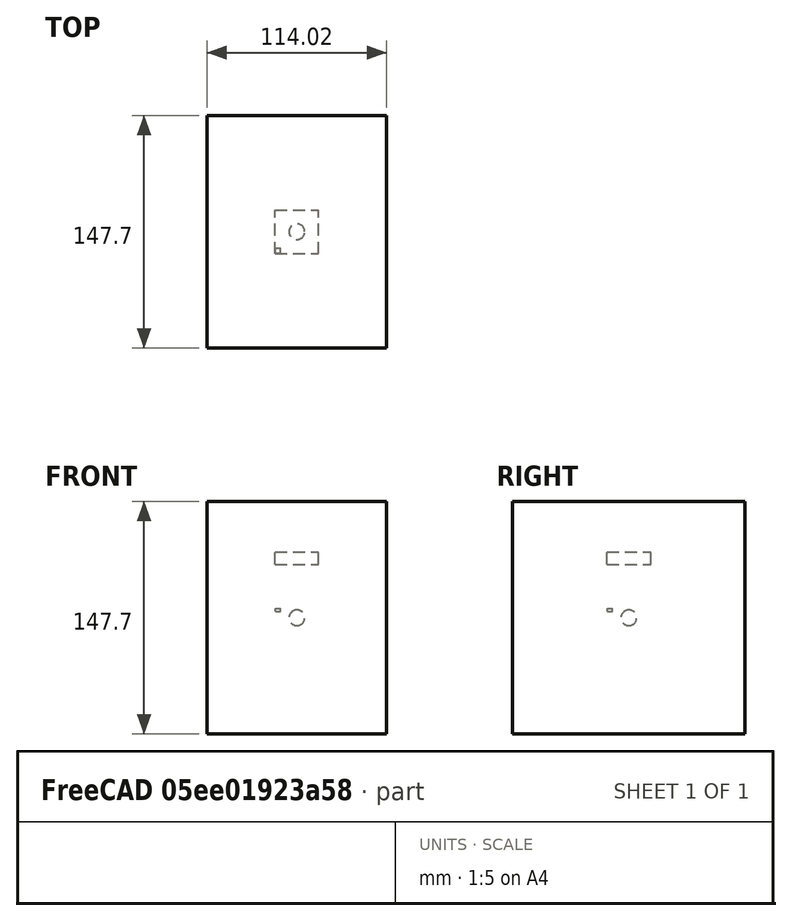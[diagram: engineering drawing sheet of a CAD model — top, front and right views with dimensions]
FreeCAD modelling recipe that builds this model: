
FCSTD DOCUMENT  (FreeCAD 1.0R39109 (Git))
Label: borderTest-1
License: All rights reserved
objects: App::DocumentObjectGroupPython×1272, Part::FeaturePython×7, App::Part×4, App::FeaturePython×1
note: 4 computed .brp shape members not serialized (recipe doc carries the construction recipe); baked Part::Feature solids carry a one-line shape summary decoded from their .brp

FEATURE [App::DocumentObjectGroupPython] HALFPI  # scripted group (container) (typed FeaturePython)
  name = HALFPI
  value = pi/2.
FEATURE [App::DocumentObjectGroupPython] PI  # scripted group (container) (typed FeaturePython)
  name = PI
  value = 1.*pi
FEATURE [App::DocumentObjectGroupPython] TWOPI  # scripted group (container) (typed FeaturePython)
  name = TWOPI
  value = 2.*pi
FEATURE [App::DocumentObjectGroupPython] Constants  # scripted group (container) (typed FeaturePython)
  Group = -> [HALFPI,PI,TWOPI]
FEATURE [App::DocumentObjectGroupPython] Variables  # scripted group (container) (typed FeaturePython)
FEATURE [App::DocumentObjectGroupPython] Quantities  # scripted group (container) (typed FeaturePython)
FEATURE [App::DocumentObjectGroupPython] Isotopes  # scripted group (container) (typed FeaturePython)
FEATURE [App::DocumentObjectGroupPython] Elements  # scripted group (container) (typed FeaturePython)
FEATURE [App::DocumentObjectGroupPython] G4_AIR  label="G4_AIR : 1.000"  # scripted group (container) (typed FeaturePython)
  n = 1
FEATURE [App::DocumentObjectGroupPython] Air  # scripted group (container) (typed FeaturePython)
  Dunit = mg/cm3
  Dvalue = 1.29
  Group = -> [G4_AIR]
  RINDEX = AirRINDEX
  conduct = 2
  density = 1
  expand = 3
  name = Air
  specific = 4
FEATURE [App::DocumentObjectGroupPython] SY  # scripted group (container) (typed FeaturePython)
  coldim = 1
  values = 100000/MeV
FEATURE [App::DocumentObjectGroupPython] RS  # scripted group (container) (typed FeaturePython)
  coldim = 1
  values = 1
FEATURE [App::DocumentObjectGroupPython] FTC  # scripted group (container) (typed FeaturePython)
  coldim = 1
  values = 21.5*ns
FEATURE [App::DocumentObjectGroupPython] STC  # scripted group (container) (typed FeaturePython)
  coldim = 1
  values = 43.8*ns
FEATURE [App::DocumentObjectGroupPython] RY1  # scripted group (container) (typed FeaturePython)
  coldim = 1
  values = 95
FEATURE [App::DocumentObjectGroupPython] RY2  # scripted group (container) (typed FeaturePython)
  coldim = 1
  values = 5
FEATURE [App::DocumentObjectGroupPython] YR  # scripted group (container) (typed FeaturePython)
  coldim = 1
  values = 0.8
FEATURE [App::DocumentObjectGroupPython] SCINTLAR  # scripted group (container) (typed FeaturePython)
  coldim = 2
  values = <blob: 2358 chars omitted>
FEATURE [App::DocumentObjectGroupPython] RINDEXLAR  # scripted group (container) (typed FeaturePython)
  coldim = 2
  values = <blob: 9384 chars omitted>
FEATURE [App::DocumentObjectGroupPython] ABSLENGTHLAR  # scripted group (container) (typed FeaturePython)
  coldim = 2
  values = 7.74901*eV 10.0*m 7.77525*eV 10.0*m 7.80167*eV 10.0*m 7.82827*eV 10.0*m 7.85506*eV 10.0*m 7.88202*eV 10.0*m 7.90917*eV 10.0*m 7.93651*eV 10.0*m 7.96404*eV 10.0*m 7.99176*eV 10.0*m 8.01968*eV 10.0*m 8.04779*eV 10.0*m 8.07609*eV 10.0*m 8.1046*eV 10.0*m 8.13331*eV 10.0*m 8.16222*eV 10.0*m 8.19134*eV 10.0*m 8.22067*eV 10.0*m 8.25021*eV 10.0*m 8.27996*eV 10.0*m 8.30993*eV 10.0*m 8.34012*eV 10.0*m 8.37052*eV 10.0*m 8.40115*eV 10.0*m 8.432*eV 10.0*m 8.46308*eV 10.0*m 8.4944*eV 10.0*m 8.52594*eV 10.0*m 8.55772*eV 10.0*m 8.58973*eV 10.0*m 8.62199*eV 10.0*m 8.65449*eV 10.0*m 8.68723*eV 10.0*m 8.72023*eV 10.0*m 8.75347*eV 10.0*m 8.78697*eV 10.0*m 8.82073*eV 10.0*m 8.85475*eV 10.0*m 8.88903*eV 10.0*m 8.92358*eV 10.0*m 8.9584*eV 10.0*m 8.99349*eV 10.0*m 9.02885*eV 10.0*m 9.0645*eV 10.0*m 9.10043*eV 10.0*m 9.13664*eV 10.0*m 9.17314*eV 10.0*m 9.20994*eV 10.0*m 9.24703*eV 10.0*m 9.28442*eV 10.0*m 9.32212*eV 10.0*m 9.36012*eV 10.0*m 9.39844*eV 10.0*m 9.43707*eV 10.0*m 9.47602*eV 10.0*m 9.51529*eV 10.0*m 9.55489*eV 10.0*m 9.59481*eV 10.0*m 9.63508*eV 10.0*m 9.67568*eV 10.0*m 9.71663*eV 10.0*m 9.75792*eV 10.0*m 9.79957*eV 10.0*m 9.84158*eV 10.0*m 9.88394*eV 10.0*m 9.92668*eV 10.0*m 9.96978*eV 10.0*m 10.0133*eV 10.0*m 10.0571*eV 10.0*m 10.1014*eV 10.0*m 10.146*eV 10.0*m 10.191*eV 10.0*m 10.2365*eV 10.0*m 10.2823*eV 10.0*m 10.3286*eV 10.0*m 10.3752*eV 10.0*m 10.4223*eV 10.0*m 10.4699*eV 10.0*m 10.5178*eV 10.0*m 10.5662*eV 10.0*m 10.6151*eV 10.0*m 10.6644*eV 10.0*m 10.7142*eV 10.0*m 10.7644*eV 10.0*m 10.8151*eV 10.0*m 10.8663*eV 10.0*m 10.9179*eV 10.0*m 10.9701*eV 10.0*m 11.0228*eV 10.0*m 11.076*eV 10.0*m 11.1296*eV 10.0*m 11.1839*eV 10.0*m 11.2386*eV 10.0*m 11.2939*eV 10.0*m 11.3497*eV 10.0*m 11.4061*eV 10.0*m 11.463*eV 10.0*m 11.5206*eV 10.0*m 11.5787*eV 10.0*m 11.6373*eV 10.0*m
FEATURE [App::DocumentObjectGroupPython] RAYLEIGHLAR  # scripted group (container) (typed FeaturePython)
  coldim = 2
  values = 7.74901*eV 90.0*cm 7.77525*eV 90.0*cm 7.80167*eV 90.0*cm 7.82827*eV 90.0*cm 7.85506*eV 90.0*cm 7.88202*eV 90.0*cm 7.90917*eV 90.0*cm 7.93651*eV 90.0*cm 7.96404*eV 90.0*cm 7.99176*eV 90.0*cm 8.01968*eV 90.0*cm 8.04779*eV 90.0*cm 8.07609*eV 90.0*cm 8.1046*eV 90.0*cm 8.13331*eV 90.0*cm 8.16222*eV 90.0*cm 8.19134*eV 90.0*cm 8.22067*eV 90.0*cm 8.25021*eV 90.0*cm 8.27996*eV 90.0*cm 8.30993*eV 90.0*cm 8.34012*eV 90.0*cm 8.37052*eV 90.0*cm 8.40115*eV 90.0*cm 8.432*eV 90.0*cm 8.46308*eV 90.0*cm 8.4944*eV 90.0*cm 8.52594*eV 90.0*cm 8.55772*eV 90.0*cm 8.58973*eV 90.0*cm 8.62199*eV 90.0*cm 8.65449*eV 90.0*cm 8.68723*eV 90.0*cm 8.72023*eV 90.0*cm 8.75347*eV 90.0*cm 8.78697*eV 90.0*cm 8.82073*eV 90.0*cm 8.85475*eV 90.0*cm 8.88903*eV 90.0*cm 8.92358*eV 90.0*cm 8.9584*eV 90.0*cm 8.99349*eV 90.0*cm 9.02885*eV 90.0*cm 9.0645*eV 90.0*cm 9.10043*eV 90.0*cm 9.13664*eV 90.0*cm 9.17314*eV 90.0*cm 9.20994*eV 90.0*cm 9.24703*eV 90.0*cm 9.28442*eV 90.0*cm 9.32212*eV 90.0*cm 9.36012*eV 90.0*cm 9.39844*eV 90.0*cm 9.43707*eV 90.0*cm 9.47602*eV 90.0*cm 9.51529*eV 90.0*cm 9.55489*eV 90.0*cm 9.59481*eV 90.0*cm 9.63508*eV 90.0*cm 9.67568*eV 90.0*cm 9.71663*eV 90.0*cm 9.75792*eV 90.0*cm 9.79957*eV 90.0*cm 9.84158*eV 90.0*cm 9.88394*eV 90.0*cm 9.92668*eV 90.0*cm 9.96978*eV 90.0*cm 10.0133*eV 90.0*cm 10.0571*eV 90.0*cm 10.1014*eV 90.0*cm 10.146*eV 90.0*cm 10.191*eV 90.0*cm 10.2365*eV 90.0*cm 10.2823*eV 90.0*cm 10.3286*eV 90.0*cm 10.3752*eV 90.0*cm 10.4223*eV 90.0*cm 10.4699*eV 90.0*cm 10.5178*eV 90.0*cm 10.5662*eV 90.0*cm 10.6151*eV 90.0*cm 10.6644*eV 90.0*cm 10.7142*eV 90.0*cm 10.7644*eV 90.0*cm 10.8151*eV 90.0*cm 10.8663*eV 90.0*cm 10.9179*eV 90.0*cm 10.9701*eV 90.0*cm 11.0228*eV 90.0*cm 11.076*eV 90.0*cm 11.1296*eV 90.0*cm 11.1839*eV 90.0*cm 11.2386*eV 90.0*cm 11.2939*eV 90.0*cm 11.3497*eV 90.0*cm 11.4061*eV 90.0*cm 11.463*eV 90.0*cm 11.5206*eV 90.0*cm 11.5787*eV 90.0*cm 11.6373*eV 90.0*cm
FEATURE [App::DocumentObjectGroupPython] REFLECTIVITY  # scripted group (container) (typed FeaturePython)
  coldim = 2
  values = 2.034*eV 0.98 2.068*eV 0.98 2.103*eV 0.98 2.139*eV 0.98 2.177*eV 0.98 2.216*eV 0.98 2.256*eV 0.98 2.298*eV 0.98 2.341*eV 0.98 2.386*eV 0.98 2.433*eV 0.98 2.481*eV 0.98 2.532*eV 0.98 2.585*eV 0.98 2.64*eV 0.98 2.697*eV 0.98 2.757*eV 0.98 2.82*eV 0.98 2.885*eV 0.98 2.954*eV 0.98 3.026*eV 0.98 3.102*eV 0.98 3.181*eV 0.98 3.265*eV 0.98 3.353*eV 0.98 3.446*eV 0.98 3.545*eV 0.98 3.649*eV 0.98 3.76*eV 0.98 3.877*eV 0.98 4.002*eV 0.98 4.136*eV 0.98 5.0*eV 0.98 6.0*eV 0.98 7.0*eV 0.98 8.0*eV 0.98 9.0*eV 0.98 9.0*eV 0.98 10.0*eV 0.98 11.0*eV 0.98 11.6*eV 0.98
FEATURE [App::DocumentObjectGroupPython] EFFICIENCY  # scripted group (container) (typed FeaturePython)
  coldim = 2
  values = 2.034*eV 1 2.068*eV 1 2.103*eV 1 2.139*eV 1 2.177*eV 1 2.216*eV 1 2.256*eV 1 2.298*eV 1 2.341*eV 1 2.386*eV 1 2.433*eV 1 2.481*eV 1 2.532*eV 1 2.585*eV 1 2.64*eV 1 2.697*eV 1 2.757*eV 1 2.82*eV 1 2.885*eV 1 2.954*eV 1 3.026*eV 1 3.102*eV 1 3.181*eV  1 3.265*eV 1 3.353*eV 1 3.446*eV 1 3.545*eV 1 3.649*eV 1 3.76*eV 1 3.877*eV 1 4.002*eV 1 4.136*eV 1 5.0*eV 1 6.0*eV 1 7.0*eV 1 8.0*eV 1 9.0*eV 1 9.0*eV 1 10.0*eV 1 11.0*eV 1 11.6*eV 1
FEATURE [App::DocumentObjectGroupPython] AirRINDEX  # scripted group (container) (typed FeaturePython)
  coldim = 2
  values = 2.034*eV 1 2.068*eV 1 2.103*eV 1 2.139*eV 1 2.177*eV 1 2.216*eV 1 2.256*eV 1 2.298*eV 1 2.341*eV 1 2.386*eV 1 2.433*eV 1 2.481*eV 1 2.532*eV 1 2.585*eV 1 2.64*eV 1 2.697*eV 1 2.757*eV 1 2.82*eV 1 2.885*eV 1 2.954*eV 1 3.026*eV 1 3.102*eV 1 3.181*eV 1 3.265*eV 1 3.353*eV 1 3.446*eV 1 3.545*eV 1 3.649*eV 1 3.76*eV 1 3.877*eV 1 4.002*eV 1 4.136*eV 1 5.0*eV 1 6.0*eV 1 7.0*eV 1 8.0*eV 1 9.0*eV 1 10.0*eV 1 11.0*eV 1 11.6*eV 1
FEATURE [App::DocumentObjectGroupPython] Matrix  # scripted group (container) (typed FeaturePython)
  Group = -> [SY,RS,FTC,STC,RY1,RY2,YR,SCINTLAR,RINDEXLAR,ABSLENGTHLAR,RAYLEIGHLAR,REFLECTIVITY,EFFICIENCY,AirRINDEX]
FEATURE [App::DocumentObjectGroupPython] ScintWrap  # scripted group (container) (typed FeaturePython)
  EFFICIENCY = EFFICIENCY
  REFLECTIVITY = REFLECTIVITY
  finish = 39
  model = 0
  type = 2
  value = 1
FEATURE [App::DocumentObjectGroupPython] Surfaces  # scripted group (container) (typed FeaturePython)
  Group = -> [ScintWrap]
FEATURE [App::DocumentObjectGroupPython] Opticals  # scripted group (container) (typed FeaturePython)
  Group = -> [Matrix,Surfaces]
FEATURE [App::DocumentObjectGroupPython] G4Isotopes  # scripted group (container) (typed FeaturePython)
FEATURE [App::DocumentObjectGroupPython] H_element  # scripted group (container) (typed FeaturePython)
  Z = 1
  atom_value = 1.008
  formula = H
  name = H_element
FEATURE [App::DocumentObjectGroupPython] He_element  # scripted group (container) (typed FeaturePython)
  Z = 2
  atom_value = 4.0026
  formula = He
  name = He_element
FEATURE [App::DocumentObjectGroupPython] Li_element  # scripted group (container) (typed FeaturePython)
  Z = 3
  atom_value = 6.94
  formula = Li
  name = Li_element
FEATURE [App::DocumentObjectGroupPython] Be_element  # scripted group (container) (typed FeaturePython)
  Z = 4
  atom_value = 9.01218
  formula = Be
  name = Be_element
FEATURE [App::DocumentObjectGroupPython] B_element  # scripted group (container) (typed FeaturePython)
  Z = 5
  atom_value = 10.81
  formula = B
  name = B_element
FEATURE [App::DocumentObjectGroupPython] C_element  # scripted group (container) (typed FeaturePython)
  Z = 6
  atom_value = 12.011
  formula = C
  name = C_element
FEATURE [App::DocumentObjectGroupPython] N_element  # scripted group (container) (typed FeaturePython)
  Z = 7
  atom_value = 14.007
  formula = N
  name = N_element
FEATURE [App::DocumentObjectGroupPython] O_element  # scripted group (container) (typed FeaturePython)
  Z = 8
  atom_value = 15.999
  formula = O
  name = O_element
FEATURE [App::DocumentObjectGroupPython] F_element  # scripted group (container) (typed FeaturePython)
  Z = 9
  atom_value = 18.9984
  formula = F
  name = F_element
FEATURE [App::DocumentObjectGroupPython] Ne_element  # scripted group (container) (typed FeaturePython)
  Z = 10
  atom_value = 20.1797
  formula = Ne
  name = Ne_element
FEATURE [App::DocumentObjectGroupPython] Na_element  # scripted group (container) (typed FeaturePython)
  Z = 11
  atom_value = 22.9898
  formula = Na
  name = Na_element
FEATURE [App::DocumentObjectGroupPython] Mg_element  # scripted group (container) (typed FeaturePython)
  Z = 12
  atom_value = 24.305
  formula = Mg
  name = Mg_element
FEATURE [App::DocumentObjectGroupPython] Al_element  # scripted group (container) (typed FeaturePython)
  Z = 13
  atom_value = 26.9815
  formula = Al
  name = Al_element
FEATURE [App::DocumentObjectGroupPython] Si_element  # scripted group (container) (typed FeaturePython)
  Z = 14
  atom_value = 28.085
  formula = Si
  name = Si_element
FEATURE [App::DocumentObjectGroupPython] P_element  # scripted group (container) (typed FeaturePython)
  Z = 15
  atom_value = 30.9738
  formula = P
  name = P_element
FEATURE [App::DocumentObjectGroupPython] S_element  # scripted group (container) (typed FeaturePython)
  Z = 16
  atom_value = 32.06
  formula = S
  name = S_element
FEATURE [App::DocumentObjectGroupPython] Cl_element  # scripted group (container) (typed FeaturePython)
  Z = 17
  atom_value = 35.45
  formula = Cl
  name = Cl_element
FEATURE [App::DocumentObjectGroupPython] Ar_element  # scripted group (container) (typed FeaturePython)
  Z = 18
  atom_value = 39.95
  formula = Ar
  name = Ar_element
FEATURE [App::DocumentObjectGroupPython] K_element  # scripted group (container) (typed FeaturePython)
  Z = 19
  atom_value = 39.0983
  formula = K
  name = K_element
FEATURE [App::DocumentObjectGroupPython] Ca_element  # scripted group (container) (typed FeaturePython)
  Z = 20
  atom_value = 40.078
  formula = Ca
  name = Ca_element
FEATURE [App::DocumentObjectGroupPython] Sc_element  # scripted group (container) (typed FeaturePython)
  Z = 21
  atom_value = 44.9559
  formula = Sc
  name = Sc_element
FEATURE [App::DocumentObjectGroupPython] Ti_element  # scripted group (container) (typed FeaturePython)
  Z = 22
  atom_value = 47.867
  formula = Ti
  name = Ti_element
FEATURE [App::DocumentObjectGroupPython] V_element  # scripted group (container) (typed FeaturePython)
  Z = 23
  atom_value = 50.9415
  formula = V
  name = V_element
FEATURE [App::DocumentObjectGroupPython] Cr_element  # scripted group (container) (typed FeaturePython)
  Z = 24
  atom_value = 51.9961
  formula = Cr
  name = Cr_element
FEATURE [App::DocumentObjectGroupPython] Mn_element  # scripted group (container) (typed FeaturePython)
  Z = 25
  atom_value = 54.938
  formula = Mn
  name = Mn_element
FEATURE [App::DocumentObjectGroupPython] Fe_element  # scripted group (container) (typed FeaturePython)
  Z = 26
  atom_value = 55.845
  formula = Fe
  name = Fe_element
FEATURE [App::DocumentObjectGroupPython] Co_element  # scripted group (container) (typed FeaturePython)
  Z = 27
  atom_value = 58.9332
  formula = Co
  name = Co_element
FEATURE [App::DocumentObjectGroupPython] Ni_element  # scripted group (container) (typed FeaturePython)
  Z = 28
  atom_value = 58.6934
  formula = Ni
  name = Ni_element
FEATURE [App::DocumentObjectGroupPython] Cu_element  # scripted group (container) (typed FeaturePython)
  Z = 29
  atom_value = 63.546
  formula = Cu
  name = Cu_element
FEATURE [App::DocumentObjectGroupPython] Zn_element  # scripted group (container) (typed FeaturePython)
  Z = 30
  atom_value = 65.38
  formula = Zn
  name = Zn_element
FEATURE [App::DocumentObjectGroupPython] Ga_element  # scripted group (container) (typed FeaturePython)
  Z = 31
  atom_value = 69.723
  formula = Ga
  name = Ga_element
FEATURE [App::DocumentObjectGroupPython] Ge_element  # scripted group (container) (typed FeaturePython)
  Z = 32
  atom_value = 72.63
  formula = Ge
  name = Ge_element
FEATURE [App::DocumentObjectGroupPython] As_element  # scripted group (container) (typed FeaturePython)
  Z = 33
  atom_value = 74.9216
  formula = As
  name = As_element
FEATURE [App::DocumentObjectGroupPython] Se_element  # scripted group (container) (typed FeaturePython)
  Z = 34
  atom_value = 78.971
  formula = Se
  name = Se_element
FEATURE [App::DocumentObjectGroupPython] Br_element  # scripted group (container) (typed FeaturePython)
  Z = 35
  atom_value = 79.904
  formula = Br
  name = Br_element
FEATURE [App::DocumentObjectGroupPython] Kr_element  # scripted group (container) (typed FeaturePython)
  Z = 36
  atom_value = 83.798
  formula = Kr
  name = Kr_element
FEATURE [App::DocumentObjectGroupPython] Rb_element  # scripted group (container) (typed FeaturePython)
  Z = 37
  atom_value = 85.4678
  formula = Rb
  name = Rb_element
FEATURE [App::DocumentObjectGroupPython] Sr_element  # scripted group (container) (typed FeaturePython)
  Z = 38
  atom_value = 87.62
  formula = Sr
  name = Sr_element
FEATURE [App::DocumentObjectGroupPython] Y_element  # scripted group (container) (typed FeaturePython)
  Z = 39
  atom_value = 88.9058
  formula = Y
  name = Y_element
FEATURE [App::DocumentObjectGroupPython] Zr_element  # scripted group (container) (typed FeaturePython)
  Z = 40
  atom_value = 91.224
  formula = Zr
  name = Zr_element
FEATURE [App::DocumentObjectGroupPython] Nb_element  # scripted group (container) (typed FeaturePython)
  Z = 41
  atom_value = 92.9064
  formula = Nb
  name = Nb_element
FEATURE [App::DocumentObjectGroupPython] Mo_element  # scripted group (container) (typed FeaturePython)
  Z = 42
  atom_value = 95.95
  formula = Mo
  name = Mo_element
FEATURE [App::DocumentObjectGroupPython] Tc_element  # scripted group (container) (typed FeaturePython)
  Z = 43
  atom_value = 97
  formula = Tc
  name = Tc_element
FEATURE [App::DocumentObjectGroupPython] Ru_element  # scripted group (container) (typed FeaturePython)
  Z = 44
  atom_value = 101.07
  formula = Ru
  name = Ru_element
FEATURE [App::DocumentObjectGroupPython] Rh_element  # scripted group (container) (typed FeaturePython)
  Z = 45
  atom_value = 102.905
  formula = Rh
  name = Rh_element
FEATURE [App::DocumentObjectGroupPython] Pd_element  # scripted group (container) (typed FeaturePython)
  Z = 46
  atom_value = 106.42
  formula = Pd
  name = Pd_element
FEATURE [App::DocumentObjectGroupPython] Ag_element  # scripted group (container) (typed FeaturePython)
  Z = 47
  atom_value = 107.868
  formula = Ag
  name = Ag_element
FEATURE [App::DocumentObjectGroupPython] Cd_element  # scripted group (container) (typed FeaturePython)
  Z = 48
  atom_value = 112.414
  formula = Cd
  name = Cd_element
FEATURE [App::DocumentObjectGroupPython] In_element  # scripted group (container) (typed FeaturePython)
  Z = 49
  atom_value = 114.818
  formula = In
  name = In_element
FEATURE [App::DocumentObjectGroupPython] Sn_element  # scripted group (container) (typed FeaturePython)
  Z = 50
  atom_value = 118.71
  formula = Sn
  name = Sn_element
FEATURE [App::DocumentObjectGroupPython] Sb_element  # scripted group (container) (typed FeaturePython)
  Z = 51
  atom_value = 121.76
  formula = Sb
  name = Sb_element
FEATURE [App::DocumentObjectGroupPython] Te_element  # scripted group (container) (typed FeaturePython)
  Z = 52
  atom_value = 127.6
  formula = Te
  name = Te_element
FEATURE [App::DocumentObjectGroupPython] I_element  # scripted group (container) (typed FeaturePython)
  Z = 53
  atom_value = 126.904
  formula = I
  name = I_element
FEATURE [App::DocumentObjectGroupPython] Xe_element  # scripted group (container) (typed FeaturePython)
  Z = 54
  atom_value = 131.293
  formula = Xe
  name = Xe_element
FEATURE [App::DocumentObjectGroupPython] Cs_element  # scripted group (container) (typed FeaturePython)
  Z = 55
  atom_value = 132.905
  formula = Cs
  name = Cs_element
FEATURE [App::DocumentObjectGroupPython] Ba_element  # scripted group (container) (typed FeaturePython)
  Z = 56
  atom_value = 137.327
  formula = Ba
  name = Ba_element
FEATURE [App::DocumentObjectGroupPython] La_element  # scripted group (container) (typed FeaturePython)
  Z = 57
  atom_value = 138.905
  formula = La
  name = La_element
FEATURE [App::DocumentObjectGroupPython] Ce_element  # scripted group (container) (typed FeaturePython)
  Z = 58
  atom_value = 140.116
  formula = Ce
  name = Ce_element
FEATURE [App::DocumentObjectGroupPython] Pr_element  # scripted group (container) (typed FeaturePython)
  Z = 59
  atom_value = 140.908
  formula = Pr
  name = Pr_element
FEATURE [App::DocumentObjectGroupPython] Nd_element  # scripted group (container) (typed FeaturePython)
  Z = 60
  atom_value = 144.242
  formula = Nd
  name = Nd_element
FEATURE [App::DocumentObjectGroupPython] Pm_element  # scripted group (container) (typed FeaturePython)
  Z = 61
  atom_value = 145
  formula = Pm
  name = Pm_element
FEATURE [App::DocumentObjectGroupPython] Sm_element  # scripted group (container) (typed FeaturePython)
  Z = 62
  atom_value = 150.36
  formula = Sm
  name = Sm_element
FEATURE [App::DocumentObjectGroupPython] Eu_element  # scripted group (container) (typed FeaturePython)
  Z = 63
  atom_value = 151.964
  formula = Eu
  name = Eu_element
FEATURE [App::DocumentObjectGroupPython] Gd_element  # scripted group (container) (typed FeaturePython)
  Z = 64
  atom_value = 157.25
  formula = Gd
  name = Gd_element
FEATURE [App::DocumentObjectGroupPython] Tb_element  # scripted group (container) (typed FeaturePython)
  Z = 65
  atom_value = 158.925
  formula = Tb
  name = Tb_element
FEATURE [App::DocumentObjectGroupPython] Dy_element  # scripted group (container) (typed FeaturePython)
  Z = 66
  atom_value = 162.5
  formula = Dy
  name = Dy_element
FEATURE [App::DocumentObjectGroupPython] Ho_element  # scripted group (container) (typed FeaturePython)
  Z = 67
  atom_value = 164.93
  formula = Ho
  name = Ho_element
FEATURE [App::DocumentObjectGroupPython] Er_element  # scripted group (container) (typed FeaturePython)
  Z = 68
  atom_value = 167.259
  formula = Er
  name = Er_element
FEATURE [App::DocumentObjectGroupPython] Tm_element  # scripted group (container) (typed FeaturePython)
  Z = 69
  atom_value = 168.934
  formula = Tm
  name = Tm_element
FEATURE [App::DocumentObjectGroupPython] Yb_element  # scripted group (container) (typed FeaturePython)
  Z = 70
  atom_value = 173.045
  formula = Yb
  name = Yb_element
FEATURE [App::DocumentObjectGroupPython] Lu_element  # scripted group (container) (typed FeaturePython)
  Z = 71
  atom_value = 174.967
  formula = Lu
  name = Lu_element
FEATURE [App::DocumentObjectGroupPython] Hf_element  # scripted group (container) (typed FeaturePython)
  Z = 72
  atom_value = 178.49
  formula = Hf
  name = Hf_element
FEATURE [App::DocumentObjectGroupPython] Ta_element  # scripted group (container) (typed FeaturePython)
  Z = 73
  atom_value = 180.948
  formula = Ta
  name = Ta_element
FEATURE [App::DocumentObjectGroupPython] W_element  # scripted group (container) (typed FeaturePython)
  Z = 74
  atom_value = 183.84
  formula = W
  name = W_element
FEATURE [App::DocumentObjectGroupPython] Re_element  # scripted group (container) (typed FeaturePython)
  Z = 75
  atom_value = 186.207
  formula = Re
  name = Re_element
FEATURE [App::DocumentObjectGroupPython] Os_element  # scripted group (container) (typed FeaturePython)
  Z = 76
  atom_value = 190.23
  formula = Os
  name = Os_element
FEATURE [App::DocumentObjectGroupPython] Ir_element  # scripted group (container) (typed FeaturePython)
  Z = 77
  atom_value = 192.217
  formula = Ir
  name = Ir_element
FEATURE [App::DocumentObjectGroupPython] Pt_element  # scripted group (container) (typed FeaturePython)
  Z = 78
  atom_value = 195.084
  formula = Pt
  name = Pt_element
FEATURE [App::DocumentObjectGroupPython] Au_element  # scripted group (container) (typed FeaturePython)
  Z = 79
  atom_value = 196.967
  formula = Au
  name = Au_element
FEATURE [App::DocumentObjectGroupPython] Hg_element  # scripted group (container) (typed FeaturePython)
  Z = 80
  atom_value = 200.592
  formula = Hg
  name = Hg_element
FEATURE [App::DocumentObjectGroupPython] Tl_element  # scripted group (container) (typed FeaturePython)
  Z = 81
  atom_value = 204.38
  formula = Tl
  name = Tl_element
FEATURE [App::DocumentObjectGroupPython] Pb_element  # scripted group (container) (typed FeaturePython)
  Z = 82
  atom_value = 207.2
  formula = Pb
  name = Pb_element
FEATURE [App::DocumentObjectGroupPython] Bi_element  # scripted group (container) (typed FeaturePython)
  Z = 83
  atom_value = 208.98
  formula = Bi
  name = Bi_element
FEATURE [App::DocumentObjectGroupPython] Po_element  # scripted group (container) (typed FeaturePython)
  Z = 84
  atom_value = 209
  formula = Po
  name = Po_element
FEATURE [App::DocumentObjectGroupPython] At_element  # scripted group (container) (typed FeaturePython)
  Z = 85
  atom_value = 210
  formula = At
  name = At_element
FEATURE [App::DocumentObjectGroupPython] Rn_element  # scripted group (container) (typed FeaturePython)
  Z = 86
  atom_value = 222
  formula = Rn
  name = Rn_element
FEATURE [App::DocumentObjectGroupPython] Fr_element  # scripted group (container) (typed FeaturePython)
  Z = 87
  atom_value = 223
  formula = Fr
  name = Fr_element
FEATURE [App::DocumentObjectGroupPython] Ra_element  # scripted group (container) (typed FeaturePython)
  Z = 88
  atom_value = 226
  formula = Ra
  name = Ra_element
FEATURE [App::DocumentObjectGroupPython] Ac_element  # scripted group (container) (typed FeaturePython)
  Z = 89
  atom_value = 227
  formula = Ac
  name = Ac_element
FEATURE [App::DocumentObjectGroupPython] Th_element  # scripted group (container) (typed FeaturePython)
  Z = 90
  atom_value = 232.038
  formula = Th
  name = Th_element
FEATURE [App::DocumentObjectGroupPython] Pa_element  # scripted group (container) (typed FeaturePython)
  Z = 91
  atom_value = 231.036
  formula = Pa
  name = Pa_element
FEATURE [App::DocumentObjectGroupPython] U_element  # scripted group (container) (typed FeaturePython)
  Z = 92
  atom_value = 238.029
  formula = U
  name = U_element
FEATURE [App::DocumentObjectGroupPython] Np_element  # scripted group (container) (typed FeaturePython)
  Z = 93
  atom_value = 237
  formula = Np
  name = Np_element
FEATURE [App::DocumentObjectGroupPython] Pu_element  # scripted group (container) (typed FeaturePython)
  Z = 94
  atom_value = 244
  formula = Pu
  name = Pu_element
FEATURE [App::DocumentObjectGroupPython] Am_element  # scripted group (container) (typed FeaturePython)
  Z = 95
  atom_value = 243
  formula = Am
  name = Am_element
FEATURE [App::DocumentObjectGroupPython] Cm_element  # scripted group (container) (typed FeaturePython)
  Z = 96
  atom_value = 247
  formula = Cm
  name = Cm_element
FEATURE [App::DocumentObjectGroupPython] Bk_element  # scripted group (container) (typed FeaturePython)
  Z = 97
  atom_value = 247
  formula = Bk
  name = Bk_element
FEATURE [App::DocumentObjectGroupPython] Cf_element  # scripted group (container) (typed FeaturePython)
  Z = 98
  atom_value = 251
  formula = Cf
  name = Cf_element
FEATURE [App::DocumentObjectGroupPython] G4Elements  # scripted group (container) (typed FeaturePython)
  Group = -> [H_element,He_element,Li_element,Be_element,B_element,C_element,N_element,O_element,F_element,Ne_element,Na_element,Mg_element,Al_element,Si_element,P_element,S_element,Cl_element,Ar_element,K_element,Ca_element,Sc_element,Ti_element,V_element,Cr_element,Mn_element,Fe_element,Co_element,Ni_element,Cu_element,Zn_element,Ga_element,Ge_element,As_element,Se_element,Br_element,Kr_element,Rb_element,+61 more]
FEATURE [App::DocumentObjectGroupPython] H_element001  label="H_element : 0.101"  # scripted group (container) (typed FeaturePython)
  n = 0.101327
FEATURE [App::DocumentObjectGroupPython] C_element001  label="C_element : 0.775"  # scripted group (container) (typed FeaturePython)
  n = 0.7755
FEATURE [App::DocumentObjectGroupPython] N_element001  label="N_element : 0.035"  # scripted group (container) (typed FeaturePython)
  n = 0.035057
FEATURE [App::DocumentObjectGroupPython] O_element001  label="O_element : 0.052"  # scripted group (container) (typed FeaturePython)
  n = 0.0523159
FEATURE [App::DocumentObjectGroupPython] F_element001  label="F_element : 0.017"  # scripted group (container) (typed FeaturePython)
  n = 0.017422
FEATURE [App::DocumentObjectGroupPython] Ca_element001  label="Ca_element : 0.018"  # scripted group (container) (typed FeaturePython)
  n = 0.018378
FEATURE [App::DocumentObjectGroupPython] G4_A_150_TISSUE  label="G4_A-150_TISSUE"  # scripted group (container) (typed FeaturePython)
  Dunit = g/cm3
  Dvalue = 1.127
  Group = -> [H_element001,C_element001,N_element001,O_element001,F_element001,Ca_element001]
  conduct = 2
  density = 1
  expand = 3
  formula = G4_A-150_TISSUE
  name = G4_A-150_TISSUE
  specific = 4
FEATURE [App::DocumentObjectGroupPython] C_element002  label="C_element : 3"  # scripted group (container) (typed FeaturePython)
  n = 3
  ref = C_element
FEATURE [App::DocumentObjectGroupPython] H_element002  label="H_element : 6"  # scripted group (container) (typed FeaturePython)
  n = 6
  ref = H_element
FEATURE [App::DocumentObjectGroupPython] O_element002  label="O_element : 1"  # scripted group (container) (typed FeaturePython)
  n = 1
  ref = O_element
FEATURE [App::DocumentObjectGroupPython] G4_ACETONE  # scripted group (container) (typed FeaturePython)
  Dunit = g/cm3
  Dvalue = 0.7899
  Group = -> [C_element002,H_element002,O_element002]
  conduct = 2
  density = 1
  expand = 3
  formula = G4_ACETONE
  name = G4_ACETONE
  specific = 4
FEATURE [App::DocumentObjectGroupPython] C_element003  label="C_element : 2"  # scripted group (container) (typed FeaturePython)
  n = 2
  ref = C_element
FEATURE [App::DocumentObjectGroupPython] H_element003  label="H_element : 2"  # scripted group (container) (typed FeaturePython)
  n = 2
  ref = H_element
FEATURE [App::DocumentObjectGroupPython] G4_ACETYLENE  # scripted group (container) (typed FeaturePython)
  Dunit = g/cm3
  Dvalue = 0.0010967
  Group = -> [C_element003,H_element003]
  conduct = 2
  density = 1
  expand = 3
  formula = G4_ACETYLENE
  name = G4_ACETYLENE
  specific = 4
FEATURE [App::DocumentObjectGroupPython] C_element004  label="C_element : 5"  # scripted group (container) (typed FeaturePython)
  n = 5
  ref = C_element
FEATURE [App::DocumentObjectGroupPython] H_element004  label="H_element : 5"  # scripted group (container) (typed FeaturePython)
  n = 5
  ref = H_element
FEATURE [App::DocumentObjectGroupPython] N_element002  label="N_element : 5"  # scripted group (container) (typed FeaturePython)
  n = 5
  ref = N_element
FEATURE [App::DocumentObjectGroupPython] G4_ADENINE  # scripted group (container) (typed FeaturePython)
  Dunit = g/cm3
  Dvalue = 1.6
  Group = -> [C_element004,H_element004,N_element002]
  conduct = 2
  density = 1
  expand = 3
  formula = G4_ADENINE
  name = G4_ADENINE
  specific = 4
FEATURE [App::DocumentObjectGroupPython] H_element005  label="H_element : 0.114"  # scripted group (container) (typed FeaturePython)
  n = 0.114
FEATURE [App::DocumentObjectGroupPython] C_element005  label="C_element : 0.598"  # scripted group (container) (typed FeaturePython)
  n = 0.598
FEATURE [App::DocumentObjectGroupPython] N_element003  label="N_element : 0.007"  # scripted group (container) (typed FeaturePython)
  n = 0.007
FEATURE [App::DocumentObjectGroupPython] O_element003  label="O_element : 0.278"  # scripted group (container) (typed FeaturePython)
  n = 0.278
FEATURE [App::DocumentObjectGroupPython] Na_element001  label="Na_element : 0.001"  # scripted group (container) (typed FeaturePython)
  n = 0.001
FEATURE [App::DocumentObjectGroupPython] S_element001  label="S_element : 0.001"  # scripted group (container) (typed FeaturePython)
  n = 0.001
FEATURE [App::DocumentObjectGroupPython] Cl_element001  label="Cl_element : 0.001"  # scripted group (container) (typed FeaturePython)
  n = 0.001
FEATURE [App::DocumentObjectGroupPython] G4_ADIPOSE_TISSUE_ICRP  # scripted group (container) (typed FeaturePython)
  Dunit = g/cm3
  Dvalue = 0.95
  Group = -> [H_element005,C_element005,N_element003,O_element003,Na_element001,S_element001,Cl_element001]
  conduct = 2
  density = 1
  expand = 3
  formula = G4_ADIPOSE_TISSUE_ICRP
  name = G4_ADIPOSE_TISSUE_ICRP
  specific = 4
FEATURE [App::DocumentObjectGroupPython] C_element006  label="C_element : 0.000"  # scripted group (container) (typed FeaturePython)
  n = 0.000124
FEATURE [App::DocumentObjectGroupPython] N_element004  label="N_element : 0.755"  # scripted group (container) (typed FeaturePython)
  n = 0.755268
FEATURE [App::DocumentObjectGroupPython] O_element004  label="O_element : 0.232"  # scripted group (container) (typed FeaturePython)
  n = 0.231781
FEATURE [App::DocumentObjectGroupPython] Ar_element001  label="Ar_element : 0.013"  # scripted group (container) (typed FeaturePython)
  n = 0.012827
FEATURE [App::DocumentObjectGroupPython] G4_AIR001  label="G4_AIR"  # scripted group (container) (typed FeaturePython)
  Dunit = g/cm3
  Dvalue = 0.00120479
  Group = -> [C_element006,N_element004,O_element004,Ar_element001]
  conduct = 2
  density = 1
  expand = 3
  formula = G4_AIR
  name = G4_AIR
  specific = 4
FEATURE [App::DocumentObjectGroupPython] C_element007  label="C_element : 006"  # scripted group (container) (typed FeaturePython)
  n = 3
  ref = C_element
FEATURE [App::DocumentObjectGroupPython] H_element006  label="H_element : 7"  # scripted group (container) (typed FeaturePython)
  n = 7
  ref = H_element
FEATURE [App::DocumentObjectGroupPython] N_element005  label="N_element : 1"  # scripted group (container) (typed FeaturePython)
  n = 1
  ref = N_element
FEATURE [App::DocumentObjectGroupPython] O_element005  label="O_element : 2"  # scripted group (container) (typed FeaturePython)
  n = 2
  ref = O_element
FEATURE [App::DocumentObjectGroupPython] G4_ALANINE  # scripted group (container) (typed FeaturePython)
  Dunit = g/cm3
  Dvalue = 1.42
  Group = -> [C_element007,H_element006,N_element005,O_element005]
  conduct = 2
  density = 1
  expand = 3
  formula = G4_ALANINE
  name = G4_ALANINE
  specific = 4
FEATURE [App::DocumentObjectGroupPython] Al_element001  label="Al_element : 2"  # scripted group (container) (typed FeaturePython)
  n = 2
  ref = Al_element
FEATURE [App::DocumentObjectGroupPython] O_element006  label="O_element : 3"  # scripted group (container) (typed FeaturePython)
  n = 3
  ref = O_element
FEATURE [App::DocumentObjectGroupPython] G4_ALUMINUM_OXIDE  # scripted group (container) (typed FeaturePython)
  Dunit = g/cm3
  Dvalue = 3.97
  Group = -> [Al_element001,O_element006]
  conduct = 2
  density = 1
  expand = 3
  formula = G4_ALUMINUM_OXIDE
  name = G4_ALUMINUM_OXIDE
  specific = 4
FEATURE [App::DocumentObjectGroupPython] H_element007  label="H_element : 0.106"  # scripted group (container) (typed FeaturePython)
  n = 0.10593
FEATURE [App::DocumentObjectGroupPython] C_element008  label="C_element : 0.789"  # scripted group (container) (typed FeaturePython)
  n = 0.788974
FEATURE [App::DocumentObjectGroupPython] O_element007  label="O_element : 0.105"  # scripted group (container) (typed FeaturePython)
  n = 0.105096
FEATURE [App::DocumentObjectGroupPython] G4_AMBER  # scripted group (container) (typed FeaturePython)
  Dunit = g/cm3
  Dvalue = 1.1
  Group = -> [H_element007,C_element008,O_element007]
  conduct = 2
  density = 1
  expand = 3
  formula = G4_AMBER
  name = G4_AMBER
  specific = 4
FEATURE [App::DocumentObjectGroupPython] N_element006  label="N_element : 006"  # scripted group (container) (typed FeaturePython)
  n = 1
  ref = N_element
FEATURE [App::DocumentObjectGroupPython] H_element008  label="H_element : 3"  # scripted group (container) (typed FeaturePython)
  n = 3
  ref = H_element
FEATURE [App::DocumentObjectGroupPython] G4_AMMONIA  # scripted group (container) (typed FeaturePython)
  Dunit = g/cm3
  Dvalue = 0.000826019
  Group = -> [N_element006,H_element008]
  conduct = 2
  density = 1
  expand = 3
  formula = G4_AMMONIA
  name = G4_AMMONIA
  specific = 4
FEATURE [App::DocumentObjectGroupPython] C_element009  label="C_element : 6"  # scripted group (container) (typed FeaturePython)
  n = 6
  ref = C_element
FEATURE [App::DocumentObjectGroupPython] H_element009  label="H_element : 008"  # scripted group (container) (typed FeaturePython)
  n = 7
  ref = H_element
FEATURE [App::DocumentObjectGroupPython] N_element007  label="N_element : 007"  # scripted group (container) (typed FeaturePython)
  n = 1
  ref = N_element
FEATURE [App::DocumentObjectGroupPython] G4_ANILINE  # scripted group (container) (typed FeaturePython)
  Dunit = g/cm3
  Dvalue = 1.0235
  Group = -> [C_element009,H_element009,N_element007]
  conduct = 2
  density = 1
  expand = 3
  formula = G4_ANILINE
  name = G4_ANILINE
  specific = 4
FEATURE [App::DocumentObjectGroupPython] C_element010  label="C_element : 14"  # scripted group (container) (typed FeaturePython)
  n = 14
  ref = C_element
FEATURE [App::DocumentObjectGroupPython] H_element010  label="H_element : 10"  # scripted group (container) (typed FeaturePython)
  n = 10
  ref = H_element
FEATURE [App::DocumentObjectGroupPython] G4_ANTHRACENE  # scripted group (container) (typed FeaturePython)
  Dunit = g/cm3
  Dvalue = 1.283
  Group = -> [C_element010,H_element010]
  conduct = 2
  density = 1
  expand = 3
  formula = G4_ANTHRACENE
  name = G4_ANTHRACENE
  specific = 4
FEATURE [App::DocumentObjectGroupPython] H_element011  label="H_element : 0.065"  # scripted group (container) (typed FeaturePython)
  n = 0.0654709
FEATURE [App::DocumentObjectGroupPython] C_element011  label="C_element : 0.537"  # scripted group (container) (typed FeaturePython)
  n = 0.536944
FEATURE [App::DocumentObjectGroupPython] N_element008  label="N_element : 0.021"  # scripted group (container) (typed FeaturePython)
  n = 0.0215
FEATURE [App::DocumentObjectGroupPython] O_element008  label="O_element : 0.032"  # scripted group (container) (typed FeaturePython)
  n = 0.032085
FEATURE [App::DocumentObjectGroupPython] F_element002  label="F_element : 0.167"  # scripted group (container) (typed FeaturePython)
  n = 0.167411
FEATURE [App::DocumentObjectGroupPython] Ca_element002  label="Ca_element : 0.177"  # scripted group (container) (typed FeaturePython)
  n = 0.176589
FEATURE [App::DocumentObjectGroupPython] G4_B_100_BONE  label="G4_B-100_BONE"  # scripted group (container) (typed FeaturePython)
  Dunit = g/cm3
  Dvalue = 1.45
  Group = -> [H_element011,C_element011,N_element008,O_element008,F_element002,Ca_element002]
  conduct = 2
  density = 1
  expand = 3
  formula = G4_B-100_BONE
  name = G4_B-100_BONE
  specific = 4
FEATURE [App::DocumentObjectGroupPython] H_element012  label="H_element : 0.057"  # scripted group (container) (typed FeaturePython)
  n = 0.057441
FEATURE [App::DocumentObjectGroupPython] C_element012  label="C_element : 0.790"  # scripted group (container) (typed FeaturePython)
  n = 0.774591
FEATURE [App::DocumentObjectGroupPython] O_element009  label="O_element : 0.168"  # scripted group (container) (typed FeaturePython)
  n = 0.167968
FEATURE [App::DocumentObjectGroupPython] G4_BAKELITE  # scripted group (container) (typed FeaturePython)
  Dunit = g/cm3
  Dvalue = 1.25
  Group = -> [H_element012,C_element012,O_element009]
  conduct = 2
  density = 1
  expand = 3
  formula = G4_BAKELITE
  name = G4_BAKELITE
  specific = 4
FEATURE [App::DocumentObjectGroupPython] Ba_element001  label="Ba_element : 1"  # scripted group (container) (typed FeaturePython)
  n = 1
  ref = Ba_element
FEATURE [App::DocumentObjectGroupPython] F_element003  label="F_element : 2"  # scripted group (container) (typed FeaturePython)
  n = 2
  ref = F_element
FEATURE [App::DocumentObjectGroupPython] G4_BARIUM_FLUORIDE  # scripted group (container) (typed FeaturePython)
  Dunit = g/cm3
  Dvalue = 4.89
  Group = -> [Ba_element001,F_element003]
  conduct = 2
  density = 1
  expand = 3
  formula = G4_BARIUM_FLUORIDE
  name = G4_BARIUM_FLUORIDE
  specific = 4
FEATURE [App::DocumentObjectGroupPython] Ba_element002  label="Ba_element : 002"  # scripted group (container) (typed FeaturePython)
  n = 1
  ref = Ba_element
FEATURE [App::DocumentObjectGroupPython] S_element002  label="S_element : 1"  # scripted group (container) (typed FeaturePython)
  n = 1
  ref = S_element
FEATURE [App::DocumentObjectGroupPython] O_element010  label="O_element : 4"  # scripted group (container) (typed FeaturePython)
  n = 4
  ref = O_element
FEATURE [App::DocumentObjectGroupPython] G4_BARIUM_SULFATE  # scripted group (container) (typed FeaturePython)
  Dunit = g/cm3
  Dvalue = 4.5
  Group = -> [Ba_element002,S_element002,O_element010]
  conduct = 2
  density = 1
  expand = 3
  formula = G4_BARIUM_SULFATE
  name = G4_BARIUM_SULFATE
  specific = 4
FEATURE [App::DocumentObjectGroupPython] C_element013  label="C_element : 007"  # scripted group (container) (typed FeaturePython)
  n = 6
  ref = C_element
FEATURE [App::DocumentObjectGroupPython] H_element013  label="H_element : 009"  # scripted group (container) (typed FeaturePython)
  n = 6
  ref = H_element
FEATURE [App::DocumentObjectGroupPython] G4_BENZENE  # scripted group (container) (typed FeaturePython)
  Dunit = g/cm3
  Dvalue = 0.87865
  Group = -> [C_element013,H_element013]
  conduct = 2
  density = 1
  expand = 3
  formula = G4_BENZENE
  name = G4_BENZENE
  specific = 4
FEATURE [App::DocumentObjectGroupPython] Be_element001  label="Be_element : 1"  # scripted group (container) (typed FeaturePython)
  n = 1
  ref = Be_element
FEATURE [App::DocumentObjectGroupPython] O_element011  label="O_element : 005"  # scripted group (container) (typed FeaturePython)
  n = 1
  ref = O_element
FEATURE [App::DocumentObjectGroupPython] G4_BERYLLIUM_OXIDE  # scripted group (container) (typed FeaturePython)
  Dunit = g/cm3
  Dvalue = 3.01
  Group = -> [Be_element001,O_element011]
  conduct = 2
  density = 1
  expand = 3
  formula = G4_BERYLLIUM_OXIDE
  name = G4_BERYLLIUM_OXIDE
  specific = 4
FEATURE [App::DocumentObjectGroupPython] Bi_element001  label="Bi_element : 4"  # scripted group (container) (typed FeaturePython)
  n = 4
  ref = Bi_element
FEATURE [App::DocumentObjectGroupPython] Ge_element001  label="Ge_element : 3"  # scripted group (container) (typed FeaturePython)
  n = 3
  ref = Ge_element
FEATURE [App::DocumentObjectGroupPython] O_element012  label="O_element : 12"  # scripted group (container) (typed FeaturePython)
  n = 12
  ref = O_element
FEATURE [App::DocumentObjectGroupPython] G4_BGO  # scripted group (container) (typed FeaturePython)
  Dunit = g/cm3
  Dvalue = 7.13
  Group = -> [Bi_element001,Ge_element001,O_element012]
  conduct = 2
  density = 1
  expand = 3
  formula = G4_BGO
  name = G4_BGO
  specific = 4
FEATURE [App::DocumentObjectGroupPython] H_element014  label="H_element : 0.102"  # scripted group (container) (typed FeaturePython)
  n = 0.102
FEATURE [App::DocumentObjectGroupPython] C_element014  label="C_element : 0.110"  # scripted group (container) (typed FeaturePython)
  n = 0.11
FEATURE [App::DocumentObjectGroupPython] N_element009  label="N_element : 0.033"  # scripted group (container) (typed FeaturePython)
  n = 0.033
FEATURE [App::DocumentObjectGroupPython] O_element013  label="O_element : 0.745"  # scripted group (container) (typed FeaturePython)
  n = 0.745
FEATURE [App::DocumentObjectGroupPython] Na_element002  label="Na_element : 0.002"  # scripted group (container) (typed FeaturePython)
  n = 0.001
FEATURE [App::DocumentObjectGroupPython] P_element001  label="P_element : 0.001"  # scripted group (container) (typed FeaturePython)
  n = 0.001
FEATURE [App::DocumentObjectGroupPython] S_element003  label="S_element : 0.002"  # scripted group (container) (typed FeaturePython)
  n = 0.002
FEATURE [App::DocumentObjectGroupPython] Cl_element002  label="Cl_element : 0.003"  # scripted group (container) (typed FeaturePython)
  n = 0.003
FEATURE [App::DocumentObjectGroupPython] K_element001  label="K_element : 0.002"  # scripted group (container) (typed FeaturePython)
  n = 0.002
FEATURE [App::DocumentObjectGroupPython] Fe_element001  label="Fe_element : 0.001"  # scripted group (container) (typed FeaturePython)
  n = 0.001
FEATURE [App::DocumentObjectGroupPython] G4_BLOOD_ICRP  # scripted group (container) (typed FeaturePython)
  Dunit = g/cm3
  Dvalue = 1.06
  Group = -> [H_element014,C_element014,N_element009,O_element013,Na_element002,P_element001,S_element003,Cl_element002,K_element001,Fe_element001]
  conduct = 2
  density = 1
  expand = 3
  formula = G4_BLOOD_ICRP
  name = G4_BLOOD_ICRP
  specific = 4
FEATURE [App::DocumentObjectGroupPython] H_element015  label="H_element : 0.064"  # scripted group (container) (typed FeaturePython)
  n = 0.064
FEATURE [App::DocumentObjectGroupPython] C_element015  label="C_element : 0.278"  # scripted group (container) (typed FeaturePython)
  n = 0.278
FEATURE [App::DocumentObjectGroupPython] N_element010  label="N_element : 0.027"  # scripted group (container) (typed FeaturePython)
  n = 0.027
FEATURE [App::DocumentObjectGroupPython] O_element014  label="O_element : 0.410"  # scripted group (container) (typed FeaturePython)
  n = 0.41
FEATURE [App::DocumentObjectGroupPython] Mg_element001  label="Mg_element : 0.002"  # scripted group (container) (typed FeaturePython)
  n = 0.002
FEATURE [App::DocumentObjectGroupPython] P_element002  label="P_element : 0.070"  # scripted group (container) (typed FeaturePython)
  n = 0.07
FEATURE [App::DocumentObjectGroupPython] S_element004  label="S_element : 0.003"  # scripted group (container) (typed FeaturePython)
  n = 0.002
FEATURE [App::DocumentObjectGroupPython] Ca_element003  label="Ca_element : 0.147"  # scripted group (container) (typed FeaturePython)
  n = 0.147
FEATURE [App::DocumentObjectGroupPython] G4_BONE_COMPACT_ICRU  # scripted group (container) (typed FeaturePython)
  Dunit = g/cm3
  Dvalue = 1.85
  Group = -> [H_element015,C_element015,N_element010,O_element014,Mg_element001,P_element002,S_element004,Ca_element003]
  conduct = 2
  density = 1
  expand = 3
  formula = G4_BONE_COMPACT_ICRU
  name = G4_BONE_COMPACT_ICRU
  specific = 4
FEATURE [App::DocumentObjectGroupPython] H_element016  label="H_element : 0.034"  # scripted group (container) (typed FeaturePython)
  n = 0.034
FEATURE [App::DocumentObjectGroupPython] C_element016  label="C_element : 0.155"  # scripted group (container) (typed FeaturePython)
  n = 0.155
FEATURE [App::DocumentObjectGroupPython] N_element011  label="N_element : 0.042"  # scripted group (container) (typed FeaturePython)
  n = 0.042
FEATURE [App::DocumentObjectGroupPython] O_element015  label="O_element : 0.435"  # scripted group (container) (typed FeaturePython)
  n = 0.435
FEATURE [App::DocumentObjectGroupPython] Na_element003  label="Na_element : 0.003"  # scripted group (container) (typed FeaturePython)
  n = 0.001
FEATURE [App::DocumentObjectGroupPython] Mg_element002  label="Mg_element : 0.003"  # scripted group (container) (typed FeaturePython)
  n = 0.002
FEATURE [App::DocumentObjectGroupPython] P_element003  label="P_element : 0.103"  # scripted group (container) (typed FeaturePython)
  n = 0.103
FEATURE [App::DocumentObjectGroupPython] S_element005  label="S_element : 0.004"  # scripted group (container) (typed FeaturePython)
  n = 0.003
FEATURE [App::DocumentObjectGroupPython] Ca_element004  label="Ca_element : 0.225"  # scripted group (container) (typed FeaturePython)
  n = 0.225
FEATURE [App::DocumentObjectGroupPython] G4_BONE_CORTICAL_ICRP  # scripted group (container) (typed FeaturePython)
  Dunit = g/cm3
  Dvalue = 1.92
  Group = -> [H_element016,C_element016,N_element011,O_element015,Na_element003,Mg_element002,P_element003,S_element005,Ca_element004]
  conduct = 2
  density = 1
  expand = 3
  formula = G4_BONE_CORTICAL_ICRP
  name = G4_BONE_CORTICAL_ICRP
  specific = 4
FEATURE [App::DocumentObjectGroupPython] B_element001  label="B_element : 4"  # scripted group (container) (typed FeaturePython)
  n = 4
  ref = B_element
FEATURE [App::DocumentObjectGroupPython] C_element017  label="C_element : 1"  # scripted group (container) (typed FeaturePython)
  n = 1
  ref = C_element
FEATURE [App::DocumentObjectGroupPython] G4_BORON_CARBIDE  # scripted group (container) (typed FeaturePython)
  Dunit = g/cm3
  Dvalue = 2.52
  Group = -> [B_element001,C_element017]
  conduct = 2
  density = 1
  expand = 3
  formula = G4_BORON_CARBIDE
  name = G4_BORON_CARBIDE
  specific = 4
FEATURE [App::DocumentObjectGroupPython] B_element002  label="B_element : 2"  # scripted group (container) (typed FeaturePython)
  n = 2
  ref = B_element
FEATURE [App::DocumentObjectGroupPython] O_element016  label="O_element : 006"  # scripted group (container) (typed FeaturePython)
  n = 3
  ref = O_element
FEATURE [App::DocumentObjectGroupPython] G4_BORON_OXIDE  # scripted group (container) (typed FeaturePython)
  Dunit = g/cm3
  Dvalue = 1.812
  Group = -> [B_element002,O_element016]
  conduct = 2
  density = 1
  expand = 3
  formula = G4_BORON_OXIDE
  name = G4_BORON_OXIDE
  specific = 4
FEATURE [App::DocumentObjectGroupPython] H_element017  label="H_element : 0.107"  # scripted group (container) (typed FeaturePython)
  n = 0.107
FEATURE [App::DocumentObjectGroupPython] C_element018  label="C_element : 0.145"  # scripted group (container) (typed FeaturePython)
  n = 0.145
FEATURE [App::DocumentObjectGroupPython] N_element012  label="N_element : 0.022"  # scripted group (container) (typed FeaturePython)
  n = 0.022
FEATURE [App::DocumentObjectGroupPython] O_element017  label="O_element : 0.712"  # scripted group (container) (typed FeaturePython)
  n = 0.712
FEATURE [App::DocumentObjectGroupPython] Na_element004  label="Na_element : 0.004"  # scripted group (container) (typed FeaturePython)
  n = 0.002
FEATURE [App::DocumentObjectGroupPython] P_element004  label="P_element : 0.004"  # scripted group (container) (typed FeaturePython)
  n = 0.004
FEATURE [App::DocumentObjectGroupPython] S_element006  label="S_element : 0.005"  # scripted group (container) (typed FeaturePython)
  n = 0.002
FEATURE [App::DocumentObjectGroupPython] Cl_element003  label="Cl_element : 0.004"  # scripted group (container) (typed FeaturePython)
  n = 0.003
FEATURE [App::DocumentObjectGroupPython] K_element002  label="K_element : 0.003"  # scripted group (container) (typed FeaturePython)
  n = 0.003
FEATURE [App::DocumentObjectGroupPython] G4_BRAIN_ICRP  # scripted group (container) (typed FeaturePython)
  Dunit = g/cm3
  Dvalue = 1.04
  Group = -> [H_element017,C_element018,N_element012,O_element017,Na_element004,P_element004,S_element006,Cl_element003,K_element002]
  conduct = 2
  density = 1
  expand = 3
  formula = G4_BRAIN_ICRP
  name = G4_BRAIN_ICRP
  specific = 4
FEATURE [App::DocumentObjectGroupPython] C_element019  label="C_element : 4"  # scripted group (container) (typed FeaturePython)
  n = 4
  ref = C_element
FEATURE [App::DocumentObjectGroupPython] H_element018  label="H_element : 010"  # scripted group (container) (typed FeaturePython)
  n = 10
  ref = H_element
FEATURE [App::DocumentObjectGroupPython] G4_BUTANE  # scripted group (container) (typed FeaturePython)
  Dunit = g/cm3
  Dvalue = 0.00249343
  Group = -> [C_element019,H_element018]
  conduct = 2
  density = 1
  expand = 3
  formula = G4_BUTANE
  name = G4_BUTANE
  specific = 4
FEATURE [App::DocumentObjectGroupPython] C_element020  label="C_element : 008"  # scripted group (container) (typed FeaturePython)
  n = 4
  ref = C_element
FEATURE [App::DocumentObjectGroupPython] H_element019  label="H_element : 011"  # scripted group (container) (typed FeaturePython)
  n = 10
  ref = H_element
FEATURE [App::DocumentObjectGroupPython] O_element018  label="O_element : 007"  # scripted group (container) (typed FeaturePython)
  n = 1
  ref = O_element
FEATURE [App::DocumentObjectGroupPython] G4_N_BUTYL_ALCOHOL  label="G4_N-BUTYL_ALCOHOL"  # scripted group (container) (typed FeaturePython)
  Dunit = g/cm3
  Dvalue = 0.8098
  Group = -> [C_element020,H_element019,O_element018]
  conduct = 2
  density = 1
  expand = 3
  formula = G4_N-BUTYL_ALCOHOL
  name = G4_N-BUTYL_ALCOHOL
  specific = 4
FEATURE [App::DocumentObjectGroupPython] H_element020  label="H_element : 0.025"  # scripted group (container) (typed FeaturePython)
  n = 0.02468
FEATURE [App::DocumentObjectGroupPython] C_element021  label="C_element : 0.502"  # scripted group (container) (typed FeaturePython)
  n = 0.501611
FEATURE [App::DocumentObjectGroupPython] O_element019  label="O_element : 0.005"  # scripted group (container) (typed FeaturePython)
  n = 0.004527
FEATURE [App::DocumentObjectGroupPython] F_element004  label="F_element : 0.465"  # scripted group (container) (typed FeaturePython)
  n = 0.465209
FEATURE [App::DocumentObjectGroupPython] Si_element001  label="Si_element : 0.004"  # scripted group (container) (typed FeaturePython)
  n = 0.003973
FEATURE [App::DocumentObjectGroupPython] G4_C_552  label="G4_C-552"  # scripted group (container) (typed FeaturePython)
  Dunit = g/cm3
  Dvalue = 1.76
  Group = -> [H_element020,C_element021,O_element019,F_element004,Si_element001]
  conduct = 2
  density = 1
  expand = 3
  formula = G4_C-552
  name = G4_C-552
  specific = 4
FEATURE [App::DocumentObjectGroupPython] Cd_element001  label="Cd_element : 1"  # scripted group (container) (typed FeaturePython)
  n = 1
  ref = Cd_element
FEATURE [App::DocumentObjectGroupPython] Te_element001  label="Te_element : 1"  # scripted group (container) (typed FeaturePython)
  n = 1
  ref = Te_element
FEATURE [App::DocumentObjectGroupPython] G4_CADMIUM_TELLURIDE  # scripted group (container) (typed FeaturePython)
  Dunit = g/cm3
  Dvalue = 6.2
  Group = -> [Cd_element001,Te_element001]
  conduct = 2
  density = 1
  expand = 3
  formula = G4_CADMIUM_TELLURIDE
  name = G4_CADMIUM_TELLURIDE
  specific = 4
FEATURE [App::DocumentObjectGroupPython] Cd_element002  label="Cd_element : 002"  # scripted group (container) (typed FeaturePython)
  n = 1
  ref = Cd_element
FEATURE [App::DocumentObjectGroupPython] W_element001  label="W_element : 1"  # scripted group (container) (typed FeaturePython)
  n = 1
  ref = W_element
FEATURE [App::DocumentObjectGroupPython] O_element020  label="O_element : 008"  # scripted group (container) (typed FeaturePython)
  n = 4
  ref = O_element
FEATURE [App::DocumentObjectGroupPython] G4_CADMIUM_TUNGSTATE  # scripted group (container) (typed FeaturePython)
  Dunit = g/cm3
  Dvalue = 7.9
  Group = -> [Cd_element002,W_element001,O_element020]
  conduct = 2
  density = 1
  expand = 3
  formula = G4_CADMIUM_TUNGSTATE
  name = G4_CADMIUM_TUNGSTATE
  specific = 4
FEATURE [App::DocumentObjectGroupPython] Ca_element005  label="Ca_element : 1"  # scripted group (container) (typed FeaturePython)
  n = 1
  ref = Ca_element
FEATURE [App::DocumentObjectGroupPython] C_element022  label="C_element : 009"  # scripted group (container) (typed FeaturePython)
  n = 1
  ref = C_element
FEATURE [App::DocumentObjectGroupPython] O_element021  label="O_element : 009"  # scripted group (container) (typed FeaturePython)
  n = 3
  ref = O_element
FEATURE [App::DocumentObjectGroupPython] G4_CALCIUM_CARBONATE  # scripted group (container) (typed FeaturePython)
  Dunit = g/cm3
  Dvalue = 2.8
  Group = -> [Ca_element005,C_element022,O_element021]
  conduct = 2
  density = 1
  expand = 3
  formula = G4_CALCIUM_CARBONATE
  name = G4_CALCIUM_CARBONATE
  specific = 4
FEATURE [App::DocumentObjectGroupPython] Ca_element006  label="Ca_element : 002"  # scripted group (container) (typed FeaturePython)
  n = 1
  ref = Ca_element
FEATURE [App::DocumentObjectGroupPython] F_element005  label="F_element : 003"  # scripted group (container) (typed FeaturePython)
  n = 2
  ref = F_element
FEATURE [App::DocumentObjectGroupPython] G4_CALCIUM_FLUORIDE  # scripted group (container) (typed FeaturePython)
  Dunit = g/cm3
  Dvalue = 3.18
  Group = -> [Ca_element006,F_element005]
  conduct = 2
  density = 1
  expand = 3
  formula = G4_CALCIUM_FLUORIDE
  name = G4_CALCIUM_FLUORIDE
  specific = 4
FEATURE [App::DocumentObjectGroupPython] Ca_element007  label="Ca_element : 003"  # scripted group (container) (typed FeaturePython)
  n = 1
  ref = Ca_element
FEATURE [App::DocumentObjectGroupPython] O_element022  label="O_element : 010"  # scripted group (container) (typed FeaturePython)
  n = 1
  ref = O_element
FEATURE [App::DocumentObjectGroupPython] G4_CALCIUM_OXIDE  # scripted group (container) (typed FeaturePython)
  Dunit = g/cm3
  Dvalue = 3.3
  Group = -> [Ca_element007,O_element022]
  conduct = 2
  density = 1
  expand = 3
  formula = G4_CALCIUM_OXIDE
  name = G4_CALCIUM_OXIDE
  specific = 4
FEATURE [App::DocumentObjectGroupPython] Ca_element008  label="Ca_element : 004"  # scripted group (container) (typed FeaturePython)
  n = 1
  ref = Ca_element
FEATURE [App::DocumentObjectGroupPython] S_element007  label="S_element : 002"  # scripted group (container) (typed FeaturePython)
  n = 1
  ref = S_element
FEATURE [App::DocumentObjectGroupPython] O_element023  label="O_element : 011"  # scripted group (container) (typed FeaturePython)
  n = 4
  ref = O_element
FEATURE [App::DocumentObjectGroupPython] G4_CALCIUM_SULFATE  # scripted group (container) (typed FeaturePython)
  Dunit = g/cm3
  Dvalue = 2.96
  Group = -> [Ca_element008,S_element007,O_element023]
  conduct = 2
  density = 1
  expand = 3
  formula = G4_CALCIUM_SULFATE
  name = G4_CALCIUM_SULFATE
  specific = 4
FEATURE [App::DocumentObjectGroupPython] Ca_element009  label="Ca_element : 005"  # scripted group (container) (typed FeaturePython)
  n = 1
  ref = Ca_element
FEATURE [App::DocumentObjectGroupPython] W_element002  label="W_element : 002"  # scripted group (container) (typed FeaturePython)
  n = 1
  ref = W_element
FEATURE [App::DocumentObjectGroupPython] O_element024  label="O_element : 012"  # scripted group (container) (typed FeaturePython)
  n = 4
  ref = O_element
FEATURE [App::DocumentObjectGroupPython] G4_CALCIUM_TUNGSTATE  # scripted group (container) (typed FeaturePython)
  Dunit = g/cm3
  Dvalue = 6.062
  Group = -> [Ca_element009,W_element002,O_element024]
  conduct = 2
  density = 1
  expand = 3
  formula = G4_CALCIUM_TUNGSTATE
  name = G4_CALCIUM_TUNGSTATE
  specific = 4
FEATURE [App::DocumentObjectGroupPython] C_element023  label="C_element : 010"  # scripted group (container) (typed FeaturePython)
  n = 1
  ref = C_element
FEATURE [App::DocumentObjectGroupPython] O_element025  label="O_element : 013"  # scripted group (container) (typed FeaturePython)
  n = 2
  ref = O_element
FEATURE [App::DocumentObjectGroupPython] G4_CARBON_DIOXIDE  # scripted group (container) (typed FeaturePython)
  Dunit = g/cm3
  Dvalue = 0.00184212
  Group = -> [C_element023,O_element025]
  conduct = 2
  density = 1
  expand = 3
  formula = G4_CARBON_DIOXIDE
  name = G4_CARBON_DIOXIDE
  specific = 4
FEATURE [App::DocumentObjectGroupPython] C_element024  label="C_element : 011"  # scripted group (container) (typed FeaturePython)
  n = 1
  ref = C_element
FEATURE [App::DocumentObjectGroupPython] Cl_element004  label="Cl_element : 4"  # scripted group (container) (typed FeaturePython)
  n = 4
  ref = Cl_element
FEATURE [App::DocumentObjectGroupPython] G4_CARBON_TETRACHLORIDE  # scripted group (container) (typed FeaturePython)
  Dunit = g/cm3
  Dvalue = 1.594
  Group = -> [C_element024,Cl_element004]
  conduct = 2
  density = 1
  expand = 3
  formula = G4_CARBON_TETRACHLORIDE
  name = G4_CARBON_TETRACHLORIDE
  specific = 4
FEATURE [App::DocumentObjectGroupPython] C_element025  label="C_element : 012"  # scripted group (container) (typed FeaturePython)
  n = 6
  ref = C_element
FEATURE [App::DocumentObjectGroupPython] H_element021  label="H_element : 012"  # scripted group (container) (typed FeaturePython)
  n = 10
  ref = H_element
FEATURE [App::DocumentObjectGroupPython] O_element026  label="O_element : 5"  # scripted group (container) (typed FeaturePython)
  n = 5
  ref = O_element
FEATURE [App::DocumentObjectGroupPython] G4_CELLULOSE_CELLOPHANE  # scripted group (container) (typed FeaturePython)
  Dunit = g/cm3
  Dvalue = 1.42
  Group = -> [C_element025,H_element021,O_element026]
  conduct = 2
  density = 1
  expand = 3
  formula = G4_CELLULOSE_CELLOPHANE
  name = G4_CELLULOSE_CELLOPHANE
  specific = 4
FEATURE [App::DocumentObjectGroupPython] H_element022  label="H_element : 0.067"  # scripted group (container) (typed FeaturePython)
  n = 0.067125
FEATURE [App::DocumentObjectGroupPython] C_element026  label="C_element : 0.545"  # scripted group (container) (typed FeaturePython)
  n = 0.545403
FEATURE [App::DocumentObjectGroupPython] O_element027  label="O_element : 0.387"  # scripted group (container) (typed FeaturePython)
  n = 0.387472
FEATURE [App::DocumentObjectGroupPython] G4_CELLULOSE_BUTYRATE  # scripted group (container) (typed FeaturePython)
  Dunit = g/cm3
  Dvalue = 1.2
  Group = -> [H_element022,C_element026,O_element027]
  conduct = 2
  density = 1
  expand = 3
  formula = G4_CELLULOSE_BUTYRATE
  name = G4_CELLULOSE_BUTYRATE
  specific = 4
FEATURE [App::DocumentObjectGroupPython] H_element023  label="H_element : 0.029"  # scripted group (container) (typed FeaturePython)
  n = 0.029216
FEATURE [App::DocumentObjectGroupPython] C_element027  label="C_element : 0.271"  # scripted group (container) (typed FeaturePython)
  n = 0.271296
FEATURE [App::DocumentObjectGroupPython] N_element013  label="N_element : 0.121"  # scripted group (container) (typed FeaturePython)
  n = 0.121276
FEATURE [App::DocumentObjectGroupPython] O_element028  label="O_element : 0.578"  # scripted group (container) (typed FeaturePython)
  n = 0.578212
FEATURE [App::DocumentObjectGroupPython] G4_CELLULOSE_NITRATE  # scripted group (container) (typed FeaturePython)
  Dunit = g/cm3
  Dvalue = 1.49
  Group = -> [H_element023,C_element027,N_element013,O_element028]
  conduct = 2
  density = 1
  expand = 3
  formula = G4_CELLULOSE_NITRATE
  name = G4_CELLULOSE_NITRATE
  specific = 4
FEATURE [App::DocumentObjectGroupPython] H_element024  label="H_element : 0.108"  # scripted group (container) (typed FeaturePython)
  n = 0.107596
FEATURE [App::DocumentObjectGroupPython] N_element014  label="N_element : 0.001"  # scripted group (container) (typed FeaturePython)
  n = 0.0008
FEATURE [App::DocumentObjectGroupPython] O_element029  label="O_element : 0.875"  # scripted group (container) (typed FeaturePython)
  n = 0.874976
FEATURE [App::DocumentObjectGroupPython] S_element008  label="S_element : 0.015"  # scripted group (container) (typed FeaturePython)
  n = 0.014627
FEATURE [App::DocumentObjectGroupPython] Ce_element001  label="Ce_element : 0.002"  # scripted group (container) (typed FeaturePython)
  n = 0.002001
FEATURE [App::DocumentObjectGroupPython] G4_CERIC_SULFATE  # scripted group (container) (typed FeaturePython)
  Dunit = g/cm3
  Dvalue = 1.03
  Group = -> [H_element024,N_element014,O_element029,S_element008,Ce_element001]
  conduct = 2
  density = 1
  expand = 3
  formula = G4_CERIC_SULFATE
  name = G4_CERIC_SULFATE
  specific = 4
FEATURE [App::DocumentObjectGroupPython] Cs_element001  label="Cs_element : 1"  # scripted group (container) (typed FeaturePython)
  n = 1
  ref = Cs_element
FEATURE [App::DocumentObjectGroupPython] F_element006  label="F_element : 1"  # scripted group (container) (typed FeaturePython)
  n = 1
  ref = F_element
FEATURE [App::DocumentObjectGroupPython] G4_CESIUM_FLUORIDE  # scripted group (container) (typed FeaturePython)
  Dunit = g/cm3
  Dvalue = 4.115
  Group = -> [Cs_element001,F_element006]
  conduct = 2
  density = 1
  expand = 3
  formula = G4_CESIUM_FLUORIDE
  name = G4_CESIUM_FLUORIDE
  specific = 4
FEATURE [App::DocumentObjectGroupPython] Cs_element002  label="Cs_element : 002"  # scripted group (container) (typed FeaturePython)
  n = 1
  ref = Cs_element
FEATURE [App::DocumentObjectGroupPython] I_element001  label="I_element : 1"  # scripted group (container) (typed FeaturePython)
  n = 1
  ref = I_element
FEATURE [App::DocumentObjectGroupPython] G4_CESIUM_IODIDE001  label="G4_CESIUM_IODIDE"  # scripted group (container) (typed FeaturePython)
  Dunit = g/cm3
  Dvalue = 4.51
  Group = -> [Cs_element002,I_element001]
  conduct = 2
  density = 1
  expand = 3
  formula = G4_CESIUM_IODIDE
  name = G4_CESIUM_IODIDE
  specific = 4
FEATURE [App::DocumentObjectGroupPython] C_element028  label="C_element : 013"  # scripted group (container) (typed FeaturePython)
  n = 6
  ref = C_element
FEATURE [App::DocumentObjectGroupPython] H_element025  label="H_element : 013"  # scripted group (container) (typed FeaturePython)
  n = 5
  ref = H_element
FEATURE [App::DocumentObjectGroupPython] Cl_element005  label="Cl_element : 1"  # scripted group (container) (typed FeaturePython)
  n = 1
  ref = Cl_element
FEATURE [App::DocumentObjectGroupPython] G4_CHLOROBENZENE  # scripted group (container) (typed FeaturePython)
  Dunit = g/cm3
  Dvalue = 1.1058
  Group = -> [C_element028,H_element025,Cl_element005]
  conduct = 2
  density = 1
  expand = 3
  formula = G4_CHLOROBENZENE
  name = G4_CHLOROBENZENE
  specific = 4
FEATURE [App::DocumentObjectGroupPython] C_element029  label="C_element : 014"  # scripted group (container) (typed FeaturePython)
  n = 1
  ref = C_element
FEATURE [App::DocumentObjectGroupPython] H_element026  label="H_element : 1"  # scripted group (container) (typed FeaturePython)
  n = 1
  ref = H_element
FEATURE [App::DocumentObjectGroupPython] Cl_element006  label="Cl_element : 3"  # scripted group (container) (typed FeaturePython)
  n = 3
  ref = Cl_element
FEATURE [App::DocumentObjectGroupPython] G4_CHLOROFORM  # scripted group (container) (typed FeaturePython)
  Dunit = g/cm3
  Dvalue = 1.4832
  Group = -> [C_element029,H_element026,Cl_element006]
  conduct = 2
  density = 1
  expand = 3
  formula = G4_CHLOROFORM
  name = G4_CHLOROFORM
  specific = 4
FEATURE [App::DocumentObjectGroupPython] H_element027  label="H_element : 0.010"  # scripted group (container) (typed FeaturePython)
  n = 0.01
FEATURE [App::DocumentObjectGroupPython] C_element030  label="C_element : 0.001"  # scripted group (container) (typed FeaturePython)
  n = 0.001
FEATURE [App::DocumentObjectGroupPython] O_element030  label="O_element : 0.529"  # scripted group (container) (typed FeaturePython)
  n = 0.529107
FEATURE [App::DocumentObjectGroupPython] Na_element005  label="Na_element : 0.016"  # scripted group (container) (typed FeaturePython)
  n = 0.016
FEATURE [App::DocumentObjectGroupPython] Mg_element003  label="Mg_element : 0.004"  # scripted group (container) (typed FeaturePython)
  n = 0.002
FEATURE [App::DocumentObjectGroupPython] Al_element002  label="Al_element : 0.034"  # scripted group (container) (typed FeaturePython)
  n = 0.033872
FEATURE [App::DocumentObjectGroupPython] Si_element002  label="Si_element : 0.337"  # scripted group (container) (typed FeaturePython)
  n = 0.337021
FEATURE [App::DocumentObjectGroupPython] K_element003  label="K_element : 0.013"  # scripted group (container) (typed FeaturePython)
  n = 0.013
FEATURE [App::DocumentObjectGroupPython] Ca_element010  label="Ca_element : 0.044"  # scripted group (container) (typed FeaturePython)
  n = 0.044
FEATURE [App::DocumentObjectGroupPython] Fe_element002  label="Fe_element : 0.014"  # scripted group (container) (typed FeaturePython)
  n = 0.014
FEATURE [App::DocumentObjectGroupPython] G4_CONCRETE  # scripted group (container) (typed FeaturePython)
  Dunit = g/cm3
  Dvalue = 2.3
  Group = -> [H_element027,C_element030,O_element030,Na_element005,Mg_element003,Al_element002,Si_element002,K_element003,Ca_element010,Fe_element002]
  conduct = 2
  density = 1
  expand = 3
  formula = G4_CONCRETE
  name = G4_CONCRETE
  specific = 4
FEATURE [App::DocumentObjectGroupPython] C_element031  label="C_element : 015"  # scripted group (container) (typed FeaturePython)
  n = 6
  ref = C_element
FEATURE [App::DocumentObjectGroupPython] H_element028  label="H_element : 12"  # scripted group (container) (typed FeaturePython)
  n = 12
  ref = H_element
FEATURE [App::DocumentObjectGroupPython] G4_CYCLOHEXANE  # scripted group (container) (typed FeaturePython)
  Dunit = g/cm3
  Dvalue = 0.779
  Group = -> [C_element031,H_element028]
  conduct = 2
  density = 1
  expand = 3
  formula = G4_CYCLOHEXANE
  name = G4_CYCLOHEXANE
  specific = 4
FEATURE [App::DocumentObjectGroupPython] C_element032  label="C_element : 016"  # scripted group (container) (typed FeaturePython)
  n = 6
  ref = C_element
FEATURE [App::DocumentObjectGroupPython] H_element029  label="H_element : 4"  # scripted group (container) (typed FeaturePython)
  n = 4
  ref = H_element
FEATURE [App::DocumentObjectGroupPython] Cl_element007  label="Cl_element : 2"  # scripted group (container) (typed FeaturePython)
  n = 2
  ref = Cl_element
FEATURE [App::DocumentObjectGroupPython] G4_1_2_DICHLOROBENZENE  label="G4_1.2-DICHLOROBENZENE"  # scripted group (container) (typed FeaturePython)
  Dunit = g/cm3
  Dvalue = 1.3048
  Group = -> [C_element032,H_element029,Cl_element007]
  conduct = 2
  density = 1
  expand = 3
  formula = G4_1.2-DICHLOROBENZENE
  name = G4_1.2-DICHLOROBENZENE
  specific = 4
FEATURE [App::DocumentObjectGroupPython] C_element033  label="C_element : 017"  # scripted group (container) (typed FeaturePython)
  n = 4
  ref = C_element
FEATURE [App::DocumentObjectGroupPython] H_element030  label="H_element : 8"  # scripted group (container) (typed FeaturePython)
  n = 8
  ref = H_element
FEATURE [App::DocumentObjectGroupPython] O_element031  label="O_element : 014"  # scripted group (container) (typed FeaturePython)
  n = 1
  ref = O_element
FEATURE [App::DocumentObjectGroupPython] Cl_element008  label="Cl_element : 005"  # scripted group (container) (typed FeaturePython)
  n = 2
  ref = Cl_element
FEATURE [App::DocumentObjectGroupPython] G4_DICHLORODIETHYL_ETHER  # scripted group (container) (typed FeaturePython)
  Dunit = g/cm3
  Dvalue = 1.2199
  Group = -> [C_element033,H_element030,O_element031,Cl_element008]
  conduct = 2
  density = 1
  expand = 3
  formula = G4_DICHLORODIETHYL_ETHER
  name = G4_DICHLORODIETHYL_ETHER
  specific = 4
FEATURE [App::DocumentObjectGroupPython] C_element034  label="C_element : 018"  # scripted group (container) (typed FeaturePython)
  n = 2
  ref = C_element
FEATURE [App::DocumentObjectGroupPython] H_element031  label="H_element : 014"  # scripted group (container) (typed FeaturePython)
  n = 4
  ref = H_element
FEATURE [App::DocumentObjectGroupPython] Cl_element009  label="Cl_element : 006"  # scripted group (container) (typed FeaturePython)
  n = 2
  ref = Cl_element
FEATURE [App::DocumentObjectGroupPython] G4_1_2_DICHLOROETHANE  label="G4_1.2-DICHLOROETHANE"  # scripted group (container) (typed FeaturePython)
  Dunit = g/cm3
  Dvalue = 1.2351
  Group = -> [C_element034,H_element031,Cl_element009]
  conduct = 2
  density = 1
  expand = 3
  formula = G4_1.2-DICHLOROETHANE
  name = G4_1.2-DICHLOROETHANE
  specific = 4
FEATURE [App::DocumentObjectGroupPython] C_element035  label="C_element : 019"  # scripted group (container) (typed FeaturePython)
  n = 4
  ref = C_element
FEATURE [App::DocumentObjectGroupPython] H_element032  label="H_element : 015"  # scripted group (container) (typed FeaturePython)
  n = 10
  ref = H_element
FEATURE [App::DocumentObjectGroupPython] O_element032  label="O_element : 015"  # scripted group (container) (typed FeaturePython)
  n = 1
  ref = O_element
FEATURE [App::DocumentObjectGroupPython] G4_DIETHYL_ETHER  # scripted group (container) (typed FeaturePython)
  Dunit = g/cm3
  Dvalue = 0.71378
  Group = -> [C_element035,H_element032,O_element032]
  conduct = 2
  density = 1
  expand = 3
  formula = G4_DIETHYL_ETHER
  name = G4_DIETHYL_ETHER
  specific = 4
FEATURE [App::DocumentObjectGroupPython] C_element036  label="C_element : 020"  # scripted group (container) (typed FeaturePython)
  n = 3
  ref = C_element
FEATURE [App::DocumentObjectGroupPython] H_element033  label="H_element : 016"  # scripted group (container) (typed FeaturePython)
  n = 7
  ref = H_element
FEATURE [App::DocumentObjectGroupPython] N_element015  label="N_element : 008"  # scripted group (container) (typed FeaturePython)
  n = 1
  ref = N_element
FEATURE [App::DocumentObjectGroupPython] O_element033  label="O_element : 016"  # scripted group (container) (typed FeaturePython)
  n = 1
  ref = O_element
FEATURE [App::DocumentObjectGroupPython] G4_N_N_DIMETHYL_FORMAMIDE  label="G4_N.N-DIMETHYL_FORMAMIDE"  # scripted group (container) (typed FeaturePython)
  Dunit = g/cm3
  Dvalue = 0.9487
  Group = -> [C_element036,H_element033,N_element015,O_element033]
  conduct = 2
  density = 1
  expand = 3
  formula = G4_N.N-DIMETHYL_FORMAMIDE
  name = G4_N.N-DIMETHYL_FORMAMIDE
  specific = 4
FEATURE [App::DocumentObjectGroupPython] C_element037  label="C_element : 021"  # scripted group (container) (typed FeaturePython)
  n = 2
  ref = C_element
FEATURE [App::DocumentObjectGroupPython] H_element034  label="H_element : 017"  # scripted group (container) (typed FeaturePython)
  n = 6
  ref = H_element
FEATURE [App::DocumentObjectGroupPython] O_element034  label="O_element : 017"  # scripted group (container) (typed FeaturePython)
  n = 1
  ref = O_element
FEATURE [App::DocumentObjectGroupPython] S_element009  label="S_element : 003"  # scripted group (container) (typed FeaturePython)
  n = 1
  ref = S_element
FEATURE [App::DocumentObjectGroupPython] G4_DIMETHYL_SULFOXIDE  # scripted group (container) (typed FeaturePython)
  Dunit = g/cm3
  Dvalue = 1.1014
  Group = -> [C_element037,H_element034,O_element034,S_element009]
  conduct = 2
  density = 1
  expand = 3
  formula = G4_DIMETHYL_SULFOXIDE
  name = G4_DIMETHYL_SULFOXIDE
  specific = 4
FEATURE [App::DocumentObjectGroupPython] C_element038  label="C_element : 022"  # scripted group (container) (typed FeaturePython)
  n = 2
  ref = C_element
FEATURE [App::DocumentObjectGroupPython] H_element035  label="H_element : 018"  # scripted group (container) (typed FeaturePython)
  n = 6
  ref = H_element
FEATURE [App::DocumentObjectGroupPython] G4_ETHANE  # scripted group (container) (typed FeaturePython)
  Dunit = g/cm3
  Dvalue = 0.00125324
  Group = -> [C_element038,H_element035]
  conduct = 2
  density = 1
  expand = 3
  formula = G4_ETHANE
  name = G4_ETHANE
  specific = 4
FEATURE [App::DocumentObjectGroupPython] C_element039  label="C_element : 023"  # scripted group (container) (typed FeaturePython)
  n = 2
  ref = C_element
FEATURE [App::DocumentObjectGroupPython] H_element036  label="H_element : 019"  # scripted group (container) (typed FeaturePython)
  n = 6
  ref = H_element
FEATURE [App::DocumentObjectGroupPython] O_element035  label="O_element : 018"  # scripted group (container) (typed FeaturePython)
  n = 1
  ref = O_element
FEATURE [App::DocumentObjectGroupPython] G4_ETHYL_ALCOHOL  # scripted group (container) (typed FeaturePython)
  Dunit = g/cm3
  Dvalue = 0.7893
  Group = -> [C_element039,H_element036,O_element035]
  conduct = 2
  density = 1
  expand = 3
  formula = G4_ETHYL_ALCOHOL
  name = G4_ETHYL_ALCOHOL
  specific = 4
FEATURE [App::DocumentObjectGroupPython] H_element037  label="H_element : 0.090"  # scripted group (container) (typed FeaturePython)
  n = 0.090027
FEATURE [App::DocumentObjectGroupPython] C_element040  label="C_element : 0.585"  # scripted group (container) (typed FeaturePython)
  n = 0.585182
FEATURE [App::DocumentObjectGroupPython] O_element036  label="O_element : 0.325"  # scripted group (container) (typed FeaturePython)
  n = 0.324791
FEATURE [App::DocumentObjectGroupPython] G4_ETHYL_CELLULOSE  # scripted group (container) (typed FeaturePython)
  Dunit = g/cm3
  Dvalue = 1.13
  Group = -> [H_element037,C_element040,O_element036]
  conduct = 2
  density = 1
  expand = 3
  formula = G4_ETHYL_CELLULOSE
  name = G4_ETHYL_CELLULOSE
  specific = 4
FEATURE [App::DocumentObjectGroupPython] C_element041  label="C_element : 024"  # scripted group (container) (typed FeaturePython)
  n = 2
  ref = C_element
FEATURE [App::DocumentObjectGroupPython] H_element038  label="H_element : 020"  # scripted group (container) (typed FeaturePython)
  n = 4
  ref = H_element
FEATURE [App::DocumentObjectGroupPython] G4_ETHYLENE  # scripted group (container) (typed FeaturePython)
  Dunit = g/cm3
  Dvalue = 0.00117497
  Group = -> [C_element041,H_element038]
  conduct = 2
  density = 1
  expand = 3
  formula = G4_ETHYLENE
  name = G4_ETHYLENE
  specific = 4
FEATURE [App::DocumentObjectGroupPython] H_element039  label="H_element : 0.096"  # scripted group (container) (typed FeaturePython)
  n = 0.096
FEATURE [App::DocumentObjectGroupPython] C_element042  label="C_element : 0.195"  # scripted group (container) (typed FeaturePython)
  n = 0.195
FEATURE [App::DocumentObjectGroupPython] N_element016  label="N_element : 0.057"  # scripted group (container) (typed FeaturePython)
  n = 0.057
FEATURE [App::DocumentObjectGroupPython] O_element037  label="O_element : 0.646"  # scripted group (container) (typed FeaturePython)
  n = 0.646
FEATURE [App::DocumentObjectGroupPython] Na_element006  label="Na_element : 0.017"  # scripted group (container) (typed FeaturePython)
  n = 0.001
FEATURE [App::DocumentObjectGroupPython] P_element005  label="P_element : 0.104"  # scripted group (container) (typed FeaturePython)
  n = 0.001
FEATURE [App::DocumentObjectGroupPython] S_element010  label="S_element : 0.016"  # scripted group (container) (typed FeaturePython)
  n = 0.003
FEATURE [App::DocumentObjectGroupPython] Cl_element010  label="Cl_element : 0.005"  # scripted group (container) (typed FeaturePython)
  n = 0.001
FEATURE [App::DocumentObjectGroupPython] G4_EYE_LENS_ICRP  # scripted group (container) (typed FeaturePython)
  Dunit = g/cm3
  Dvalue = 1.07
  Group = -> [H_element039,C_element042,N_element016,O_element037,Na_element006,P_element005,S_element010,Cl_element010]
  conduct = 2
  density = 1
  expand = 3
  formula = G4_EYE_LENS_ICRP
  name = G4_EYE_LENS_ICRP
  specific = 4
FEATURE [App::DocumentObjectGroupPython] Fe_element003  label="Fe_element : 2"  # scripted group (container) (typed FeaturePython)
  n = 2
  ref = Fe_element
FEATURE [App::DocumentObjectGroupPython] O_element038  label="O_element : 019"  # scripted group (container) (typed FeaturePython)
  n = 3
  ref = O_element
FEATURE [App::DocumentObjectGroupPython] G4_FERRIC_OXIDE  # scripted group (container) (typed FeaturePython)
  Dunit = g/cm3
  Dvalue = 5.2
  Group = -> [Fe_element003,O_element038]
  conduct = 2
  density = 1
  expand = 3
  formula = G4_FERRIC_OXIDE
  name = G4_FERRIC_OXIDE
  specific = 4
FEATURE [App::DocumentObjectGroupPython] Fe_element004  label="Fe_element : 1"  # scripted group (container) (typed FeaturePython)
  n = 1
  ref = Fe_element
FEATURE [App::DocumentObjectGroupPython] B_element003  label="B_element : 1"  # scripted group (container) (typed FeaturePython)
  n = 1
  ref = B_element
FEATURE [App::DocumentObjectGroupPython] G4_FERROBORIDE  # scripted group (container) (typed FeaturePython)
  Dunit = g/cm3
  Dvalue = 7.15
  Group = -> [Fe_element004,B_element003]
  conduct = 2
  density = 1
  expand = 3
  formula = G4_FERROBORIDE
  name = G4_FERROBORIDE
  specific = 4
FEATURE [App::DocumentObjectGroupPython] Fe_element005  label="Fe_element : 003"  # scripted group (container) (typed FeaturePython)
  n = 1
  ref = Fe_element
FEATURE [App::DocumentObjectGroupPython] O_element039  label="O_element : 020"  # scripted group (container) (typed FeaturePython)
  n = 1
  ref = O_element
FEATURE [App::DocumentObjectGroupPython] G4_FERROUS_OXIDE  # scripted group (container) (typed FeaturePython)
  Dunit = g/cm3
  Dvalue = 5.7
  Group = -> [Fe_element005,O_element039]
  conduct = 2
  density = 1
  expand = 3
  formula = G4_FERROUS_OXIDE
  name = G4_FERROUS_OXIDE
  specific = 4
FEATURE [App::DocumentObjectGroupPython] H_element040  label="H_element : 0.115"  # scripted group (container) (typed FeaturePython)
  n = 0.108259
FEATURE [App::DocumentObjectGroupPython] N_element017  label="N_element : 0.000"  # scripted group (container) (typed FeaturePython)
  n = 2.7e-05
FEATURE [App::DocumentObjectGroupPython] O_element040  label="O_element : 0.879"  # scripted group (container) (typed FeaturePython)
  n = 0.878636
FEATURE [App::DocumentObjectGroupPython] Na_element007  label="Na_element : 0.000"  # scripted group (container) (typed FeaturePython)
  n = 2.2e-05
FEATURE [App::DocumentObjectGroupPython] S_element011  label="S_element : 0.013"  # scripted group (container) (typed FeaturePython)
  n = 0.012968
FEATURE [App::DocumentObjectGroupPython] Cl_element011  label="Cl_element : 0.000"  # scripted group (container) (typed FeaturePython)
  n = 3.4e-05
FEATURE [App::DocumentObjectGroupPython] Fe_element006  label="Fe_element : 0.000"  # scripted group (container) (typed FeaturePython)
  n = 5.4e-05
FEATURE [App::DocumentObjectGroupPython] G4_FERROUS_SULFATE  # scripted group (container) (typed FeaturePython)
  Dunit = g/cm3
  Dvalue = 1.024
  Group = -> [H_element040,N_element017,O_element040,Na_element007,S_element011,Cl_element011,Fe_element006]
  conduct = 2
  density = 1
  expand = 3
  formula = G4_FERROUS_SULFATE
  name = G4_FERROUS_SULFATE
  specific = 4
FEATURE [App::DocumentObjectGroupPython] C_element043  label="C_element : 0.099"  # scripted group (container) (typed FeaturePython)
  n = 0.099335
FEATURE [App::DocumentObjectGroupPython] F_element007  label="F_element : 0.314"  # scripted group (container) (typed FeaturePython)
  n = 0.314247
FEATURE [App::DocumentObjectGroupPython] Cl_element012  label="Cl_element : 0.586"  # scripted group (container) (typed FeaturePython)
  n = 0.586418
FEATURE [App::DocumentObjectGroupPython] G4_FREON_12  label="G4_FREON-12"  # scripted group (container) (typed FeaturePython)
  Dunit = g/cm3
  Dvalue = 1.12
  Group = -> [C_element043,F_element007,Cl_element012]
  conduct = 2
  density = 1
  expand = 3
  formula = G4_FREON-12
  name = G4_FREON-12
  specific = 4
FEATURE [App::DocumentObjectGroupPython] C_element044  label="C_element : 0.057"  # scripted group (container) (typed FeaturePython)
  n = 0.057245
FEATURE [App::DocumentObjectGroupPython] F_element008  label="F_element : 0.181"  # scripted group (container) (typed FeaturePython)
  n = 0.181096
FEATURE [App::DocumentObjectGroupPython] Br_element001  label="Br_element : 0.762"  # scripted group (container) (typed FeaturePython)
  n = 0.761659
FEATURE [App::DocumentObjectGroupPython] G4_FREON_12B2  label="G4_FREON-12B2"  # scripted group (container) (typed FeaturePython)
  Dunit = g/cm3
  Dvalue = 1.8
  Group = -> [C_element044,F_element008,Br_element001]
  conduct = 2
  density = 1
  expand = 3
  formula = G4_FREON-12B2
  name = G4_FREON-12B2
  specific = 4
FEATURE [App::DocumentObjectGroupPython] C_element045  label="C_element : 0.115"  # scripted group (container) (typed FeaturePython)
  n = 0.114983
FEATURE [App::DocumentObjectGroupPython] F_element009  label="F_element : 0.546"  # scripted group (container) (typed FeaturePython)
  n = 0.545621
FEATURE [App::DocumentObjectGroupPython] Cl_element013  label="Cl_element : 0.339"  # scripted group (container) (typed FeaturePython)
  n = 0.339396
FEATURE [App::DocumentObjectGroupPython] G4_FREON_13  label="G4_FREON-13"  # scripted group (container) (typed FeaturePython)
  Dunit = g/cm3
  Dvalue = 0.95
  Group = -> [C_element045,F_element009,Cl_element013]
  conduct = 2
  density = 1
  expand = 3
  formula = G4_FREON-13
  name = G4_FREON-13
  specific = 4
FEATURE [App::DocumentObjectGroupPython] C_element046  label="C_element : 025"  # scripted group (container) (typed FeaturePython)
  n = 1
  ref = C_element
FEATURE [App::DocumentObjectGroupPython] F_element010  label="F_element : 3"  # scripted group (container) (typed FeaturePython)
  n = 3
  ref = F_element
FEATURE [App::DocumentObjectGroupPython] Br_element002  label="Br_element : 1"  # scripted group (container) (typed FeaturePython)
  n = 1
  ref = Br_element
FEATURE [App::DocumentObjectGroupPython] G4_FREON_13B1  label="G4_FREON-13B1"  # scripted group (container) (typed FeaturePython)
  Dunit = g/cm3
  Dvalue = 1.5
  Group = -> [C_element046,F_element010,Br_element002]
  conduct = 2
  density = 1
  expand = 3
  formula = G4_FREON-13B1
  name = G4_FREON-13B1
  specific = 4
FEATURE [App::DocumentObjectGroupPython] C_element047  label="C_element : 0.061"  # scripted group (container) (typed FeaturePython)
  n = 0.061309
FEATURE [App::DocumentObjectGroupPython] F_element011  label="F_element : 0.291"  # scripted group (container) (typed FeaturePython)
  n = 0.290924
FEATURE [App::DocumentObjectGroupPython] I_element002  label="I_element : 0.648"  # scripted group (container) (typed FeaturePython)
  n = 0.647767
FEATURE [App::DocumentObjectGroupPython] G4_FREON_13I1  label="G4_FREON-13I1"  # scripted group (container) (typed FeaturePython)
  Dunit = g/cm3
  Dvalue = 1.8
  Group = -> [C_element047,F_element011,I_element002]
  conduct = 2
  density = 1
  expand = 3
  formula = G4_FREON-13I1
  name = G4_FREON-13I1
  specific = 4
FEATURE [App::DocumentObjectGroupPython] Gd_element001  label="Gd_element : 2"  # scripted group (container) (typed FeaturePython)
  n = 2
  ref = Gd_element
FEATURE [App::DocumentObjectGroupPython] O_element041  label="O_element : 021"  # scripted group (container) (typed FeaturePython)
  n = 2
  ref = O_element
FEATURE [App::DocumentObjectGroupPython] S_element012  label="S_element : 004"  # scripted group (container) (typed FeaturePython)
  n = 1
  ref = S_element
FEATURE [App::DocumentObjectGroupPython] G4_GADOLINIUM_OXYSULFIDE  # scripted group (container) (typed FeaturePython)
  Dunit = g/cm3
  Dvalue = 7.44
  Group = -> [Gd_element001,O_element041,S_element012]
  conduct = 2
  density = 1
  expand = 3
  formula = G4_GADOLINIUM_OXYSULFIDE
  name = G4_GADOLINIUM_OXYSULFIDE
  specific = 4
FEATURE [App::DocumentObjectGroupPython] Ga_element001  label="Ga_element : 1"  # scripted group (container) (typed FeaturePython)
  n = 1
  ref = Ga_element
FEATURE [App::DocumentObjectGroupPython] As_element001  label="As_element : 1"  # scripted group (container) (typed FeaturePython)
  n = 1
  ref = As_element
FEATURE [App::DocumentObjectGroupPython] G4_GALLIUM_ARSENIDE  # scripted group (container) (typed FeaturePython)
  Dunit = g/cm3
  Dvalue = 5.31
  Group = -> [Ga_element001,As_element001]
  conduct = 2
  density = 1
  expand = 3
  formula = G4_GALLIUM_ARSENIDE
  name = G4_GALLIUM_ARSENIDE
  specific = 4
FEATURE [App::DocumentObjectGroupPython] H_element041  label="H_element : 0.081"  # scripted group (container) (typed FeaturePython)
  n = 0.08118
FEATURE [App::DocumentObjectGroupPython] C_element048  label="C_element : 0.416"  # scripted group (container) (typed FeaturePython)
  n = 0.41606
FEATURE [App::DocumentObjectGroupPython] N_element018  label="N_element : 0.111"  # scripted group (container) (typed FeaturePython)
  n = 0.11124
FEATURE [App::DocumentObjectGroupPython] O_element042  label="O_element : 0.381"  # scripted group (container) (typed FeaturePython)
  n = 0.38064
FEATURE [App::DocumentObjectGroupPython] S_element013  label="S_element : 0.011"  # scripted group (container) (typed FeaturePython)
  n = 0.01088
FEATURE [App::DocumentObjectGroupPython] G4_GEL_PHOTO_EMULSION  # scripted group (container) (typed FeaturePython)
  Dunit = g/cm3
  Dvalue = 1.2914
  Group = -> [H_element041,C_element048,N_element018,O_element042,S_element013]
  conduct = 2
  density = 1
  expand = 3
  formula = G4_GEL_PHOTO_EMULSION
  name = G4_GEL_PHOTO_EMULSION
  specific = 4
FEATURE [App::DocumentObjectGroupPython] B_element004  label="B_element : 0.040"  # scripted group (container) (typed FeaturePython)
  n = 0.0400639
FEATURE [App::DocumentObjectGroupPython] O_element043  label="O_element : 0.540"  # scripted group (container) (typed FeaturePython)
  n = 0.539561
FEATURE [App::DocumentObjectGroupPython] Na_element008  label="Na_element : 0.028"  # scripted group (container) (typed FeaturePython)
  n = 0.0281909
FEATURE [App::DocumentObjectGroupPython] Al_element003  label="Al_element : 0.012"  # scripted group (container) (typed FeaturePython)
  n = 0.011644
FEATURE [App::DocumentObjectGroupPython] Si_element003  label="Si_element : 0.377"  # scripted group (container) (typed FeaturePython)
  n = 0.377219
FEATURE [App::DocumentObjectGroupPython] K_element004  label="K_element : 0.014"  # scripted group (container) (typed FeaturePython)
  n = 0.00332099
FEATURE [App::DocumentObjectGroupPython] G4_Pyrex_Glass  # scripted group (container) (typed FeaturePython)
  Dunit = g/cm3
  Dvalue = 2.23
  Group = -> [B_element004,O_element043,Na_element008,Al_element003,Si_element003,K_element004]
  conduct = 2
  density = 1
  expand = 3
  formula = G4_Pyrex_Glass
  name = G4_Pyrex_Glass
  specific = 4
FEATURE [App::DocumentObjectGroupPython] O_element044  label="O_element : 0.156"  # scripted group (container) (typed FeaturePython)
  n = 0.156453
FEATURE [App::DocumentObjectGroupPython] Si_element004  label="Si_element : 0.081"  # scripted group (container) (typed FeaturePython)
  n = 0.080866
FEATURE [App::DocumentObjectGroupPython] Ti_element001  label="Ti_element : 0.008"  # scripted group (container) (typed FeaturePython)
  n = 0.008092
FEATURE [App::DocumentObjectGroupPython] As_element002  label="As_element : 0.003"  # scripted group (container) (typed FeaturePython)
  n = 0.002651
FEATURE [App::DocumentObjectGroupPython] Pb_element001  label="Pb_element : 0.752"  # scripted group (container) (typed FeaturePython)
  n = 0.751938
FEATURE [App::DocumentObjectGroupPython] G4_GLASS_LEAD  # scripted group (container) (typed FeaturePython)
  Dunit = g/cm3
  Dvalue = 6.22
  Group = -> [O_element044,Si_element004,Ti_element001,As_element002,Pb_element001]
  conduct = 2
  density = 1
  expand = 3
  formula = G4_GLASS_LEAD
  name = G4_GLASS_LEAD
  specific = 4
FEATURE [App::DocumentObjectGroupPython] O_element045  label="O_element : 0.460"  # scripted group (container) (typed FeaturePython)
  n = 0.4598
FEATURE [App::DocumentObjectGroupPython] Na_element009  label="Na_element : 0.096"  # scripted group (container) (typed FeaturePython)
  n = 0.0964411
FEATURE [App::DocumentObjectGroupPython] Si_element005  label="Si_element : 0.378"  # scripted group (container) (typed FeaturePython)
  n = 0.336553
FEATURE [App::DocumentObjectGroupPython] Ca_element011  label="Ca_element : 0.107"  # scripted group (container) (typed FeaturePython)
  n = 0.107205
FEATURE [App::DocumentObjectGroupPython] G4_GLASS_PLATE  # scripted group (container) (typed FeaturePython)
  Dunit = g/cm3
  Dvalue = 2.4
  Group = -> [O_element045,Na_element009,Si_element005,Ca_element011]
  conduct = 2
  density = 1
  expand = 3
  formula = G4_GLASS_PLATE
  name = G4_GLASS_PLATE
  specific = 4
FEATURE [App::DocumentObjectGroupPython] C_element049  label="C_element : 026"  # scripted group (container) (typed FeaturePython)
  n = 5
  ref = C_element
FEATURE [App::DocumentObjectGroupPython] H_element042  label="H_element : 021"  # scripted group (container) (typed FeaturePython)
  n = 10
  ref = H_element
FEATURE [App::DocumentObjectGroupPython] N_element019  label="N_element : 2"  # scripted group (container) (typed FeaturePython)
  n = 2
  ref = N_element
FEATURE [App::DocumentObjectGroupPython] O_element046  label="O_element : 022"  # scripted group (container) (typed FeaturePython)
  n = 3
  ref = O_element
FEATURE [App::DocumentObjectGroupPython] G4_GLUTAMINE  # scripted group (container) (typed FeaturePython)
  Dunit = g/cm3
  Dvalue = 1.46
  Group = -> [C_element049,H_element042,N_element019,O_element046]
  conduct = 2
  density = 1
  expand = 3
  formula = G4_GLUTAMINE
  name = G4_GLUTAMINE
  specific = 4
FEATURE [App::DocumentObjectGroupPython] C_element050  label="C_element : 027"  # scripted group (container) (typed FeaturePython)
  n = 3
  ref = C_element
FEATURE [App::DocumentObjectGroupPython] H_element043  label="H_element : 022"  # scripted group (container) (typed FeaturePython)
  n = 8
  ref = H_element
FEATURE [App::DocumentObjectGroupPython] O_element047  label="O_element : 023"  # scripted group (container) (typed FeaturePython)
  n = 3
  ref = O_element
FEATURE [App::DocumentObjectGroupPython] G4_GLYCEROL  # scripted group (container) (typed FeaturePython)
  Dunit = g/cm3
  Dvalue = 1.2613
  Group = -> [C_element050,H_element043,O_element047]
  conduct = 2
  density = 1
  expand = 3
  formula = G4_GLYCEROL
  name = G4_GLYCEROL
  specific = 4
FEATURE [App::DocumentObjectGroupPython] C_element051  label="C_element : 028"  # scripted group (container) (typed FeaturePython)
  n = 5
  ref = C_element
FEATURE [App::DocumentObjectGroupPython] H_element044  label="H_element : 023"  # scripted group (container) (typed FeaturePython)
  n = 5
  ref = H_element
FEATURE [App::DocumentObjectGroupPython] N_element020  label="N_element : 009"  # scripted group (container) (typed FeaturePython)
  n = 5
  ref = N_element
FEATURE [App::DocumentObjectGroupPython] O_element048  label="O_element : 024"  # scripted group (container) (typed FeaturePython)
  n = 1
  ref = O_element
FEATURE [App::DocumentObjectGroupPython] G4_GUANINE  # scripted group (container) (typed FeaturePython)
  Dunit = g/cm3
  Dvalue = 2.2
  Group = -> [C_element051,H_element044,N_element020,O_element048]
  conduct = 2
  density = 1
  expand = 3
  formula = G4_GUANINE
  name = G4_GUANINE
  specific = 4
FEATURE [App::DocumentObjectGroupPython] Ca_element012  label="Ca_element : 006"  # scripted group (container) (typed FeaturePython)
  n = 1
  ref = Ca_element
FEATURE [App::DocumentObjectGroupPython] S_element014  label="S_element : 005"  # scripted group (container) (typed FeaturePython)
  n = 1
  ref = S_element
FEATURE [App::DocumentObjectGroupPython] O_element049  label="O_element : 6"  # scripted group (container) (typed FeaturePython)
  n = 6
  ref = O_element
FEATURE [App::DocumentObjectGroupPython] H_element045  label="H_element : 024"  # scripted group (container) (typed FeaturePython)
  n = 4
  ref = H_element
FEATURE [App::DocumentObjectGroupPython] G4_GYPSUM  # scripted group (container) (typed FeaturePython)
  Dunit = g/cm3
  Dvalue = 2.32
  Group = -> [Ca_element012,S_element014,O_element049,H_element045]
  conduct = 2
  density = 1
  expand = 3
  formula = G4_GYPSUM
  name = G4_GYPSUM
  specific = 4
FEATURE [App::DocumentObjectGroupPython] C_element052  label="C_element : 7"  # scripted group (container) (typed FeaturePython)
  n = 7
  ref = C_element
FEATURE [App::DocumentObjectGroupPython] H_element046  label="H_element : 16"  # scripted group (container) (typed FeaturePython)
  n = 16
  ref = H_element
FEATURE [App::DocumentObjectGroupPython] G4_N_HEPTANE  label="G4_N-HEPTANE"  # scripted group (container) (typed FeaturePython)
  Dunit = g/cm3
  Dvalue = 0.68376
  Group = -> [C_element052,H_element046]
  conduct = 2
  density = 1
  expand = 3
  formula = G4_N-HEPTANE
  name = G4_N-HEPTANE
  specific = 4
FEATURE [App::DocumentObjectGroupPython] C_element053  label="C_element : 029"  # scripted group (container) (typed FeaturePython)
  n = 6
  ref = C_element
FEATURE [App::DocumentObjectGroupPython] H_element047  label="H_element : 14"  # scripted group (container) (typed FeaturePython)
  n = 14
  ref = H_element
FEATURE [App::DocumentObjectGroupPython] G4_N_HEXANE  label="G4_N-HEXANE"  # scripted group (container) (typed FeaturePython)
  Dunit = g/cm3
  Dvalue = 0.6603
  Group = -> [C_element053,H_element047]
  conduct = 2
  density = 1
  expand = 3
  formula = G4_N-HEXANE
  name = G4_N-HEXANE
  specific = 4
FEATURE [App::DocumentObjectGroupPython] C_element054  label="C_element : 22"  # scripted group (container) (typed FeaturePython)
  n = 22
  ref = C_element
FEATURE [App::DocumentObjectGroupPython] H_element048  label="H_element : 025"  # scripted group (container) (typed FeaturePython)
  n = 10
  ref = H_element
FEATURE [App::DocumentObjectGroupPython] N_element021  label="N_element : 010"  # scripted group (container) (typed FeaturePython)
  n = 2
  ref = N_element
FEATURE [App::DocumentObjectGroupPython] O_element050  label="O_element : 025"  # scripted group (container) (typed FeaturePython)
  n = 5
  ref = O_element
FEATURE [App::DocumentObjectGroupPython] G4_KAPTON  # scripted group (container) (typed FeaturePython)
  Dunit = g/cm3
  Dvalue = 1.42
  Group = -> [C_element054,H_element048,N_element021,O_element050]
  conduct = 2
  density = 1
  expand = 3
  formula = G4_KAPTON
  name = G4_KAPTON
  specific = 4
FEATURE [App::DocumentObjectGroupPython] La_element001  label="La_element : 1"  # scripted group (container) (typed FeaturePython)
  n = 1
  ref = La_element
FEATURE [App::DocumentObjectGroupPython] Br_element003  label="Br_element : 002"  # scripted group (container) (typed FeaturePython)
  n = 1
  ref = Br_element
FEATURE [App::DocumentObjectGroupPython] O_element051  label="O_element : 026"  # scripted group (container) (typed FeaturePython)
  n = 1
  ref = O_element
FEATURE [App::DocumentObjectGroupPython] G4_LANTHANUM_OXYBROMIDE  # scripted group (container) (typed FeaturePython)
  Dunit = g/cm3
  Dvalue = 6.28
  Group = -> [La_element001,Br_element003,O_element051]
  conduct = 2
  density = 1
  expand = 3
  formula = G4_LANTHANUM_OXYBROMIDE
  name = G4_LANTHANUM_OXYBROMIDE
  specific = 4
FEATURE [App::DocumentObjectGroupPython] La_element002  label="La_element : 2"  # scripted group (container) (typed FeaturePython)
  n = 2
  ref = La_element
FEATURE [App::DocumentObjectGroupPython] O_element052  label="O_element : 027"  # scripted group (container) (typed FeaturePython)
  n = 2
  ref = O_element
FEATURE [App::DocumentObjectGroupPython] S_element015  label="S_element : 006"  # scripted group (container) (typed FeaturePython)
  n = 1
  ref = S_element
FEATURE [App::DocumentObjectGroupPython] G4_LANTHANUM_OXYSULFIDE  # scripted group (container) (typed FeaturePython)
  Dunit = g/cm3
  Dvalue = 5.86
  Group = -> [La_element002,O_element052,S_element015]
  conduct = 2
  density = 1
  expand = 3
  formula = G4_LANTHANUM_OXYSULFIDE
  name = G4_LANTHANUM_OXYSULFIDE
  specific = 4
FEATURE [App::DocumentObjectGroupPython] O_element053  label="O_element : 0.072"  # scripted group (container) (typed FeaturePython)
  n = 0.071682
FEATURE [App::DocumentObjectGroupPython] Pb_element002  label="Pb_element : 0.928"  # scripted group (container) (typed FeaturePython)
  n = 0.928318
FEATURE [App::DocumentObjectGroupPython] G4_LEAD_OXIDE  # scripted group (container) (typed FeaturePython)
  Dunit = g/cm3
  Dvalue = 9.53
  Group = -> [O_element053,Pb_element002]
  conduct = 2
  density = 1
  expand = 3
  formula = G4_LEAD_OXIDE
  name = G4_LEAD_OXIDE
  specific = 4
FEATURE [App::DocumentObjectGroupPython] Li_element001  label="Li_element : 1"  # scripted group (container) (typed FeaturePython)
  n = 1
  ref = Li_element
FEATURE [App::DocumentObjectGroupPython] N_element022  label="N_element : 011"  # scripted group (container) (typed FeaturePython)
  n = 1
  ref = N_element
FEATURE [App::DocumentObjectGroupPython] H_element049  label="H_element : 026"  # scripted group (container) (typed FeaturePython)
  n = 2
  ref = H_element
FEATURE [App::DocumentObjectGroupPython] G4_LITHIUM_AMIDE  # scripted group (container) (typed FeaturePython)
  Dunit = g/cm3
  Dvalue = 1.178
  Group = -> [Li_element001,N_element022,H_element049]
  conduct = 2
  density = 1
  expand = 3
  formula = G4_LITHIUM_AMIDE
  name = G4_LITHIUM_AMIDE
  specific = 4
FEATURE [App::DocumentObjectGroupPython] Li_element002  label="Li_element : 2"  # scripted group (container) (typed FeaturePython)
  n = 2
  ref = Li_element
FEATURE [App::DocumentObjectGroupPython] C_element055  label="C_element : 030"  # scripted group (container) (typed FeaturePython)
  n = 1
  ref = C_element
FEATURE [App::DocumentObjectGroupPython] O_element054  label="O_element : 028"  # scripted group (container) (typed FeaturePython)
  n = 3
  ref = O_element
FEATURE [App::DocumentObjectGroupPython] G4_LITHIUM_CARBONATE  # scripted group (container) (typed FeaturePython)
  Dunit = g/cm3
  Dvalue = 2.11
  Group = -> [Li_element002,C_element055,O_element054]
  conduct = 2
  density = 1
  expand = 3
  formula = G4_LITHIUM_CARBONATE
  name = G4_LITHIUM_CARBONATE
  specific = 4
FEATURE [App::DocumentObjectGroupPython] Li_element003  label="Li_element : 003"  # scripted group (container) (typed FeaturePython)
  n = 1
  ref = Li_element
FEATURE [App::DocumentObjectGroupPython] F_element012  label="F_element : 004"  # scripted group (container) (typed FeaturePython)
  n = 1
  ref = F_element
FEATURE [App::DocumentObjectGroupPython] G4_LITHIUM_FLUORIDE  # scripted group (container) (typed FeaturePython)
  Dunit = g/cm3
  Dvalue = 2.635
  Group = -> [Li_element003,F_element012]
  conduct = 2
  density = 1
  expand = 3
  formula = G4_LITHIUM_FLUORIDE
  name = G4_LITHIUM_FLUORIDE
  specific = 4
FEATURE [App::DocumentObjectGroupPython] Li_element004  label="Li_element : 004"  # scripted group (container) (typed FeaturePython)
  n = 1
  ref = Li_element
FEATURE [App::DocumentObjectGroupPython] H_element050  label="H_element : 027"  # scripted group (container) (typed FeaturePython)
  n = 1
  ref = H_element
FEATURE [App::DocumentObjectGroupPython] G4_LITHIUM_HYDRIDE  # scripted group (container) (typed FeaturePython)
  Dunit = g/cm3
  Dvalue = 0.82
  Group = -> [Li_element004,H_element050]
  conduct = 2
  density = 1
  expand = 3
  formula = G4_LITHIUM_HYDRIDE
  name = G4_LITHIUM_HYDRIDE
  specific = 4
FEATURE [App::DocumentObjectGroupPython] Li_element005  label="Li_element : 005"  # scripted group (container) (typed FeaturePython)
  n = 1
  ref = Li_element
FEATURE [App::DocumentObjectGroupPython] I_element003  label="I_element : 002"  # scripted group (container) (typed FeaturePython)
  n = 1
  ref = I_element
FEATURE [App::DocumentObjectGroupPython] G4_LITHIUM_IODIDE  # scripted group (container) (typed FeaturePython)
  Dunit = g/cm3
  Dvalue = 3.494
  Group = -> [Li_element005,I_element003]
  conduct = 2
  density = 1
  expand = 3
  formula = G4_LITHIUM_IODIDE
  name = G4_LITHIUM_IODIDE
  specific = 4
FEATURE [App::DocumentObjectGroupPython] Li_element006  label="Li_element : 006"  # scripted group (container) (typed FeaturePython)
  n = 2
  ref = Li_element
FEATURE [App::DocumentObjectGroupPython] O_element055  label="O_element : 029"  # scripted group (container) (typed FeaturePython)
  n = 1
  ref = O_element
FEATURE [App::DocumentObjectGroupPython] G4_LITHIUM_OXIDE  # scripted group (container) (typed FeaturePython)
  Dunit = g/cm3
  Dvalue = 2.013
  Group = -> [Li_element006,O_element055]
  conduct = 2
  density = 1
  expand = 3
  formula = G4_LITHIUM_OXIDE
  name = G4_LITHIUM_OXIDE
  specific = 4
FEATURE [App::DocumentObjectGroupPython] Li_element007  label="Li_element : 007"  # scripted group (container) (typed FeaturePython)
  n = 2
  ref = Li_element
FEATURE [App::DocumentObjectGroupPython] B_element005  label="B_element : 005"  # scripted group (container) (typed FeaturePython)
  n = 4
  ref = B_element
FEATURE [App::DocumentObjectGroupPython] O_element056  label="O_element : 7"  # scripted group (container) (typed FeaturePython)
  n = 7
  ref = O_element
FEATURE [App::DocumentObjectGroupPython] G4_LITHIUM_TETRABORATE  # scripted group (container) (typed FeaturePython)
  Dunit = g/cm3
  Dvalue = 2.44
  Group = -> [Li_element007,B_element005,O_element056]
  conduct = 2
  density = 1
  expand = 3
  formula = G4_LITHIUM_TETRABORATE
  name = G4_LITHIUM_TETRABORATE
  specific = 4
FEATURE [App::DocumentObjectGroupPython] H_element051  label="H_element : 0.105"  # scripted group (container) (typed FeaturePython)
  n = 0.105
FEATURE [App::DocumentObjectGroupPython] C_element056  label="C_element : 0.083"  # scripted group (container) (typed FeaturePython)
  n = 0.083
FEATURE [App::DocumentObjectGroupPython] N_element023  label="N_element : 0.023"  # scripted group (container) (typed FeaturePython)
  n = 0.023
FEATURE [App::DocumentObjectGroupPython] O_element057  label="O_element : 0.779"  # scripted group (container) (typed FeaturePython)
  n = 0.779
FEATURE [App::DocumentObjectGroupPython] Na_element010  label="Na_element : 0.097"  # scripted group (container) (typed FeaturePython)
  n = 0.002
FEATURE [App::DocumentObjectGroupPython] P_element006  label="P_element : 0.105"  # scripted group (container) (typed FeaturePython)
  n = 0.001
FEATURE [App::DocumentObjectGroupPython] S_element016  label="S_element : 0.017"  # scripted group (container) (typed FeaturePython)
  n = 0.002
FEATURE [App::DocumentObjectGroupPython] Cl_element014  label="Cl_element : 0.587"  # scripted group (container) (typed FeaturePython)
  n = 0.003
FEATURE [App::DocumentObjectGroupPython] K_element005  label="K_element : 0.015"  # scripted group (container) (typed FeaturePython)
  n = 0.002
FEATURE [App::DocumentObjectGroupPython] G4_LUNG_ICRP  # scripted group (container) (typed FeaturePython)
  Dunit = g/cm3
  Dvalue = 1.04
  Group = -> [H_element051,C_element056,N_element023,O_element057,Na_element010,P_element006,S_element016,Cl_element014,K_element005]
  conduct = 2
  density = 1
  expand = 3
  formula = G4_LUNG_ICRP
  name = G4_LUNG_ICRP
  specific = 4
FEATURE [App::DocumentObjectGroupPython] H_element052  label="H_element : 0.116"  # scripted group (container) (typed FeaturePython)
  n = 0.114318
FEATURE [App::DocumentObjectGroupPython] C_element057  label="C_element : 0.656"  # scripted group (container) (typed FeaturePython)
  n = 0.655824
FEATURE [App::DocumentObjectGroupPython] O_element058  label="O_element : 0.092"  # scripted group (container) (typed FeaturePython)
  n = 0.0921831
FEATURE [App::DocumentObjectGroupPython] Mg_element004  label="Mg_element : 0.135"  # scripted group (container) (typed FeaturePython)
  n = 0.134792
FEATURE [App::DocumentObjectGroupPython] Ca_element013  label="Ca_element : 0.003"  # scripted group (container) (typed FeaturePython)
  n = 0.002883
FEATURE [App::DocumentObjectGroupPython] G4_M3_WAX  # scripted group (container) (typed FeaturePython)
  Dunit = g/cm3
  Dvalue = 1.05
  Group = -> [H_element052,C_element057,O_element058,Mg_element004,Ca_element013]
  conduct = 2
  density = 1
  expand = 3
  formula = G4_M3_WAX
  name = G4_M3_WAX
  specific = 4
FEATURE [App::DocumentObjectGroupPython] Mg_element005  label="Mg_element : 1"  # scripted group (container) (typed FeaturePython)
  n = 1
  ref = Mg_element
FEATURE [App::DocumentObjectGroupPython] C_element058  label="C_element : 031"  # scripted group (container) (typed FeaturePython)
  n = 1
  ref = C_element
FEATURE [App::DocumentObjectGroupPython] O_element059  label="O_element : 030"  # scripted group (container) (typed FeaturePython)
  n = 3
  ref = O_element
FEATURE [App::DocumentObjectGroupPython] G4_MAGNESIUM_CARBONATE  # scripted group (container) (typed FeaturePython)
  Dunit = g/cm3
  Dvalue = 2.958
  Group = -> [Mg_element005,C_element058,O_element059]
  conduct = 2
  density = 1
  expand = 3
  formula = G4_MAGNESIUM_CARBONATE
  name = G4_MAGNESIUM_CARBONATE
  specific = 4
FEATURE [App::DocumentObjectGroupPython] Mg_element006  label="Mg_element : 002"  # scripted group (container) (typed FeaturePython)
  n = 1
  ref = Mg_element
FEATURE [App::DocumentObjectGroupPython] F_element013  label="F_element : 005"  # scripted group (container) (typed FeaturePython)
  n = 2
  ref = F_element
FEATURE [App::DocumentObjectGroupPython] G4_MAGNESIUM_FLUORIDE  # scripted group (container) (typed FeaturePython)
  Dunit = g/cm3
  Dvalue = 3
  Group = -> [Mg_element006,F_element013]
  conduct = 2
  density = 1
  expand = 3
  formula = G4_MAGNESIUM_FLUORIDE
  name = G4_MAGNESIUM_FLUORIDE
  specific = 4
FEATURE [App::DocumentObjectGroupPython] Mg_element007  label="Mg_element : 003"  # scripted group (container) (typed FeaturePython)
  n = 1
  ref = Mg_element
FEATURE [App::DocumentObjectGroupPython] O_element060  label="O_element : 031"  # scripted group (container) (typed FeaturePython)
  n = 1
  ref = O_element
FEATURE [App::DocumentObjectGroupPython] G4_MAGNESIUM_OXIDE  # scripted group (container) (typed FeaturePython)
  Dunit = g/cm3
  Dvalue = 3.58
  Group = -> [Mg_element007,O_element060]
  conduct = 2
  density = 1
  expand = 3
  formula = G4_MAGNESIUM_OXIDE
  name = G4_MAGNESIUM_OXIDE
  specific = 4
FEATURE [App::DocumentObjectGroupPython] Mg_element008  label="Mg_element : 004"  # scripted group (container) (typed FeaturePython)
  n = 1
  ref = Mg_element
FEATURE [App::DocumentObjectGroupPython] B_element006  label="B_element : 006"  # scripted group (container) (typed FeaturePython)
  n = 4
  ref = B_element
FEATURE [App::DocumentObjectGroupPython] O_element061  label="O_element : 032"  # scripted group (container) (typed FeaturePython)
  n = 7
  ref = O_element
FEATURE [App::DocumentObjectGroupPython] G4_MAGNESIUM_TETRABORATE  # scripted group (container) (typed FeaturePython)
  Dunit = g/cm3
  Dvalue = 2.53
  Group = -> [Mg_element008,B_element006,O_element061]
  conduct = 2
  density = 1
  expand = 3
  formula = G4_MAGNESIUM_TETRABORATE
  name = G4_MAGNESIUM_TETRABORATE
  specific = 4
FEATURE [App::DocumentObjectGroupPython] Hg_element001  label="Hg_element : 1"  # scripted group (container) (typed FeaturePython)
  n = 1
  ref = Hg_element
FEATURE [App::DocumentObjectGroupPython] I_element004  label="I_element : 2"  # scripted group (container) (typed FeaturePython)
  n = 2
  ref = I_element
FEATURE [App::DocumentObjectGroupPython] G4_MERCURIC_IODIDE  # scripted group (container) (typed FeaturePython)
  Dunit = g/cm3
  Dvalue = 6.36
  Group = -> [Hg_element001,I_element004]
  conduct = 2
  density = 1
  expand = 3
  formula = G4_MERCURIC_IODIDE
  name = G4_MERCURIC_IODIDE
  specific = 4
FEATURE [App::DocumentObjectGroupPython] C_element059  label="C_element : 032"  # scripted group (container) (typed FeaturePython)
  n = 1
  ref = C_element
FEATURE [App::DocumentObjectGroupPython] H_element053  label="H_element : 028"  # scripted group (container) (typed FeaturePython)
  n = 4
  ref = H_element
FEATURE [App::DocumentObjectGroupPython] G4_METHANE  # scripted group (container) (typed FeaturePython)
  Dunit = g/cm3
  Dvalue = 0.000667151
  Group = -> [C_element059,H_element053]
  conduct = 2
  density = 1
  expand = 3
  formula = G4_METHANE
  name = G4_METHANE
  specific = 4
FEATURE [App::DocumentObjectGroupPython] C_element060  label="C_element : 033"  # scripted group (container) (typed FeaturePython)
  n = 1
  ref = C_element
FEATURE [App::DocumentObjectGroupPython] H_element054  label="H_element : 029"  # scripted group (container) (typed FeaturePython)
  n = 4
  ref = H_element
FEATURE [App::DocumentObjectGroupPython] O_element062  label="O_element : 033"  # scripted group (container) (typed FeaturePython)
  n = 1
  ref = O_element
FEATURE [App::DocumentObjectGroupPython] G4_METHANOL  # scripted group (container) (typed FeaturePython)
  Dunit = g/cm3
  Dvalue = 0.7914
  Group = -> [C_element060,H_element054,O_element062]
  conduct = 2
  density = 1
  expand = 3
  formula = G4_METHANOL
  name = G4_METHANOL
  specific = 4
FEATURE [App::DocumentObjectGroupPython] H_element055  label="H_element : 0.134"  # scripted group (container) (typed FeaturePython)
  n = 0.13404
FEATURE [App::DocumentObjectGroupPython] C_element061  label="C_element : 0.778"  # scripted group (container) (typed FeaturePython)
  n = 0.77796
FEATURE [App::DocumentObjectGroupPython] O_element063  label="O_element : 0.035"  # scripted group (container) (typed FeaturePython)
  n = 0.03502
FEATURE [App::DocumentObjectGroupPython] Mg_element009  label="Mg_element : 0.039"  # scripted group (container) (typed FeaturePython)
  n = 0.038594
FEATURE [App::DocumentObjectGroupPython] Ti_element002  label="Ti_element : 0.014"  # scripted group (container) (typed FeaturePython)
  n = 0.014386
FEATURE [App::DocumentObjectGroupPython] G4_MIX_D_WAX  # scripted group (container) (typed FeaturePython)
  Dunit = g/cm3
  Dvalue = 0.99
  Group = -> [H_element055,C_element061,O_element063,Mg_element009,Ti_element002]
  conduct = 2
  density = 1
  expand = 3
  formula = G4_MIX_D_WAX
  name = G4_MIX_D_WAX
  specific = 4
FEATURE [App::DocumentObjectGroupPython] H_element056  label="H_element : 0.135"  # scripted group (container) (typed FeaturePython)
  n = 0.081192
FEATURE [App::DocumentObjectGroupPython] C_element062  label="C_element : 0.583"  # scripted group (container) (typed FeaturePython)
  n = 0.583442
FEATURE [App::DocumentObjectGroupPython] N_element024  label="N_element : 0.018"  # scripted group (container) (typed FeaturePython)
  n = 0.017798
FEATURE [App::DocumentObjectGroupPython] O_element064  label="O_element : 0.186"  # scripted group (container) (typed FeaturePython)
  n = 0.186381
FEATURE [App::DocumentObjectGroupPython] Mg_element010  label="Mg_element : 0.130"  # scripted group (container) (typed FeaturePython)
  n = 0.130287
FEATURE [App::DocumentObjectGroupPython] Cl_element015  label="Cl_element : 0.588"  # scripted group (container) (typed FeaturePython)
  n = 0.0009
FEATURE [App::DocumentObjectGroupPython] G4_MS20_TISSUE  # scripted group (container) (typed FeaturePython)
  Dunit = g/cm3
  Dvalue = 1
  Group = -> [H_element056,C_element062,N_element024,O_element064,Mg_element010,Cl_element015]
  conduct = 2
  density = 1
  expand = 3
  formula = G4_MS20_TISSUE
  name = G4_MS20_TISSUE
  specific = 4
FEATURE [App::DocumentObjectGroupPython] H_element057  label="H_element : 0.136"  # scripted group (container) (typed FeaturePython)
  n = 0.102
FEATURE [App::DocumentObjectGroupPython] C_element063  label="C_element : 0.143"  # scripted group (container) (typed FeaturePython)
  n = 0.143
FEATURE [App::DocumentObjectGroupPython] N_element025  label="N_element : 0.034"  # scripted group (container) (typed FeaturePython)
  n = 0.034
FEATURE [App::DocumentObjectGroupPython] O_element065  label="O_element : 0.710"  # scripted group (container) (typed FeaturePython)
  n = 0.71
FEATURE [App::DocumentObjectGroupPython] Na_element011  label="Na_element : 0.098"  # scripted group (container) (typed FeaturePython)
  n = 0.001
FEATURE [App::DocumentObjectGroupPython] P_element007  label="P_element : 0.002"  # scripted group (container) (typed FeaturePython)
  n = 0.002
FEATURE [App::DocumentObjectGroupPython] S_element017  label="S_element : 0.018"  # scripted group (container) (typed FeaturePython)
  n = 0.003
FEATURE [App::DocumentObjectGroupPython] Cl_element016  label="Cl_element : 0.589"  # scripted group (container) (typed FeaturePython)
  n = 0.001
FEATURE [App::DocumentObjectGroupPython] K_element006  label="K_element : 0.004"  # scripted group (container) (typed FeaturePython)
  n = 0.004
FEATURE [App::DocumentObjectGroupPython] G4_MUSCLE_SKELETAL_ICRP  # scripted group (container) (typed FeaturePython)
  Dunit = g/cm3
  Dvalue = 1.05
  Group = -> [H_element057,C_element063,N_element025,O_element065,Na_element011,P_element007,S_element017,Cl_element016,K_element006]
  conduct = 2
  density = 1
  expand = 3
  formula = G4_MUSCLE_SKELETAL_ICRP
  name = G4_MUSCLE_SKELETAL_ICRP
  specific = 4
FEATURE [App::DocumentObjectGroupPython] H_element058  label="H_element : 0.137"  # scripted group (container) (typed FeaturePython)
  n = 0.102102
FEATURE [App::DocumentObjectGroupPython] C_element064  label="C_element : 0.123"  # scripted group (container) (typed FeaturePython)
  n = 0.123123
FEATURE [App::DocumentObjectGroupPython] N_element026  label="N_element : 0.756"  # scripted group (container) (typed FeaturePython)
  n = 0.035035
FEATURE [App::DocumentObjectGroupPython] O_element066  label="O_element : 0.730"  # scripted group (container) (typed FeaturePython)
  n = 0.72973
FEATURE [App::DocumentObjectGroupPython] Na_element012  label="Na_element : 0.099"  # scripted group (container) (typed FeaturePython)
  n = 0.001001
FEATURE [App::DocumentObjectGroupPython] P_element008  label="P_element : 0.106"  # scripted group (container) (typed FeaturePython)
  n = 0.002002
FEATURE [App::DocumentObjectGroupPython] S_element018  label="S_element : 0.019"  # scripted group (container) (typed FeaturePython)
  n = 0.004004
FEATURE [App::DocumentObjectGroupPython] K_element007  label="K_element : 0.016"  # scripted group (container) (typed FeaturePython)
  n = 0.003003
FEATURE [App::DocumentObjectGroupPython] G4_MUSCLE_STRIATED_ICRU  # scripted group (container) (typed FeaturePython)
  Dunit = g/cm3
  Dvalue = 1.04
  Group = -> [H_element058,C_element064,N_element026,O_element066,Na_element012,P_element008,S_element018,K_element007]
  conduct = 2
  density = 1
  expand = 3
  formula = G4_MUSCLE_STRIATED_ICRU
  name = G4_MUSCLE_STRIATED_ICRU
  specific = 4
FEATURE [App::DocumentObjectGroupPython] H_element059  label="H_element : 0.098"  # scripted group (container) (typed FeaturePython)
  n = 0.0982341
FEATURE [App::DocumentObjectGroupPython] C_element065  label="C_element : 0.156"  # scripted group (container) (typed FeaturePython)
  n = 0.156214
FEATURE [App::DocumentObjectGroupPython] N_element027  label="N_element : 0.757"  # scripted group (container) (typed FeaturePython)
  n = 0.035451
FEATURE [App::DocumentObjectGroupPython] O_element067  label="O_element : 0.880"  # scripted group (container) (typed FeaturePython)
  n = 0.710101
FEATURE [App::DocumentObjectGroupPython] G4_MUSCLE_WITH_SUCROSE  # scripted group (container) (typed FeaturePython)
  Dunit = g/cm3
  Dvalue = 1.11
  Group = -> [H_element059,C_element065,N_element027,O_element067]
  conduct = 2
  density = 1
  expand = 3
  formula = G4_MUSCLE_WITH_SUCROSE
  name = G4_MUSCLE_WITH_SUCROSE
  specific = 4
FEATURE [App::DocumentObjectGroupPython] H_element060  label="H_element : 0.138"  # scripted group (container) (typed FeaturePython)
  n = 0.101969
FEATURE [App::DocumentObjectGroupPython] C_element066  label="C_element : 0.120"  # scripted group (container) (typed FeaturePython)
  n = 0.120058
FEATURE [App::DocumentObjectGroupPython] N_element028  label="N_element : 0.758"  # scripted group (container) (typed FeaturePython)
  n = 0.035451
FEATURE [App::DocumentObjectGroupPython] O_element068  label="O_element : 0.743"  # scripted group (container) (typed FeaturePython)
  n = 0.742522
FEATURE [App::DocumentObjectGroupPython] G4_MUSCLE_WITHOUT_SUCROSE  # scripted group (container) (typed FeaturePython)
  Dunit = g/cm3
  Dvalue = 1.07
  Group = -> [H_element060,C_element066,N_element028,O_element068]
  conduct = 2
  density = 1
  expand = 3
  formula = G4_MUSCLE_WITHOUT_SUCROSE
  name = G4_MUSCLE_WITHOUT_SUCROSE
  specific = 4
FEATURE [App::DocumentObjectGroupPython] C_element067  label="C_element : 10"  # scripted group (container) (typed FeaturePython)
  n = 10
  ref = C_element
FEATURE [App::DocumentObjectGroupPython] H_element061  label="H_element : 030"  # scripted group (container) (typed FeaturePython)
  n = 8
  ref = H_element
FEATURE [App::DocumentObjectGroupPython] G4_NAPHTHALENE  # scripted group (container) (typed FeaturePython)
  Dunit = g/cm3
  Dvalue = 1.145
  Group = -> [C_element067,H_element061]
  conduct = 2
  density = 1
  expand = 3
  formula = G4_NAPHTHALENE
  name = G4_NAPHTHALENE
  specific = 4
FEATURE [App::DocumentObjectGroupPython] C_element068  label="C_element : 034"  # scripted group (container) (typed FeaturePython)
  n = 6
  ref = C_element
FEATURE [App::DocumentObjectGroupPython] H_element062  label="H_element : 031"  # scripted group (container) (typed FeaturePython)
  n = 5
  ref = H_element
FEATURE [App::DocumentObjectGroupPython] N_element029  label="N_element : 012"  # scripted group (container) (typed FeaturePython)
  n = 1
  ref = N_element
FEATURE [App::DocumentObjectGroupPython] O_element069  label="O_element : 034"  # scripted group (container) (typed FeaturePython)
  n = 2
  ref = O_element
FEATURE [App::DocumentObjectGroupPython] G4_NITROBENZENE  # scripted group (container) (typed FeaturePython)
  Dunit = g/cm3
  Dvalue = 1.19867
  Group = -> [C_element068,H_element062,N_element029,O_element069]
  conduct = 2
  density = 1
  expand = 3
  formula = G4_NITROBENZENE
  name = G4_NITROBENZENE
  specific = 4
FEATURE [App::DocumentObjectGroupPython] N_element030  label="N_element : 013"  # scripted group (container) (typed FeaturePython)
  n = 2
  ref = N_element
FEATURE [App::DocumentObjectGroupPython] O_element070  label="O_element : 035"  # scripted group (container) (typed FeaturePython)
  n = 1
  ref = O_element
FEATURE [App::DocumentObjectGroupPython] G4_NITROUS_OXIDE  # scripted group (container) (typed FeaturePython)
  Dunit = g/cm3
  Dvalue = 0.00183094
  Group = -> [N_element030,O_element070]
  conduct = 2
  density = 1
  expand = 3
  formula = G4_NITROUS_OXIDE
  name = G4_NITROUS_OXIDE
  specific = 4
FEATURE [App::DocumentObjectGroupPython] H_element063  label="H_element : 0.104"  # scripted group (container) (typed FeaturePython)
  n = 0.103509
FEATURE [App::DocumentObjectGroupPython] C_element069  label="C_element : 0.648"  # scripted group (container) (typed FeaturePython)
  n = 0.648416
FEATURE [App::DocumentObjectGroupPython] N_element031  label="N_element : 0.100"  # scripted group (container) (typed FeaturePython)
  n = 0.0995361
FEATURE [App::DocumentObjectGroupPython] O_element071  label="O_element : 0.149"  # scripted group (container) (typed FeaturePython)
  n = 0.148539
FEATURE [App::DocumentObjectGroupPython] G4_NYLON_8062  label="G4_NYLON-8062"  # scripted group (container) (typed FeaturePython)
  Dunit = g/cm3
  Dvalue = 1.08
  Group = -> [H_element063,C_element069,N_element031,O_element071]
  conduct = 2
  density = 1
  expand = 3
  formula = G4_NYLON-8062
  name = G4_NYLON-8062
  specific = 4
FEATURE [App::DocumentObjectGroupPython] C_element070  label="C_element : 035"  # scripted group (container) (typed FeaturePython)
  n = 6
  ref = C_element
FEATURE [App::DocumentObjectGroupPython] H_element064  label="H_element : 11"  # scripted group (container) (typed FeaturePython)
  n = 11
  ref = H_element
FEATURE [App::DocumentObjectGroupPython] N_element032  label="N_element : 014"  # scripted group (container) (typed FeaturePython)
  n = 1
  ref = N_element
FEATURE [App::DocumentObjectGroupPython] O_element072  label="O_element : 036"  # scripted group (container) (typed FeaturePython)
  n = 1
  ref = O_element
FEATURE [App::DocumentObjectGroupPython] G4_NYLON_6_6  label="G4_NYLON-6-6"  # scripted group (container) (typed FeaturePython)
  Dunit = g/cm3
  Dvalue = 1.14
  Group = -> [C_element070,H_element064,N_element032,O_element072]
  conduct = 2
  density = 1
  expand = 3
  formula = G4_NYLON-6-6
  name = G4_NYLON-6-6
  specific = 4
FEATURE [App::DocumentObjectGroupPython] H_element065  label="H_element : 0.139"  # scripted group (container) (typed FeaturePython)
  n = 0.107062
FEATURE [App::DocumentObjectGroupPython] C_element071  label="C_element : 0.680"  # scripted group (container) (typed FeaturePython)
  n = 0.680449
FEATURE [App::DocumentObjectGroupPython] N_element033  label="N_element : 0.099"  # scripted group (container) (typed FeaturePython)
  n = 0.099189
FEATURE [App::DocumentObjectGroupPython] O_element073  label="O_element : 0.113"  # scripted group (container) (typed FeaturePython)
  n = 0.1133
FEATURE [App::DocumentObjectGroupPython] G4_NYLON_6_10  label="G4_NYLON-6-10"  # scripted group (container) (typed FeaturePython)
  Dunit = g/cm3
  Dvalue = 1.14
  Group = -> [H_element065,C_element071,N_element033,O_element073]
  conduct = 2
  density = 1
  expand = 3
  formula = G4_NYLON-6-10
  name = G4_NYLON-6-10
  specific = 4
FEATURE [App::DocumentObjectGroupPython] H_element066  label="H_element : 0.140"  # scripted group (container) (typed FeaturePython)
  n = 0.115476
FEATURE [App::DocumentObjectGroupPython] C_element072  label="C_element : 0.721"  # scripted group (container) (typed FeaturePython)
  n = 0.720818
FEATURE [App::DocumentObjectGroupPython] N_element034  label="N_element : 0.076"  # scripted group (container) (typed FeaturePython)
  n = 0.0764169
FEATURE [App::DocumentObjectGroupPython] O_element074  label="O_element : 0.087"  # scripted group (container) (typed FeaturePython)
  n = 0.0872889
FEATURE [App::DocumentObjectGroupPython] G4_NYLON_11_RILSAN  label="G4_NYLON-11_RILSAN"  # scripted group (container) (typed FeaturePython)
  Dunit = g/cm3
  Dvalue = 1.425
  Group = -> [H_element066,C_element072,N_element034,O_element074]
  conduct = 2
  density = 1
  expand = 3
  formula = G4_NYLON-11_RILSAN
  name = G4_NYLON-11_RILSAN
  specific = 4
FEATURE [App::DocumentObjectGroupPython] C_element073  label="C_element : 8"  # scripted group (container) (typed FeaturePython)
  n = 8
  ref = C_element
FEATURE [App::DocumentObjectGroupPython] H_element067  label="H_element : 18"  # scripted group (container) (typed FeaturePython)
  n = 18
  ref = H_element
FEATURE [App::DocumentObjectGroupPython] G4_OCTANE  # scripted group (container) (typed FeaturePython)
  Dunit = g/cm3
  Dvalue = 0.7026
  Group = -> [C_element073,H_element067]
  conduct = 2
  density = 1
  expand = 3
  formula = G4_OCTANE
  name = G4_OCTANE
  specific = 4
FEATURE [App::DocumentObjectGroupPython] C_element074  label="C_element : 25"  # scripted group (container) (typed FeaturePython)
  n = 25
  ref = C_element
FEATURE [App::DocumentObjectGroupPython] H_element068  label="H_element : 52"  # scripted group (container) (typed FeaturePython)
  n = 52
  ref = H_element
FEATURE [App::DocumentObjectGroupPython] G4_PARAFFIN  # scripted group (container) (typed FeaturePython)
  Dunit = g/cm3
  Dvalue = 0.93
  Group = -> [C_element074,H_element068]
  conduct = 2
  density = 1
  expand = 3
  formula = G4_PARAFFIN
  name = G4_PARAFFIN
  specific = 4
FEATURE [App::DocumentObjectGroupPython] C_element075  label="C_element : 036"  # scripted group (container) (typed FeaturePython)
  n = 5
  ref = C_element
FEATURE [App::DocumentObjectGroupPython] H_element069  label="H_element : 032"  # scripted group (container) (typed FeaturePython)
  n = 12
  ref = H_element
FEATURE [App::DocumentObjectGroupPython] G4_N_PENTANE  label="G4_N-PENTANE"  # scripted group (container) (typed FeaturePython)
  Dunit = g/cm3
  Dvalue = 0.6262
  Group = -> [C_element075,H_element069]
  conduct = 2
  density = 1
  expand = 3
  formula = G4_N-PENTANE
  name = G4_N-PENTANE
  specific = 4
FEATURE [App::DocumentObjectGroupPython] H_element070  label="H_element : 0.014"  # scripted group (container) (typed FeaturePython)
  n = 0.0141
FEATURE [App::DocumentObjectGroupPython] C_element076  label="C_element : 0.072"  # scripted group (container) (typed FeaturePython)
  n = 0.072261
FEATURE [App::DocumentObjectGroupPython] N_element035  label="N_element : 0.019"  # scripted group (container) (typed FeaturePython)
  n = 0.01932
FEATURE [App::DocumentObjectGroupPython] O_element075  label="O_element : 0.066"  # scripted group (container) (typed FeaturePython)
  n = 0.066101
FEATURE [App::DocumentObjectGroupPython] S_element019  label="S_element : 0.020"  # scripted group (container) (typed FeaturePython)
  n = 0.00189
FEATURE [App::DocumentObjectGroupPython] Br_element004  label="Br_element : 0.349"  # scripted group (container) (typed FeaturePython)
  n = 0.349103
FEATURE [App::DocumentObjectGroupPython] Ag_element001  label="Ag_element : 0.474"  # scripted group (container) (typed FeaturePython)
  n = 0.474105
FEATURE [App::DocumentObjectGroupPython] I_element005  label="I_element : 0.003"  # scripted group (container) (typed FeaturePython)
  n = 0.00312
FEATURE [App::DocumentObjectGroupPython] G4_PHOTO_EMULSION  # scripted group (container) (typed FeaturePython)
  Dunit = g/cm3
  Dvalue = 3.815
  Group = -> [H_element070,C_element076,N_element035,O_element075,S_element019,Br_element004,Ag_element001,I_element005]
  conduct = 2
  density = 1
  expand = 3
  formula = G4_PHOTO_EMULSION
  name = G4_PHOTO_EMULSION
  specific = 4
FEATURE [App::DocumentObjectGroupPython] C_element077  label="C_element : 9"  # scripted group (container) (typed FeaturePython)
  n = 9
  ref = C_element
FEATURE [App::DocumentObjectGroupPython] H_element071  label="H_element : 033"  # scripted group (container) (typed FeaturePython)
  n = 10
  ref = H_element
FEATURE [App::DocumentObjectGroupPython] G4_PLASTIC_SC_VINYLTOLUENE  # scripted group (container) (typed FeaturePython)
  Dunit = g/cm3
  Dvalue = 1.032
  Group = -> [C_element077,H_element071]
  conduct = 2
  density = 1
  expand = 3
  formula = G4_PLASTIC_SC_VINYLTOLUENE
  name = G4_PLASTIC_SC_VINYLTOLUENE
  specific = 4
FEATURE [App::DocumentObjectGroupPython] Pu_element001  label="Pu_element : 1"  # scripted group (container) (typed FeaturePython)
  n = 1
  ref = Pu_element
FEATURE [App::DocumentObjectGroupPython] O_element076  label="O_element : 037"  # scripted group (container) (typed FeaturePython)
  n = 2
  ref = O_element
FEATURE [App::DocumentObjectGroupPython] G4_PLUTONIUM_DIOXIDE  # scripted group (container) (typed FeaturePython)
  Dunit = g/cm3
  Dvalue = 11.46
  Group = -> [Pu_element001,O_element076]
  conduct = 2
  density = 1
  expand = 3
  formula = G4_PLUTONIUM_DIOXIDE
  name = G4_PLUTONIUM_DIOXIDE
  specific = 4
FEATURE [App::DocumentObjectGroupPython] C_element078  label="C_element : 037"  # scripted group (container) (typed FeaturePython)
  n = 3
  ref = C_element
FEATURE [App::DocumentObjectGroupPython] H_element072  label="H_element : 034"  # scripted group (container) (typed FeaturePython)
  n = 3
  ref = H_element
FEATURE [App::DocumentObjectGroupPython] N_element036  label="N_element : 015"  # scripted group (container) (typed FeaturePython)
  n = 1
  ref = N_element
FEATURE [App::DocumentObjectGroupPython] G4_POLYACRYLONITRILE  # scripted group (container) (typed FeaturePython)
  Dunit = g/cm3
  Dvalue = 1.17
  Group = -> [C_element078,H_element072,N_element036]
  conduct = 2
  density = 1
  expand = 3
  formula = G4_POLYACRYLONITRILE
  name = G4_POLYACRYLONITRILE
  specific = 4
FEATURE [App::DocumentObjectGroupPython] C_element079  label="C_element : 16"  # scripted group (container) (typed FeaturePython)
  n = 16
  ref = C_element
FEATURE [App::DocumentObjectGroupPython] H_element073  label="H_element : 035"  # scripted group (container) (typed FeaturePython)
  n = 14
  ref = H_element
FEATURE [App::DocumentObjectGroupPython] O_element077  label="O_element : 038"  # scripted group (container) (typed FeaturePython)
  n = 3
  ref = O_element
FEATURE [App::DocumentObjectGroupPython] G4_POLYCARBONATE  # scripted group (container) (typed FeaturePython)
  Dunit = g/cm3
  Dvalue = 1.2
  Group = -> [C_element079,H_element073,O_element077]
  conduct = 2
  density = 1
  expand = 3
  formula = G4_POLYCARBONATE
  name = G4_POLYCARBONATE
  specific = 4
FEATURE [App::DocumentObjectGroupPython] C_element080  label="C_element : 038"  # scripted group (container) (typed FeaturePython)
  n = 8
  ref = C_element
FEATURE [App::DocumentObjectGroupPython] H_element074  label="H_element : 036"  # scripted group (container) (typed FeaturePython)
  n = 7
  ref = H_element
FEATURE [App::DocumentObjectGroupPython] Cl_element017  label="Cl_element : 007"  # scripted group (container) (typed FeaturePython)
  n = 1
  ref = Cl_element
FEATURE [App::DocumentObjectGroupPython] G4_POLYCHLOROSTYRENE  # scripted group (container) (typed FeaturePython)
  Dunit = g/cm3
  Dvalue = 1.3
  Group = -> [C_element080,H_element074,Cl_element017]
  conduct = 2
  density = 1
  expand = 3
  formula = G4_POLYCHLOROSTYRENE
  name = G4_POLYCHLOROSTYRENE
  specific = 4
FEATURE [App::DocumentObjectGroupPython] C_element081  label="C_element : 039"  # scripted group (container) (typed FeaturePython)
  n = 1
  ref = C_element
FEATURE [App::DocumentObjectGroupPython] H_element075  label="H_element : 037"  # scripted group (container) (typed FeaturePython)
  n = 2
  ref = H_element
FEATURE [App::DocumentObjectGroupPython] G4_POLYETHYLENE  # scripted group (container) (typed FeaturePython)
  Dunit = g/cm3
  Dvalue = 0.94
  Group = -> [C_element081,H_element075]
  conduct = 2
  density = 1
  expand = 3
  formula = G4_POLYETHYLENE
  name = G4_POLYETHYLENE
  specific = 4
FEATURE [App::DocumentObjectGroupPython] C_element082  label="C_element : 040"  # scripted group (container) (typed FeaturePython)
  n = 10
  ref = C_element
FEATURE [App::DocumentObjectGroupPython] H_element076  label="H_element : 038"  # scripted group (container) (typed FeaturePython)
  n = 8
  ref = H_element
FEATURE [App::DocumentObjectGroupPython] O_element078  label="O_element : 039"  # scripted group (container) (typed FeaturePython)
  n = 4
  ref = O_element
FEATURE [App::DocumentObjectGroupPython] G4_MYLAR  # scripted group (container) (typed FeaturePython)
  Dunit = g/cm3
  Dvalue = 1.4
  Group = -> [C_element082,H_element076,O_element078]
  conduct = 2
  density = 1
  expand = 3
  formula = G4_MYLAR
  name = G4_MYLAR
  specific = 4
FEATURE [App::DocumentObjectGroupPython] C_element083  label="C_element : 041"  # scripted group (container) (typed FeaturePython)
  n = 5
  ref = C_element
FEATURE [App::DocumentObjectGroupPython] H_element077  label="H_element : 039"  # scripted group (container) (typed FeaturePython)
  n = 8
  ref = H_element
FEATURE [App::DocumentObjectGroupPython] O_element079  label="O_element : 040"  # scripted group (container) (typed FeaturePython)
  n = 2
  ref = O_element
FEATURE [App::DocumentObjectGroupPython] G4_PLEXIGLASS  # scripted group (container) (typed FeaturePython)
  Dunit = g/cm3
  Dvalue = 1.19
  Group = -> [C_element083,H_element077,O_element079]
  conduct = 2
  density = 1
  expand = 3
  formula = G4_PLEXIGLASS
  name = G4_PLEXIGLASS
  specific = 4
FEATURE [App::DocumentObjectGroupPython] C_element084  label="C_element : 042"  # scripted group (container) (typed FeaturePython)
  n = 1
  ref = C_element
FEATURE [App::DocumentObjectGroupPython] H_element078  label="H_element : 040"  # scripted group (container) (typed FeaturePython)
  n = 2
  ref = H_element
FEATURE [App::DocumentObjectGroupPython] O_element080  label="O_element : 041"  # scripted group (container) (typed FeaturePython)
  n = 1
  ref = O_element
FEATURE [App::DocumentObjectGroupPython] G4_POLYOXYMETHYLENE  # scripted group (container) (typed FeaturePython)
  Dunit = g/cm3
  Dvalue = 1.425
  Group = -> [C_element084,H_element078,O_element080]
  conduct = 2
  density = 1
  expand = 3
  formula = G4_POLYOXYMETHYLENE
  name = G4_POLYOXYMETHYLENE
  specific = 4
FEATURE [App::DocumentObjectGroupPython] C_element085  label="C_element : 043"  # scripted group (container) (typed FeaturePython)
  n = 2
  ref = C_element
FEATURE [App::DocumentObjectGroupPython] H_element079  label="H_element : 041"  # scripted group (container) (typed FeaturePython)
  n = 4
  ref = H_element
FEATURE [App::DocumentObjectGroupPython] G4_POLYPROPYLENE  # scripted group (container) (typed FeaturePython)
  Dunit = g/cm3
  Dvalue = 0.9
  Group = -> [C_element085,H_element079]
  conduct = 2
  density = 1
  expand = 3
  formula = G4_POLYPROPYLENE
  name = G4_POLYPROPYLENE
  specific = 4
FEATURE [App::DocumentObjectGroupPython] C_element086  label="C_element : 044"  # scripted group (container) (typed FeaturePython)
  n = 8
  ref = C_element
FEATURE [App::DocumentObjectGroupPython] H_element080  label="H_element : 042"  # scripted group (container) (typed FeaturePython)
  n = 8
  ref = H_element
FEATURE [App::DocumentObjectGroupPython] G4_POLYSTYRENE  # scripted group (container) (typed FeaturePython)
  Dunit = g/cm3
  Dvalue = 1.06
  Group = -> [C_element086,H_element080]
  conduct = 2
  density = 1
  expand = 3
  formula = G4_POLYSTYRENE
  name = G4_POLYSTYRENE
  specific = 4
FEATURE [App::DocumentObjectGroupPython] C_element087  label="C_element : 045"  # scripted group (container) (typed FeaturePython)
  n = 2
  ref = C_element
FEATURE [App::DocumentObjectGroupPython] F_element014  label="F_element : 4"  # scripted group (container) (typed FeaturePython)
  n = 4
  ref = F_element
FEATURE [App::DocumentObjectGroupPython] G4_TEFLON  # scripted group (container) (typed FeaturePython)
  Dunit = g/cm3
  Dvalue = 2.2
  Group = -> [C_element087,F_element014]
  conduct = 2
  density = 1
  expand = 3
  formula = G4_TEFLON
  name = G4_TEFLON
  specific = 4
FEATURE [App::DocumentObjectGroupPython] C_element088  label="C_element : 046"  # scripted group (container) (typed FeaturePython)
  n = 2
  ref = C_element
FEATURE [App::DocumentObjectGroupPython] F_element015  label="F_element : 006"  # scripted group (container) (typed FeaturePython)
  n = 3
  ref = F_element
FEATURE [App::DocumentObjectGroupPython] Cl_element018  label="Cl_element : 008"  # scripted group (container) (typed FeaturePython)
  n = 1
  ref = Cl_element
FEATURE [App::DocumentObjectGroupPython] G4_POLYTRIFLUOROCHLOROETHYLENE  # scripted group (container) (typed FeaturePython)
  Dunit = g/cm3
  Dvalue = 2.1
  Group = -> [C_element088,F_element015,Cl_element018]
  conduct = 2
  density = 1
  expand = 3
  formula = G4_POLYTRIFLUOROCHLOROETHYLENE
  name = G4_POLYTRIFLUOROCHLOROETHYLENE
  specific = 4
FEATURE [App::DocumentObjectGroupPython] C_element089  label="C_element : 047"  # scripted group (container) (typed FeaturePython)
  n = 4
  ref = C_element
FEATURE [App::DocumentObjectGroupPython] H_element081  label="H_element : 043"  # scripted group (container) (typed FeaturePython)
  n = 6
  ref = H_element
FEATURE [App::DocumentObjectGroupPython] O_element081  label="O_element : 042"  # scripted group (container) (typed FeaturePython)
  n = 2
  ref = O_element
FEATURE [App::DocumentObjectGroupPython] G4_POLYVINYL_ACETATE  # scripted group (container) (typed FeaturePython)
  Dunit = g/cm3
  Dvalue = 1.19
  Group = -> [C_element089,H_element081,O_element081]
  conduct = 2
  density = 1
  expand = 3
  formula = G4_POLYVINYL_ACETATE
  name = G4_POLYVINYL_ACETATE
  specific = 4
FEATURE [App::DocumentObjectGroupPython] C_element090  label="C_element : 048"  # scripted group (container) (typed FeaturePython)
  n = 2
  ref = C_element
FEATURE [App::DocumentObjectGroupPython] H_element082  label="H_element : 044"  # scripted group (container) (typed FeaturePython)
  n = 4
  ref = H_element
FEATURE [App::DocumentObjectGroupPython] O_element082  label="O_element : 043"  # scripted group (container) (typed FeaturePython)
  n = 1
  ref = O_element
FEATURE [App::DocumentObjectGroupPython] G4_POLYVINYL_ALCOHOL  # scripted group (container) (typed FeaturePython)
  Dunit = g/cm3
  Dvalue = 1.3
  Group = -> [C_element090,H_element082,O_element082]
  conduct = 2
  density = 1
  expand = 3
  formula = G4_POLYVINYL_ALCOHOL
  name = G4_POLYVINYL_ALCOHOL
  specific = 4
FEATURE [App::DocumentObjectGroupPython] C_element091  label="C_element : 049"  # scripted group (container) (typed FeaturePython)
  n = 8
  ref = C_element
FEATURE [App::DocumentObjectGroupPython] H_element083  label="H_element : 045"  # scripted group (container) (typed FeaturePython)
  n = 14
  ref = H_element
FEATURE [App::DocumentObjectGroupPython] O_element083  label="O_element : 044"  # scripted group (container) (typed FeaturePython)
  n = 2
  ref = O_element
FEATURE [App::DocumentObjectGroupPython] G4_POLYVINYL_BUTYRAL  # scripted group (container) (typed FeaturePython)
  Dunit = g/cm3
  Dvalue = 1.12
  Group = -> [C_element091,H_element083,O_element083]
  conduct = 2
  density = 1
  expand = 3
  formula = G4_POLYVINYL_BUTYRAL
  name = G4_POLYVINYL_BUTYRAL
  specific = 4
FEATURE [App::DocumentObjectGroupPython] C_element092  label="C_element : 050"  # scripted group (container) (typed FeaturePython)
  n = 2
  ref = C_element
FEATURE [App::DocumentObjectGroupPython] H_element084  label="H_element : 046"  # scripted group (container) (typed FeaturePython)
  n = 3
  ref = H_element
FEATURE [App::DocumentObjectGroupPython] Cl_element019  label="Cl_element : 009"  # scripted group (container) (typed FeaturePython)
  n = 1
  ref = Cl_element
FEATURE [App::DocumentObjectGroupPython] G4_POLYVINYL_CHLORIDE  # scripted group (container) (typed FeaturePython)
  Dunit = g/cm3
  Dvalue = 1.3
  Group = -> [C_element092,H_element084,Cl_element019]
  conduct = 2
  density = 1
  expand = 3
  formula = G4_POLYVINYL_CHLORIDE
  name = G4_POLYVINYL_CHLORIDE
  specific = 4
FEATURE [App::DocumentObjectGroupPython] C_element093  label="C_element : 051"  # scripted group (container) (typed FeaturePython)
  n = 2
  ref = C_element
FEATURE [App::DocumentObjectGroupPython] H_element085  label="H_element : 047"  # scripted group (container) (typed FeaturePython)
  n = 2
  ref = H_element
FEATURE [App::DocumentObjectGroupPython] Cl_element020  label="Cl_element : 010"  # scripted group (container) (typed FeaturePython)
  n = 2
  ref = Cl_element
FEATURE [App::DocumentObjectGroupPython] G4_POLYVINYLIDENE_CHLORIDE  # scripted group (container) (typed FeaturePython)
  Dunit = g/cm3
  Dvalue = 1.7
  Group = -> [C_element093,H_element085,Cl_element020]
  conduct = 2
  density = 1
  expand = 3
  formula = G4_POLYVINYLIDENE_CHLORIDE
  name = G4_POLYVINYLIDENE_CHLORIDE
  specific = 4
FEATURE [App::DocumentObjectGroupPython] C_element094  label="C_element : 052"  # scripted group (container) (typed FeaturePython)
  n = 2
  ref = C_element
FEATURE [App::DocumentObjectGroupPython] H_element086  label="H_element : 048"  # scripted group (container) (typed FeaturePython)
  n = 2
  ref = H_element
FEATURE [App::DocumentObjectGroupPython] F_element016  label="F_element : 007"  # scripted group (container) (typed FeaturePython)
  n = 2
  ref = F_element
FEATURE [App::DocumentObjectGroupPython] G4_POLYVINYLIDENE_FLUORIDE  # scripted group (container) (typed FeaturePython)
  Dunit = g/cm3
  Dvalue = 1.76
  Group = -> [C_element094,H_element086,F_element016]
  conduct = 2
  density = 1
  expand = 3
  formula = G4_POLYVINYLIDENE_FLUORIDE
  name = G4_POLYVINYLIDENE_FLUORIDE
  specific = 4
FEATURE [App::DocumentObjectGroupPython] C_element095  label="C_element : 053"  # scripted group (container) (typed FeaturePython)
  n = 6
  ref = C_element
FEATURE [App::DocumentObjectGroupPython] H_element087  label="H_element : 9"  # scripted group (container) (typed FeaturePython)
  n = 9
  ref = H_element
FEATURE [App::DocumentObjectGroupPython] N_element037  label="N_element : 016"  # scripted group (container) (typed FeaturePython)
  n = 1
  ref = N_element
FEATURE [App::DocumentObjectGroupPython] O_element084  label="O_element : 045"  # scripted group (container) (typed FeaturePython)
  n = 1
  ref = O_element
FEATURE [App::DocumentObjectGroupPython] G4_POLYVINYL_PYRROLIDONE  # scripted group (container) (typed FeaturePython)
  Dunit = g/cm3
  Dvalue = 1.25
  Group = -> [C_element095,H_element087,N_element037,O_element084]
  conduct = 2
  density = 1
  expand = 3
  formula = G4_POLYVINYL_PYRROLIDONE
  name = G4_POLYVINYL_PYRROLIDONE
  specific = 4
FEATURE [App::DocumentObjectGroupPython] K_element008  label="K_element : 1"  # scripted group (container) (typed FeaturePython)
  n = 1
  ref = K_element
FEATURE [App::DocumentObjectGroupPython] I_element006  label="I_element : 003"  # scripted group (container) (typed FeaturePython)
  n = 1
  ref = I_element
FEATURE [App::DocumentObjectGroupPython] G4_POTASSIUM_IODIDE  # scripted group (container) (typed FeaturePython)
  Dunit = g/cm3
  Dvalue = 3.13
  Group = -> [K_element008,I_element006]
  conduct = 2
  density = 1
  expand = 3
  formula = G4_POTASSIUM_IODIDE
  name = G4_POTASSIUM_IODIDE
  specific = 4
FEATURE [App::DocumentObjectGroupPython] K_element009  label="K_element : 2"  # scripted group (container) (typed FeaturePython)
  n = 2
  ref = K_element
FEATURE [App::DocumentObjectGroupPython] O_element085  label="O_element : 046"  # scripted group (container) (typed FeaturePython)
  n = 1
  ref = O_element
FEATURE [App::DocumentObjectGroupPython] G4_POTASSIUM_OXIDE  # scripted group (container) (typed FeaturePython)
  Dunit = g/cm3
  Dvalue = 2.32
  Group = -> [K_element009,O_element085]
  conduct = 2
  density = 1
  expand = 3
  formula = G4_POTASSIUM_OXIDE
  name = G4_POTASSIUM_OXIDE
  specific = 4
FEATURE [App::DocumentObjectGroupPython] C_element096  label="C_element : 054"  # scripted group (container) (typed FeaturePython)
  n = 3
  ref = C_element
FEATURE [App::DocumentObjectGroupPython] H_element088  label="H_element : 049"  # scripted group (container) (typed FeaturePython)
  n = 8
  ref = H_element
FEATURE [App::DocumentObjectGroupPython] G4_PROPANE  # scripted group (container) (typed FeaturePython)
  Dunit = g/cm3
  Dvalue = 0.00187939
  Group = -> [C_element096,H_element088]
  conduct = 2
  density = 1
  expand = 3
  formula = G4_PROPANE
  name = G4_PROPANE
  specific = 4
FEATURE [App::DocumentObjectGroupPython] C_element097  label="C_element : 055"  # scripted group (container) (typed FeaturePython)
  n = 3
  ref = C_element
FEATURE [App::DocumentObjectGroupPython] H_element089  label="H_element : 050"  # scripted group (container) (typed FeaturePython)
  n = 8
  ref = H_element
FEATURE [App::DocumentObjectGroupPython] G4_lPROPANE  # scripted group (container) (typed FeaturePython)
  Dunit = g/cm3
  Dvalue = 0.43
  Group = -> [C_element097,H_element089]
  conduct = 2
  density = 1
  expand = 3
  formula = G4_lPROPANE
  name = G4_lPROPANE
  specific = 4
FEATURE [App::DocumentObjectGroupPython] C_element098  label="C_element : 056"  # scripted group (container) (typed FeaturePython)
  n = 3
  ref = C_element
FEATURE [App::DocumentObjectGroupPython] H_element090  label="H_element : 051"  # scripted group (container) (typed FeaturePython)
  n = 8
  ref = H_element
FEATURE [App::DocumentObjectGroupPython] O_element086  label="O_element : 047"  # scripted group (container) (typed FeaturePython)
  n = 1
  ref = O_element
FEATURE [App::DocumentObjectGroupPython] G4_N_PROPYL_ALCOHOL  label="G4_N-PROPYL_ALCOHOL"  # scripted group (container) (typed FeaturePython)
  Dunit = g/cm3
  Dvalue = 0.8035
  Group = -> [C_element098,H_element090,O_element086]
  conduct = 2
  density = 1
  expand = 3
  formula = G4_N-PROPYL_ALCOHOL
  name = G4_N-PROPYL_ALCOHOL
  specific = 4
FEATURE [App::DocumentObjectGroupPython] C_element099  label="C_element : 057"  # scripted group (container) (typed FeaturePython)
  n = 5
  ref = C_element
FEATURE [App::DocumentObjectGroupPython] H_element091  label="H_element : 052"  # scripted group (container) (typed FeaturePython)
  n = 5
  ref = H_element
FEATURE [App::DocumentObjectGroupPython] N_element038  label="N_element : 017"  # scripted group (container) (typed FeaturePython)
  n = 1
  ref = N_element
FEATURE [App::DocumentObjectGroupPython] G4_PYRIDINE  # scripted group (container) (typed FeaturePython)
  Dunit = g/cm3
  Dvalue = 0.9819
  Group = -> [C_element099,H_element091,N_element038]
  conduct = 2
  density = 1
  expand = 3
  formula = G4_PYRIDINE
  name = G4_PYRIDINE
  specific = 4
FEATURE [App::DocumentObjectGroupPython] H_element092  label="H_element : 0.144"  # scripted group (container) (typed FeaturePython)
  n = 0.143711
FEATURE [App::DocumentObjectGroupPython] C_element100  label="C_element : 0.856"  # scripted group (container) (typed FeaturePython)
  n = 0.856289
FEATURE [App::DocumentObjectGroupPython] G4_RUBBER_BUTYL  # scripted group (container) (typed FeaturePython)
  Dunit = g/cm3
  Dvalue = 0.92
  Group = -> [H_element092,C_element100]
  conduct = 2
  density = 1
  expand = 3
  formula = G4_RUBBER_BUTYL
  name = G4_RUBBER_BUTYL
  specific = 4
FEATURE [App::DocumentObjectGroupPython] H_element093  label="H_element : 0.118"  # scripted group (container) (typed FeaturePython)
  n = 0.118371
FEATURE [App::DocumentObjectGroupPython] C_element101  label="C_element : 0.882"  # scripted group (container) (typed FeaturePython)
  n = 0.881629
FEATURE [App::DocumentObjectGroupPython] G4_RUBBER_NATURAL  # scripted group (container) (typed FeaturePython)
  Dunit = g/cm3
  Dvalue = 0.92
  Group = -> [H_element093,C_element101]
  conduct = 2
  density = 1
  expand = 3
  formula = G4_RUBBER_NATURAL
  name = G4_RUBBER_NATURAL
  specific = 4
FEATURE [App::DocumentObjectGroupPython] H_element094  label="H_element : 0.145"  # scripted group (container) (typed FeaturePython)
  n = 0.05692
FEATURE [App::DocumentObjectGroupPython] C_element102  label="C_element : 0.543"  # scripted group (container) (typed FeaturePython)
  n = 0.542646
FEATURE [App::DocumentObjectGroupPython] Cl_element021  label="Cl_element : 0.400"  # scripted group (container) (typed FeaturePython)
  n = 0.400434
FEATURE [App::DocumentObjectGroupPython] G4_RUBBER_NEOPRENE  # scripted group (container) (typed FeaturePython)
  Dunit = g/cm3
  Dvalue = 1.23
  Group = -> [H_element094,C_element102,Cl_element021]
  conduct = 2
  density = 1
  expand = 3
  formula = G4_RUBBER_NEOPRENE
  name = G4_RUBBER_NEOPRENE
  specific = 4
FEATURE [App::DocumentObjectGroupPython] Si_element006  label="Si_element : 1"  # scripted group (container) (typed FeaturePython)
  n = 1
  ref = Si_element
FEATURE [App::DocumentObjectGroupPython] O_element087  label="O_element : 048"  # scripted group (container) (typed FeaturePython)
  n = 2
  ref = O_element
FEATURE [App::DocumentObjectGroupPython] G4_SILICON_DIOXIDE002  label="G4_SILICON_DIOXIDE"  # scripted group (container) (typed FeaturePython)
  Dunit = g/cm3
  Dvalue = 2.32
  Group = -> [Si_element006,O_element087]
  conduct = 2
  density = 1
  expand = 3
  formula = G4_SILICON_DIOXIDE
  name = G4_SILICON_DIOXIDE
  specific = 4
FEATURE [App::DocumentObjectGroupPython] Ag_element002  label="Ag_element : 1"  # scripted group (container) (typed FeaturePython)
  n = 1
  ref = Ag_element
FEATURE [App::DocumentObjectGroupPython] Br_element005  label="Br_element : 003"  # scripted group (container) (typed FeaturePython)
  n = 1
  ref = Br_element
FEATURE [App::DocumentObjectGroupPython] G4_SILVER_BROMIDE  # scripted group (container) (typed FeaturePython)
  Dunit = g/cm3
  Dvalue = 6.473
  Group = -> [Ag_element002,Br_element005]
  conduct = 2
  density = 1
  expand = 3
  formula = G4_SILVER_BROMIDE
  name = G4_SILVER_BROMIDE
  specific = 4
FEATURE [App::DocumentObjectGroupPython] Ag_element003  label="Ag_element : 002"  # scripted group (container) (typed FeaturePython)
  n = 1
  ref = Ag_element
FEATURE [App::DocumentObjectGroupPython] Cl_element022  label="Cl_element : 011"  # scripted group (container) (typed FeaturePython)
  n = 1
  ref = Cl_element
FEATURE [App::DocumentObjectGroupPython] G4_SILVER_CHLORIDE  # scripted group (container) (typed FeaturePython)
  Dunit = g/cm3
  Dvalue = 5.56
  Group = -> [Ag_element003,Cl_element022]
  conduct = 2
  density = 1
  expand = 3
  formula = G4_SILVER_CHLORIDE
  name = G4_SILVER_CHLORIDE
  specific = 4
FEATURE [App::DocumentObjectGroupPython] Br_element006  label="Br_element : 0.423"  # scripted group (container) (typed FeaturePython)
  n = 0.422895
FEATURE [App::DocumentObjectGroupPython] Ag_element004  label="Ag_element : 0.574"  # scripted group (container) (typed FeaturePython)
  n = 0.573748
FEATURE [App::DocumentObjectGroupPython] I_element007  label="I_element : 0.649"  # scripted group (container) (typed FeaturePython)
  n = 0.003357
FEATURE [App::DocumentObjectGroupPython] G4_SILVER_HALIDES  # scripted group (container) (typed FeaturePython)
  Dunit = g/cm3
  Dvalue = 6.47
  Group = -> [Br_element006,Ag_element004,I_element007]
  conduct = 2
  density = 1
  expand = 3
  formula = G4_SILVER_HALIDES
  name = G4_SILVER_HALIDES
  specific = 4
FEATURE [App::DocumentObjectGroupPython] Ag_element005  label="Ag_element : 003"  # scripted group (container) (typed FeaturePython)
  n = 1
  ref = Ag_element
FEATURE [App::DocumentObjectGroupPython] I_element008  label="I_element : 004"  # scripted group (container) (typed FeaturePython)
  n = 1
  ref = I_element
FEATURE [App::DocumentObjectGroupPython] G4_SILVER_IODIDE  # scripted group (container) (typed FeaturePython)
  Dunit = g/cm3
  Dvalue = 6.01
  Group = -> [Ag_element005,I_element008]
  conduct = 2
  density = 1
  expand = 3
  formula = G4_SILVER_IODIDE
  name = G4_SILVER_IODIDE
  specific = 4
FEATURE [App::DocumentObjectGroupPython] H_element095  label="H_element : 0.100"  # scripted group (container) (typed FeaturePython)
  n = 0.1
FEATURE [App::DocumentObjectGroupPython] C_element103  label="C_element : 0.204"  # scripted group (container) (typed FeaturePython)
  n = 0.204
FEATURE [App::DocumentObjectGroupPython] N_element039  label="N_element : 0.759"  # scripted group (container) (typed FeaturePython)
  n = 0.042
FEATURE [App::DocumentObjectGroupPython] O_element088  label="O_element : 0.645"  # scripted group (container) (typed FeaturePython)
  n = 0.645
FEATURE [App::DocumentObjectGroupPython] Na_element013  label="Na_element : 0.100"  # scripted group (container) (typed FeaturePython)
  n = 0.002
FEATURE [App::DocumentObjectGroupPython] P_element009  label="P_element : 0.107"  # scripted group (container) (typed FeaturePython)
  n = 0.001
FEATURE [App::DocumentObjectGroupPython] S_element020  label="S_element : 0.021"  # scripted group (container) (typed FeaturePython)
  n = 0.002
FEATURE [App::DocumentObjectGroupPython] Cl_element023  label="Cl_element : 0.590"  # scripted group (container) (typed FeaturePython)
  n = 0.003
FEATURE [App::DocumentObjectGroupPython] K_element010  label="K_element : 0.001"  # scripted group (container) (typed FeaturePython)
  n = 0.001
FEATURE [App::DocumentObjectGroupPython] G4_SKIN_ICRP  # scripted group (container) (typed FeaturePython)
  Dunit = g/cm3
  Dvalue = 1.09
  Group = -> [H_element095,C_element103,N_element039,O_element088,Na_element013,P_element009,S_element020,Cl_element023,K_element010]
  conduct = 2
  density = 1
  expand = 3
  formula = G4_SKIN_ICRP
  name = G4_SKIN_ICRP
  specific = 4
FEATURE [App::DocumentObjectGroupPython] Na_element014  label="Na_element : 2"  # scripted group (container) (typed FeaturePython)
  n = 2
  ref = Na_element
FEATURE [App::DocumentObjectGroupPython] C_element104  label="C_element : 058"  # scripted group (container) (typed FeaturePython)
  n = 1
  ref = C_element
FEATURE [App::DocumentObjectGroupPython] O_element089  label="O_element : 049"  # scripted group (container) (typed FeaturePython)
  n = 3
  ref = O_element
FEATURE [App::DocumentObjectGroupPython] G4_SODIUM_CARBONATE  # scripted group (container) (typed FeaturePython)
  Dunit = g/cm3
  Dvalue = 2.532
  Group = -> [Na_element014,C_element104,O_element089]
  conduct = 2
  density = 1
  expand = 3
  formula = G4_SODIUM_CARBONATE
  name = G4_SODIUM_CARBONATE
  specific = 4
FEATURE [App::DocumentObjectGroupPython] Na_element015  label="Na_element : 1"  # scripted group (container) (typed FeaturePython)
  n = 1
  ref = Na_element
FEATURE [App::DocumentObjectGroupPython] I_element009  label="I_element : 005"  # scripted group (container) (typed FeaturePython)
  n = 1
  ref = I_element
FEATURE [App::DocumentObjectGroupPython] G4_SODIUM_IODIDE  # scripted group (container) (typed FeaturePython)
  Dunit = g/cm3
  Dvalue = 3.667
  Group = -> [Na_element015,I_element009]
  conduct = 2
  density = 1
  expand = 3
  formula = G4_SODIUM_IODIDE
  name = G4_SODIUM_IODIDE
  specific = 4
FEATURE [App::DocumentObjectGroupPython] Na_element016  label="Na_element : 003"  # scripted group (container) (typed FeaturePython)
  n = 2
  ref = Na_element
FEATURE [App::DocumentObjectGroupPython] O_element090  label="O_element : 050"  # scripted group (container) (typed FeaturePython)
  n = 1
  ref = O_element
FEATURE [App::DocumentObjectGroupPython] G4_SODIUM_MONOXIDE  # scripted group (container) (typed FeaturePython)
  Dunit = g/cm3
  Dvalue = 2.27
  Group = -> [Na_element016,O_element090]
  conduct = 2
  density = 1
  expand = 3
  formula = G4_SODIUM_MONOXIDE
  name = G4_SODIUM_MONOXIDE
  specific = 4
FEATURE [App::DocumentObjectGroupPython] Na_element017  label="Na_element : 004"  # scripted group (container) (typed FeaturePython)
  n = 1
  ref = Na_element
FEATURE [App::DocumentObjectGroupPython] N_element040  label="N_element : 018"  # scripted group (container) (typed FeaturePython)
  n = 1
  ref = N_element
FEATURE [App::DocumentObjectGroupPython] O_element091  label="O_element : 051"  # scripted group (container) (typed FeaturePython)
  n = 3
  ref = O_element
FEATURE [App::DocumentObjectGroupPython] G4_SODIUM_NITRATE  # scripted group (container) (typed FeaturePython)
  Dunit = g/cm3
  Dvalue = 2.261
  Group = -> [Na_element017,N_element040,O_element091]
  conduct = 2
  density = 1
  expand = 3
  formula = G4_SODIUM_NITRATE
  name = G4_SODIUM_NITRATE
  specific = 4
FEATURE [App::DocumentObjectGroupPython] C_element105  label="C_element : 059"  # scripted group (container) (typed FeaturePython)
  n = 14
  ref = C_element
FEATURE [App::DocumentObjectGroupPython] H_element096  label="H_element : 053"  # scripted group (container) (typed FeaturePython)
  n = 12
  ref = H_element
FEATURE [App::DocumentObjectGroupPython] G4_STILBENE  # scripted group (container) (typed FeaturePython)
  Dunit = g/cm3
  Dvalue = 0.9707
  Group = -> [C_element105,H_element096]
  conduct = 2
  density = 1
  expand = 3
  formula = G4_STILBENE
  name = G4_STILBENE
  specific = 4
FEATURE [App::DocumentObjectGroupPython] C_element106  label="C_element : 12"  # scripted group (container) (typed FeaturePython)
  n = 12
  ref = C_element
FEATURE [App::DocumentObjectGroupPython] H_element097  label="H_element : 22"  # scripted group (container) (typed FeaturePython)
  n = 22
  ref = H_element
FEATURE [App::DocumentObjectGroupPython] O_element092  label="O_element : 11"  # scripted group (container) (typed FeaturePython)
  n = 11
  ref = O_element
FEATURE [App::DocumentObjectGroupPython] G4_SUCROSE  # scripted group (container) (typed FeaturePython)
  Dunit = g/cm3
  Dvalue = 1.5805
  Group = -> [C_element106,H_element097,O_element092]
  conduct = 2
  density = 1
  expand = 3
  formula = G4_SUCROSE
  name = G4_SUCROSE
  specific = 4
FEATURE [App::DocumentObjectGroupPython] C_element107  label="C_element : 18"  # scripted group (container) (typed FeaturePython)
  n = 18
  ref = C_element
FEATURE [App::DocumentObjectGroupPython] H_element098  label="H_element : 054"  # scripted group (container) (typed FeaturePython)
  n = 14
  ref = H_element
FEATURE [App::DocumentObjectGroupPython] G4_TERPHENYL  # scripted group (container) (typed FeaturePython)
  Dunit = g/cm3
  Dvalue = 1.24
  Group = -> [C_element107,H_element098]
  conduct = 2
  density = 1
  expand = 3
  formula = G4_TERPHENYL
  name = G4_TERPHENYL
  specific = 4
FEATURE [App::DocumentObjectGroupPython] H_element099  label="H_element : 0.146"  # scripted group (container) (typed FeaturePython)
  n = 0.106
FEATURE [App::DocumentObjectGroupPython] C_element108  label="C_element : 0.883"  # scripted group (container) (typed FeaturePython)
  n = 0.099
FEATURE [App::DocumentObjectGroupPython] N_element041  label="N_element : 0.020"  # scripted group (container) (typed FeaturePython)
  n = 0.02
FEATURE [App::DocumentObjectGroupPython] O_element093  label="O_element : 0.766"  # scripted group (container) (typed FeaturePython)
  n = 0.766
FEATURE [App::DocumentObjectGroupPython] Na_element018  label="Na_element : 0.101"  # scripted group (container) (typed FeaturePython)
  n = 0.002
FEATURE [App::DocumentObjectGroupPython] P_element010  label="P_element : 0.108"  # scripted group (container) (typed FeaturePython)
  n = 0.001
FEATURE [App::DocumentObjectGroupPython] S_element021  label="S_element : 0.022"  # scripted group (container) (typed FeaturePython)
  n = 0.002
FEATURE [App::DocumentObjectGroupPython] Cl_element024  label="Cl_element : 0.002"  # scripted group (container) (typed FeaturePython)
  n = 0.002
FEATURE [App::DocumentObjectGroupPython] K_element011  label="K_element : 0.017"  # scripted group (container) (typed FeaturePython)
  n = 0.002
FEATURE [App::DocumentObjectGroupPython] G4_TESTIS_ICRP  # scripted group (container) (typed FeaturePython)
  Dunit = g/cm3
  Dvalue = 1.04
  Group = -> [H_element099,C_element108,N_element041,O_element093,Na_element018,P_element010,S_element021,Cl_element024,K_element011]
  conduct = 2
  density = 1
  expand = 3
  formula = G4_TESTIS_ICRP
  name = G4_TESTIS_ICRP
  specific = 4
FEATURE [App::DocumentObjectGroupPython] C_element109  label="C_element : 060"  # scripted group (container) (typed FeaturePython)
  n = 2
  ref = C_element
FEATURE [App::DocumentObjectGroupPython] Cl_element025  label="Cl_element : 012"  # scripted group (container) (typed FeaturePython)
  n = 4
  ref = Cl_element
FEATURE [App::DocumentObjectGroupPython] G4_TETRACHLOROETHYLENE  # scripted group (container) (typed FeaturePython)
  Dunit = g/cm3
  Dvalue = 1.625
  Group = -> [C_element109,Cl_element025]
  conduct = 2
  density = 1
  expand = 3
  formula = G4_TETRACHLOROETHYLENE
  name = G4_TETRACHLOROETHYLENE
  specific = 4
FEATURE [App::DocumentObjectGroupPython] Tl_element001  label="Tl_element : 1"  # scripted group (container) (typed FeaturePython)
  n = 1
  ref = Tl_element
FEATURE [App::DocumentObjectGroupPython] Cl_element026  label="Cl_element : 013"  # scripted group (container) (typed FeaturePython)
  n = 1
  ref = Cl_element
FEATURE [App::DocumentObjectGroupPython] G4_THALLIUM_CHLORIDE  # scripted group (container) (typed FeaturePython)
  Dunit = g/cm3
  Dvalue = 7.004
  Group = -> [Tl_element001,Cl_element026]
  conduct = 2
  density = 1
  expand = 3
  formula = G4_THALLIUM_CHLORIDE
  name = G4_THALLIUM_CHLORIDE
  specific = 4
FEATURE [App::DocumentObjectGroupPython] H_element100  label="H_element : 0.147"  # scripted group (container) (typed FeaturePython)
  n = 0.105
FEATURE [App::DocumentObjectGroupPython] C_element110  label="C_element : 0.256"  # scripted group (container) (typed FeaturePython)
  n = 0.256
FEATURE [App::DocumentObjectGroupPython] N_element042  label="N_element : 0.760"  # scripted group (container) (typed FeaturePython)
  n = 0.027
FEATURE [App::DocumentObjectGroupPython] O_element094  label="O_element : 0.602"  # scripted group (container) (typed FeaturePython)
  n = 0.602
FEATURE [App::DocumentObjectGroupPython] Na_element019  label="Na_element : 0.102"  # scripted group (container) (typed FeaturePython)
  n = 0.001
FEATURE [App::DocumentObjectGroupPython] P_element011  label="P_element : 0.109"  # scripted group (container) (typed FeaturePython)
  n = 0.002
FEATURE [App::DocumentObjectGroupPython] S_element022  label="S_element : 0.023"  # scripted group (container) (typed FeaturePython)
  n = 0.003
FEATURE [App::DocumentObjectGroupPython] Cl_element027  label="Cl_element : 0.591"  # scripted group (container) (typed FeaturePython)
  n = 0.002
FEATURE [App::DocumentObjectGroupPython] K_element012  label="K_element : 0.018"  # scripted group (container) (typed FeaturePython)
  n = 0.002
FEATURE [App::DocumentObjectGroupPython] G4_TISSUE_SOFT_ICRP  # scripted group (container) (typed FeaturePython)
  Dunit = g/cm3
  Dvalue = 1.03
  Group = -> [H_element100,C_element110,N_element042,O_element094,Na_element019,P_element011,S_element022,Cl_element027,K_element012]
  conduct = 2
  density = 1
  expand = 3
  formula = G4_TISSUE_SOFT_ICRP
  name = G4_TISSUE_SOFT_ICRP
  specific = 4
FEATURE [App::DocumentObjectGroupPython] H_element101  label="H_element : 0.148"  # scripted group (container) (typed FeaturePython)
  n = 0.101
FEATURE [App::DocumentObjectGroupPython] C_element111  label="C_element : 0.111"  # scripted group (container) (typed FeaturePython)
  n = 0.111
FEATURE [App::DocumentObjectGroupPython] N_element043  label="N_element : 0.026"  # scripted group (container) (typed FeaturePython)
  n = 0.026
FEATURE [App::DocumentObjectGroupPython] O_element095  label="O_element : 0.762"  # scripted group (container) (typed FeaturePython)
  n = 0.762
FEATURE [App::DocumentObjectGroupPython] G4_TISSUE_SOFT_ICRU_4  label="G4_TISSUE_SOFT_ICRU-4"  # scripted group (container) (typed FeaturePython)
  Dunit = g/cm3
  Dvalue = 1
  Group = -> [H_element101,C_element111,N_element043,O_element095]
  conduct = 2
  density = 1
  expand = 3
  formula = G4_TISSUE_SOFT_ICRU-4
  name = G4_TISSUE_SOFT_ICRU-4
  specific = 4
FEATURE [App::DocumentObjectGroupPython] H_element102  label="H_element : 0.149"  # scripted group (container) (typed FeaturePython)
  n = 0.101869
FEATURE [App::DocumentObjectGroupPython] C_element112  label="C_element : 0.456"  # scripted group (container) (typed FeaturePython)
  n = 0.456179
FEATURE [App::DocumentObjectGroupPython] N_element044  label="N_element : 0.761"  # scripted group (container) (typed FeaturePython)
  n = 0.035172
FEATURE [App::DocumentObjectGroupPython] O_element096  label="O_element : 0.407"  # scripted group (container) (typed FeaturePython)
  n = 0.40678
FEATURE [App::DocumentObjectGroupPython] G4_TISSUE_METHANE  label="G4_TISSUE-METHANE"  # scripted group (container) (typed FeaturePython)
  Dunit = g/cm3
  Dvalue = 0.00106409
  Group = -> [H_element102,C_element112,N_element044,O_element096]
  conduct = 2
  density = 1
  expand = 3
  formula = G4_TISSUE-METHANE
  name = G4_TISSUE-METHANE
  specific = 4
FEATURE [App::DocumentObjectGroupPython] H_element103  label="H_element : 0.103"  # scripted group (container) (typed FeaturePython)
  n = 0.102672
FEATURE [App::DocumentObjectGroupPython] C_element113  label="C_element : 0.569"  # scripted group (container) (typed FeaturePython)
  n = 0.56894
FEATURE [App::DocumentObjectGroupPython] N_element045  label="N_element : 0.762"  # scripted group (container) (typed FeaturePython)
  n = 0.035022
FEATURE [App::DocumentObjectGroupPython] O_element097  label="O_element : 0.293"  # scripted group (container) (typed FeaturePython)
  n = 0.293366
FEATURE [App::DocumentObjectGroupPython] G4_TISSUE_PROPANE  label="G4_TISSUE-PROPANE"  # scripted group (container) (typed FeaturePython)
  Dunit = g/cm3
  Dvalue = 0.00182628
  Group = -> [H_element103,C_element113,N_element045,O_element097]
  conduct = 2
  density = 1
  expand = 3
  formula = G4_TISSUE-PROPANE
  name = G4_TISSUE-PROPANE
  specific = 4
FEATURE [App::DocumentObjectGroupPython] Ti_element003  label="Ti_element : 1"  # scripted group (container) (typed FeaturePython)
  n = 1
  ref = Ti_element
FEATURE [App::DocumentObjectGroupPython] O_element098  label="O_element : 052"  # scripted group (container) (typed FeaturePython)
  n = 2
  ref = O_element
FEATURE [App::DocumentObjectGroupPython] G4_TITANIUM_DIOXIDE  # scripted group (container) (typed FeaturePython)
  Dunit = g/cm3
  Dvalue = 4.26
  Group = -> [Ti_element003,O_element098]
  conduct = 2
  density = 1
  expand = 3
  formula = G4_TITANIUM_DIOXIDE
  name = G4_TITANIUM_DIOXIDE
  specific = 4
FEATURE [App::DocumentObjectGroupPython] C_element114  label="C_element : 061"  # scripted group (container) (typed FeaturePython)
  n = 7
  ref = C_element
FEATURE [App::DocumentObjectGroupPython] H_element104  label="H_element : 055"  # scripted group (container) (typed FeaturePython)
  n = 8
  ref = H_element
FEATURE [App::DocumentObjectGroupPython] G4_TOLUENE  # scripted group (container) (typed FeaturePython)
  Dunit = g/cm3
  Dvalue = 0.8669
  Group = -> [C_element114,H_element104]
  conduct = 2
  density = 1
  expand = 3
  formula = G4_TOLUENE
  name = G4_TOLUENE
  specific = 4
FEATURE [App::DocumentObjectGroupPython] C_element115  label="C_element : 062"  # scripted group (container) (typed FeaturePython)
  n = 2
  ref = C_element
FEATURE [App::DocumentObjectGroupPython] H_element105  label="H_element : 056"  # scripted group (container) (typed FeaturePython)
  n = 1
  ref = H_element
FEATURE [App::DocumentObjectGroupPython] Cl_element028  label="Cl_element : 014"  # scripted group (container) (typed FeaturePython)
  n = 3
  ref = Cl_element
FEATURE [App::DocumentObjectGroupPython] G4_TRICHLOROETHYLENE  # scripted group (container) (typed FeaturePython)
  Dunit = g/cm3
  Dvalue = 1.46
  Group = -> [C_element115,H_element105,Cl_element028]
  conduct = 2
  density = 1
  expand = 3
  formula = G4_TRICHLOROETHYLENE
  name = G4_TRICHLOROETHYLENE
  specific = 4
FEATURE [App::DocumentObjectGroupPython] C_element116  label="C_element : 063"  # scripted group (container) (typed FeaturePython)
  n = 6
  ref = C_element
FEATURE [App::DocumentObjectGroupPython] H_element106  label="H_element : 15"  # scripted group (container) (typed FeaturePython)
  n = 15
  ref = H_element
FEATURE [App::DocumentObjectGroupPython] O_element099  label="O_element : 053"  # scripted group (container) (typed FeaturePython)
  n = 4
  ref = O_element
FEATURE [App::DocumentObjectGroupPython] P_element012  label="P_element : 1"  # scripted group (container) (typed FeaturePython)
  n = 1
  ref = P_element
FEATURE [App::DocumentObjectGroupPython] G4_TRIETHYL_PHOSPHATE  # scripted group (container) (typed FeaturePython)
  Dunit = g/cm3
  Dvalue = 1.07
  Group = -> [C_element116,H_element106,O_element099,P_element012]
  conduct = 2
  density = 1
  expand = 3
  formula = G4_TRIETHYL_PHOSPHATE
  name = G4_TRIETHYL_PHOSPHATE
  specific = 4
FEATURE [App::DocumentObjectGroupPython] W_element003  label="W_element : 003"  # scripted group (container) (typed FeaturePython)
  n = 1
  ref = W_element
FEATURE [App::DocumentObjectGroupPython] F_element017  label="F_element : 6"  # scripted group (container) (typed FeaturePython)
  n = 6
  ref = F_element
FEATURE [App::DocumentObjectGroupPython] G4_TUNGSTEN_HEXAFLUORIDE  # scripted group (container) (typed FeaturePython)
  Dunit = g/cm3
  Dvalue = 2.4
  Group = -> [W_element003,F_element017]
  conduct = 2
  density = 1
  expand = 3
  formula = G4_TUNGSTEN_HEXAFLUORIDE
  name = G4_TUNGSTEN_HEXAFLUORIDE
  specific = 4
FEATURE [App::DocumentObjectGroupPython] U_element001  label="U_element : 1"  # scripted group (container) (typed FeaturePython)
  n = 1
  ref = U_element
FEATURE [App::DocumentObjectGroupPython] C_element117  label="C_element : 064"  # scripted group (container) (typed FeaturePython)
  n = 2
  ref = C_element
FEATURE [App::DocumentObjectGroupPython] G4_URANIUM_DICARBIDE  # scripted group (container) (typed FeaturePython)
  Dunit = g/cm3
  Dvalue = 11.28
  Group = -> [U_element001,C_element117]
  conduct = 2
  density = 1
  expand = 3
  formula = G4_URANIUM_DICARBIDE
  name = G4_URANIUM_DICARBIDE
  specific = 4
FEATURE [App::DocumentObjectGroupPython] U_element002  label="U_element : 002"  # scripted group (container) (typed FeaturePython)
  n = 1
  ref = U_element
FEATURE [App::DocumentObjectGroupPython] C_element118  label="C_element : 065"  # scripted group (container) (typed FeaturePython)
  n = 1
  ref = C_element
FEATURE [App::DocumentObjectGroupPython] G4_URANIUM_MONOCARBIDE  # scripted group (container) (typed FeaturePython)
  Dunit = g/cm3
  Dvalue = 13.63
  Group = -> [U_element002,C_element118]
  conduct = 2
  density = 1
  expand = 3
  formula = G4_URANIUM_MONOCARBIDE
  name = G4_URANIUM_MONOCARBIDE
  specific = 4
FEATURE [App::DocumentObjectGroupPython] U_element003  label="U_element : 003"  # scripted group (container) (typed FeaturePython)
  n = 1
  ref = U_element
FEATURE [App::DocumentObjectGroupPython] O_element100  label="O_element : 054"  # scripted group (container) (typed FeaturePython)
  n = 2
  ref = O_element
FEATURE [App::DocumentObjectGroupPython] G4_URANIUM_OXIDE  # scripted group (container) (typed FeaturePython)
  Dunit = g/cm3
  Dvalue = 10.96
  Group = -> [U_element003,O_element100]
  conduct = 2
  density = 1
  expand = 3
  formula = G4_URANIUM_OXIDE
  name = G4_URANIUM_OXIDE
  specific = 4
FEATURE [App::DocumentObjectGroupPython] C_element119  label="C_element : 066"  # scripted group (container) (typed FeaturePython)
  n = 1
  ref = C_element
FEATURE [App::DocumentObjectGroupPython] H_element107  label="H_element : 057"  # scripted group (container) (typed FeaturePython)
  n = 4
  ref = H_element
FEATURE [App::DocumentObjectGroupPython] N_element046  label="N_element : 019"  # scripted group (container) (typed FeaturePython)
  n = 2
  ref = N_element
FEATURE [App::DocumentObjectGroupPython] O_element101  label="O_element : 055"  # scripted group (container) (typed FeaturePython)
  n = 1
  ref = O_element
FEATURE [App::DocumentObjectGroupPython] G4_UREA  # scripted group (container) (typed FeaturePython)
  Dunit = g/cm3
  Dvalue = 1.323
  Group = -> [C_element119,H_element107,N_element046,O_element101]
  conduct = 2
  density = 1
  expand = 3
  formula = G4_UREA
  name = G4_UREA
  specific = 4
FEATURE [App::DocumentObjectGroupPython] C_element120  label="C_element : 067"  # scripted group (container) (typed FeaturePython)
  n = 5
  ref = C_element
FEATURE [App::DocumentObjectGroupPython] H_element108  label="H_element : 058"  # scripted group (container) (typed FeaturePython)
  n = 11
  ref = H_element
FEATURE [App::DocumentObjectGroupPython] N_element047  label="N_element : 020"  # scripted group (container) (typed FeaturePython)
  n = 1
  ref = N_element
FEATURE [App::DocumentObjectGroupPython] O_element102  label="O_element : 056"  # scripted group (container) (typed FeaturePython)
  n = 2
  ref = O_element
FEATURE [App::DocumentObjectGroupPython] G4_VALINE  # scripted group (container) (typed FeaturePython)
  Dunit = g/cm3
  Dvalue = 1.23
  Group = -> [C_element120,H_element108,N_element047,O_element102]
  conduct = 2
  density = 1
  expand = 3
  formula = G4_VALINE
  name = G4_VALINE
  specific = 4
FEATURE [App::DocumentObjectGroupPython] H_element109  label="H_element : 0.009"  # scripted group (container) (typed FeaturePython)
  n = 0.009417
FEATURE [App::DocumentObjectGroupPython] C_element121  label="C_element : 0.281"  # scripted group (container) (typed FeaturePython)
  n = 0.280555
FEATURE [App::DocumentObjectGroupPython] F_element018  label="F_element : 0.710"  # scripted group (container) (typed FeaturePython)
  n = 0.710028
FEATURE [App::DocumentObjectGroupPython] G4_VITON  # scripted group (container) (typed FeaturePython)
  Dunit = g/cm3
  Dvalue = 1.8
  Group = -> [H_element109,C_element121,F_element018]
  conduct = 2
  density = 1
  expand = 3
  formula = G4_VITON
  name = G4_VITON
  specific = 4
FEATURE [App::DocumentObjectGroupPython] H_element110  label="H_element : 059"  # scripted group (container) (typed FeaturePython)
  n = 2
  ref = H_element
FEATURE [App::DocumentObjectGroupPython] O_element103  label="O_element : 057"  # scripted group (container) (typed FeaturePython)
  n = 1
  ref = O_element
FEATURE [App::DocumentObjectGroupPython] G4_WATER  # scripted group (container) (typed FeaturePython)
  Dunit = g/cm3
  Dvalue = 1
  Group = -> [H_element110,O_element103]
  conduct = 2
  density = 1
  expand = 3
  formula = G4_WATER
  name = G4_WATER
  specific = 4
FEATURE [App::DocumentObjectGroupPython] H_element111  label="H_element : 060"  # scripted group (container) (typed FeaturePython)
  n = 2
  ref = H_element
FEATURE [App::DocumentObjectGroupPython] O_element104  label="O_element : 058"  # scripted group (container) (typed FeaturePython)
  n = 1
  ref = O_element
FEATURE [App::DocumentObjectGroupPython] G4_WATER_VAPOR  # scripted group (container) (typed FeaturePython)
  Dunit = g/cm3
  Dvalue = 0.000756182
  Group = -> [H_element111,O_element104]
  conduct = 2
  density = 1
  expand = 3
  formula = G4_WATER_VAPOR
  name = G4_WATER_VAPOR
  specific = 4
FEATURE [App::DocumentObjectGroupPython] C_element122  label="C_element : 068"  # scripted group (container) (typed FeaturePython)
  n = 8
  ref = C_element
FEATURE [App::DocumentObjectGroupPython] H_element112  label="H_element : 061"  # scripted group (container) (typed FeaturePython)
  n = 10
  ref = H_element
FEATURE [App::DocumentObjectGroupPython] G4_XYLENE  # scripted group (container) (typed FeaturePython)
  Dunit = g/cm3
  Dvalue = 0.87
  Group = -> [C_element122,H_element112]
  conduct = 2
  density = 1
  expand = 3
  formula = G4_XYLENE
  name = G4_XYLENE
  specific = 4
FEATURE [App::DocumentObjectGroupPython] C_element123  label="C_element : 069"  # scripted group (container) (typed FeaturePython)
  n = 1
  ref = C_element
FEATURE [App::DocumentObjectGroupPython] G4_GRAPHITE  # scripted group (container) (typed FeaturePython)
  Dunit = g/cm3
  Dvalue = 2.21
  Group = -> [C_element123]
  conduct = 2
  density = 1
  expand = 3
  formula = G4_GRAPHITE
  name = G4_GRAPHITE
  specific = 4
FEATURE [App::DocumentObjectGroupPython] NIST  # scripted group (container) (typed FeaturePython)
  Group = -> [G4_A_150_TISSUE,G4_ACETONE,G4_ACETYLENE,G4_ADENINE,G4_ADIPOSE_TISSUE_ICRP,G4_AIR001,G4_ALANINE,G4_ALUMINUM_OXIDE,G4_AMBER,G4_AMMONIA,G4_ANILINE,G4_ANTHRACENE,G4_B_100_BONE,G4_BAKELITE,G4_BARIUM_FLUORIDE,G4_BARIUM_SULFATE,G4_BENZENE,G4_BERYLLIUM_OXIDE,G4_BGO,G4_BLOOD_ICRP,G4_BONE_COMPACT_ICRU,G4_BONE_CORTICAL_ICRP,G4_BORON_CARBIDE,G4_BORON_OXIDE,G4_BRAIN_ICRP,G4_BUTANE,G4_N_BUTYL_ALCOHOL,G4_C_552,+152 more]
FEATURE [App::DocumentObjectGroupPython] H_element113  label="H_element : 062"  # scripted group (container) (typed FeaturePython)
  n = 1
  ref = H_element
FEATURE [App::DocumentObjectGroupPython] G4_H  # scripted group (container) (typed FeaturePython)
  Dunit = g/cm3
  Dvalue = 8.3748e-05
  Group = -> [H_element113]
  conduct = 2
  density = 1
  expand = 3
  formula = H
  name = G4_H
  specific = 4
FEATURE [App::DocumentObjectGroupPython] He_element001  label="He_element : 1"  # scripted group (container) (typed FeaturePython)
  n = 1
  ref = He_element
FEATURE [App::DocumentObjectGroupPython] G4_He  # scripted group (container) (typed FeaturePython)
  Dunit = g/cm3
  Dvalue = 0.000166322
  Group = -> [He_element001]
  conduct = 2
  density = 1
  expand = 3
  formula = He
  name = G4_He
  specific = 4
FEATURE [App::DocumentObjectGroupPython] Li_element008  label="Li_element : 008"  # scripted group (container) (typed FeaturePython)
  n = 1
  ref = Li_element
FEATURE [App::DocumentObjectGroupPython] G4_Li  # scripted group (container) (typed FeaturePython)
  Dunit = g/cm3
  Dvalue = 0.534
  Group = -> [Li_element008]
  conduct = 2
  density = 1
  expand = 3
  formula = Li
  name = G4_Li
  specific = 4
FEATURE [App::DocumentObjectGroupPython] Be_element002  label="Be_element : 002"  # scripted group (container) (typed FeaturePython)
  n = 1
  ref = Be_element
FEATURE [App::DocumentObjectGroupPython] G4_Be  # scripted group (container) (typed FeaturePython)
  Dunit = g/cm3
  Dvalue = 1.848
  Group = -> [Be_element002]
  conduct = 2
  density = 1
  expand = 3
  formula = Be
  name = G4_Be
  specific = 4
FEATURE [App::DocumentObjectGroupPython] B_element007  label="B_element : 007"  # scripted group (container) (typed FeaturePython)
  n = 1
  ref = B_element
FEATURE [App::DocumentObjectGroupPython] G4_B  # scripted group (container) (typed FeaturePython)
  Dunit = g/cm3
  Dvalue = 2.37
  Group = -> [B_element007]
  conduct = 2
  density = 1
  expand = 3
  formula = B
  name = G4_B
  specific = 4
FEATURE [App::DocumentObjectGroupPython] C_element124  label="C_element : 070"  # scripted group (container) (typed FeaturePython)
  n = 1
  ref = C_element
FEATURE [App::DocumentObjectGroupPython] G4_C  # scripted group (container) (typed FeaturePython)
  Dunit = g/cm3
  Dvalue = 2
  Group = -> [C_element124]
  conduct = 2
  density = 1
  expand = 3
  formula = C
  name = G4_C
  specific = 4
FEATURE [App::DocumentObjectGroupPython] N_element048  label="N_element : 021"  # scripted group (container) (typed FeaturePython)
  n = 1
  ref = N_element
FEATURE [App::DocumentObjectGroupPython] G4_N  # scripted group (container) (typed FeaturePython)
  Dunit = g/cm3
  Dvalue = 0.0011652
  Group = -> [N_element048]
  conduct = 2
  density = 1
  expand = 3
  formula = N
  name = G4_N
  specific = 4
FEATURE [App::DocumentObjectGroupPython] O_element105  label="O_element : 059"  # scripted group (container) (typed FeaturePython)
  n = 1
  ref = O_element
FEATURE [App::DocumentObjectGroupPython] G4_O  # scripted group (container) (typed FeaturePython)
  Dunit = g/cm3
  Dvalue = 0.00133151
  Group = -> [O_element105]
  conduct = 2
  density = 1
  expand = 3
  formula = O
  name = G4_O
  specific = 4
FEATURE [App::DocumentObjectGroupPython] F_element019  label="F_element : 008"  # scripted group (container) (typed FeaturePython)
  n = 1
  ref = F_element
FEATURE [App::DocumentObjectGroupPython] G4_F  # scripted group (container) (typed FeaturePython)
  Dunit = g/cm3
  Dvalue = 0.00158029
  Group = -> [F_element019]
  conduct = 2
  density = 1
  expand = 3
  formula = F
  name = G4_F
  specific = 4
FEATURE [App::DocumentObjectGroupPython] Ne_element001  label="Ne_element : 1"  # scripted group (container) (typed FeaturePython)
  n = 1
  ref = Ne_element
FEATURE [App::DocumentObjectGroupPython] G4_Ne  # scripted group (container) (typed FeaturePython)
  Dunit = g/cm3
  Dvalue = 0.000838505
  Group = -> [Ne_element001]
  conduct = 2
  density = 1
  expand = 3
  formula = Ne
  name = G4_Ne
  specific = 4
FEATURE [App::DocumentObjectGroupPython] Na_element020  label="Na_element : 005"  # scripted group (container) (typed FeaturePython)
  n = 1
  ref = Na_element
FEATURE [App::DocumentObjectGroupPython] G4_Na  # scripted group (container) (typed FeaturePython)
  Dunit = g/cm3
  Dvalue = 0.971
  Group = -> [Na_element020]
  conduct = 2
  density = 1
  expand = 3
  formula = Na
  name = G4_Na
  specific = 4
FEATURE [App::DocumentObjectGroupPython] Mg_element011  label="Mg_element : 005"  # scripted group (container) (typed FeaturePython)
  n = 1
  ref = Mg_element
FEATURE [App::DocumentObjectGroupPython] G4_Mg  # scripted group (container) (typed FeaturePython)
  Dunit = g/cm3
  Dvalue = 1.74
  Group = -> [Mg_element011]
  conduct = 2
  density = 1
  expand = 3
  formula = Mg
  name = G4_Mg
  specific = 4
FEATURE [App::DocumentObjectGroupPython] Al_element004  label="Al_element : 1"  # scripted group (container) (typed FeaturePython)
  n = 1
  ref = Al_element
FEATURE [App::DocumentObjectGroupPython] G4_Al  # scripted group (container) (typed FeaturePython)
  Dunit = g/cm3
  Dvalue = 2.699
  Group = -> [Al_element004]
  conduct = 2
  density = 1
  expand = 3
  formula = Al
  name = G4_Al
  specific = 4
FEATURE [App::DocumentObjectGroupPython] Si_element007  label="Si_element : 002"  # scripted group (container) (typed FeaturePython)
  n = 1
  ref = Si_element
FEATURE [App::DocumentObjectGroupPython] G4_Si  # scripted group (container) (typed FeaturePython)
  Dunit = g/cm3
  Dvalue = 2.33
  Group = -> [Si_element007]
  conduct = 2
  density = 1
  expand = 3
  formula = Si
  name = G4_Si
  specific = 4
FEATURE [App::DocumentObjectGroupPython] P_element013  label="P_element : 002"  # scripted group (container) (typed FeaturePython)
  n = 1
  ref = P_element
FEATURE [App::DocumentObjectGroupPython] G4_P  # scripted group (container) (typed FeaturePython)
  Dunit = g/cm3
  Dvalue = 2.2
  Group = -> [P_element013]
  conduct = 2
  density = 1
  expand = 3
  formula = P
  name = G4_P
  specific = 4
FEATURE [App::DocumentObjectGroupPython] S_element023  label="S_element : 007"  # scripted group (container) (typed FeaturePython)
  n = 1
  ref = S_element
FEATURE [App::DocumentObjectGroupPython] G4_S  # scripted group (container) (typed FeaturePython)
  Dunit = g/cm3
  Dvalue = 2
  Group = -> [S_element023]
  conduct = 2
  density = 1
  expand = 3
  formula = S
  name = G4_S
  specific = 4
FEATURE [App::DocumentObjectGroupPython] Cl_element029  label="Cl_element : 015"  # scripted group (container) (typed FeaturePython)
  n = 1
  ref = Cl_element
FEATURE [App::DocumentObjectGroupPython] G4_Cl  # scripted group (container) (typed FeaturePython)
  Dunit = g/cm3
  Dvalue = 0.00299473
  Group = -> [Cl_element029]
  conduct = 2
  density = 1
  expand = 3
  formula = Cl
  name = G4_Cl
  specific = 4
FEATURE [App::DocumentObjectGroupPython] Ar_element002  label="Ar_element : 1"  # scripted group (container) (typed FeaturePython)
  n = 1
  ref = Ar_element
FEATURE [App::DocumentObjectGroupPython] G4_Ar  # scripted group (container) (typed FeaturePython)
  Dunit = g/cm3
  Dvalue = 0.00166201
  Group = -> [Ar_element002]
  conduct = 2
  density = 1
  expand = 3
  formula = Ar
  name = G4_Ar
  specific = 4
FEATURE [App::DocumentObjectGroupPython] K_element013  label="K_element : 003"  # scripted group (container) (typed FeaturePython)
  n = 1
  ref = K_element
FEATURE [App::DocumentObjectGroupPython] G4_K  # scripted group (container) (typed FeaturePython)
  Dunit = g/cm3
  Dvalue = 0.862
  Group = -> [K_element013]
  conduct = 2
  density = 1
  expand = 3
  formula = K
  name = G4_K
  specific = 4
FEATURE [App::DocumentObjectGroupPython] Ca_element014  label="Ca_element : 007"  # scripted group (container) (typed FeaturePython)
  n = 1
  ref = Ca_element
FEATURE [App::DocumentObjectGroupPython] G4_Ca  # scripted group (container) (typed FeaturePython)
  Dunit = g/cm3
  Dvalue = 1.55
  Group = -> [Ca_element014]
  conduct = 2
  density = 1
  expand = 3
  formula = Ca
  name = G4_Ca
  specific = 4
FEATURE [App::DocumentObjectGroupPython] Sc_element001  label="Sc_element : 1"  # scripted group (container) (typed FeaturePython)
  n = 1
  ref = Sc_element
FEATURE [App::DocumentObjectGroupPython] G4_Sc  # scripted group (container) (typed FeaturePython)
  Dunit = g/cm3
  Dvalue = 2.989
  Group = -> [Sc_element001]
  conduct = 2
  density = 1
  expand = 3
  formula = Sc
  name = G4_Sc
  specific = 4
FEATURE [App::DocumentObjectGroupPython] Ti_element004  label="Ti_element : 002"  # scripted group (container) (typed FeaturePython)
  n = 1
  ref = Ti_element
FEATURE [App::DocumentObjectGroupPython] G4_Ti  # scripted group (container) (typed FeaturePython)
  Dunit = g/cm3
  Dvalue = 4.54
  Group = -> [Ti_element004]
  conduct = 2
  density = 1
  expand = 3
  formula = Ti
  name = G4_Ti
  specific = 4
FEATURE [App::DocumentObjectGroupPython] V_element001  label="V_element : 1"  # scripted group (container) (typed FeaturePython)
  n = 1
  ref = V_element
FEATURE [App::DocumentObjectGroupPython] G4_V  # scripted group (container) (typed FeaturePython)
  Dunit = g/cm3
  Dvalue = 6.11
  Group = -> [V_element001]
  conduct = 2
  density = 1
  expand = 3
  formula = V
  name = G4_V
  specific = 4
FEATURE [App::DocumentObjectGroupPython] Cr_element001  label="Cr_element : 1"  # scripted group (container) (typed FeaturePython)
  n = 1
  ref = Cr_element
FEATURE [App::DocumentObjectGroupPython] G4_Cr  # scripted group (container) (typed FeaturePython)
  Dunit = g/cm3
  Dvalue = 7.18
  Group = -> [Cr_element001]
  conduct = 2
  density = 1
  expand = 3
  formula = Cr
  name = G4_Cr
  specific = 4
FEATURE [App::DocumentObjectGroupPython] Mn_element001  label="Mn_element : 1"  # scripted group (container) (typed FeaturePython)
  n = 1
  ref = Mn_element
FEATURE [App::DocumentObjectGroupPython] G4_Mn  # scripted group (container) (typed FeaturePython)
  Dunit = g/cm3
  Dvalue = 7.44
  Group = -> [Mn_element001]
  conduct = 2
  density = 1
  expand = 3
  formula = Mn
  name = G4_Mn
  specific = 4
FEATURE [App::DocumentObjectGroupPython] Fe_element007  label="Fe_element : 004"  # scripted group (container) (typed FeaturePython)
  n = 1
  ref = Fe_element
FEATURE [App::DocumentObjectGroupPython] G4_Fe  # scripted group (container) (typed FeaturePython)
  Dunit = g/cm3
  Dvalue = 7.874
  Group = -> [Fe_element007]
  conduct = 2
  density = 1
  expand = 3
  formula = Fe
  name = G4_Fe
  specific = 4
FEATURE [App::DocumentObjectGroupPython] Co_element001  label="Co_element : 1"  # scripted group (container) (typed FeaturePython)
  n = 1
  ref = Co_element
FEATURE [App::DocumentObjectGroupPython] G4_Co  # scripted group (container) (typed FeaturePython)
  Dunit = g/cm3
  Dvalue = 8.9
  Group = -> [Co_element001]
  conduct = 2
  density = 1
  expand = 3
  formula = Co
  name = G4_Co
  specific = 4
FEATURE [App::DocumentObjectGroupPython] Ni_element001  label="Ni_element : 1"  # scripted group (container) (typed FeaturePython)
  n = 1
  ref = Ni_element
FEATURE [App::DocumentObjectGroupPython] G4_Ni  # scripted group (container) (typed FeaturePython)
  Dunit = g/cm3
  Dvalue = 8.902
  Group = -> [Ni_element001]
  conduct = 2
  density = 1
  expand = 3
  formula = Ni
  name = G4_Ni
  specific = 4
FEATURE [App::DocumentObjectGroupPython] Cu_element001  label="Cu_element : 1"  # scripted group (container) (typed FeaturePython)
  n = 1
  ref = Cu_element
FEATURE [App::DocumentObjectGroupPython] G4_Cu  # scripted group (container) (typed FeaturePython)
  Dunit = g/cm3
  Dvalue = 8.96
  Group = -> [Cu_element001]
  conduct = 2
  density = 1
  expand = 3
  formula = Cu
  name = G4_Cu
  specific = 4
FEATURE [App::DocumentObjectGroupPython] Zn_element001  label="Zn_element : 1"  # scripted group (container) (typed FeaturePython)
  n = 1
  ref = Zn_element
FEATURE [App::DocumentObjectGroupPython] G4_Zn  # scripted group (container) (typed FeaturePython)
  Dunit = g/cm3
  Dvalue = 7.133
  Group = -> [Zn_element001]
  conduct = 2
  density = 1
  expand = 3
  formula = Zn
  name = G4_Zn
  specific = 4
FEATURE [App::DocumentObjectGroupPython] Ga_element002  label="Ga_element : 002"  # scripted group (container) (typed FeaturePython)
  n = 1
  ref = Ga_element
FEATURE [App::DocumentObjectGroupPython] G4_Ga  # scripted group (container) (typed FeaturePython)
  Dunit = g/cm3
  Dvalue = 5.904
  Group = -> [Ga_element002]
  conduct = 2
  density = 1
  expand = 3
  formula = Ga
  name = G4_Ga
  specific = 4
FEATURE [App::DocumentObjectGroupPython] Ge_element002  label="Ge_element : 1"  # scripted group (container) (typed FeaturePython)
  n = 1
  ref = Ge_element
FEATURE [App::DocumentObjectGroupPython] G4_Ge  # scripted group (container) (typed FeaturePython)
  Dunit = g/cm3
  Dvalue = 5.323
  Group = -> [Ge_element002]
  conduct = 2
  density = 1
  expand = 3
  formula = Ge
  name = G4_Ge
  specific = 4
FEATURE [App::DocumentObjectGroupPython] As_element003  label="As_element : 002"  # scripted group (container) (typed FeaturePython)
  n = 1
  ref = As_element
FEATURE [App::DocumentObjectGroupPython] G4_As  # scripted group (container) (typed FeaturePython)
  Dunit = g/cm3
  Dvalue = 5.73
  Group = -> [As_element003]
  conduct = 2
  density = 1
  expand = 3
  formula = As
  name = G4_As
  specific = 4
FEATURE [App::DocumentObjectGroupPython] Se_element001  label="Se_element : 1"  # scripted group (container) (typed FeaturePython)
  n = 1
  ref = Se_element
FEATURE [App::DocumentObjectGroupPython] G4_Se  # scripted group (container) (typed FeaturePython)
  Dunit = g/cm3
  Dvalue = 4.5
  Group = -> [Se_element001]
  conduct = 2
  density = 1
  expand = 3
  formula = Se
  name = G4_Se
  specific = 4
FEATURE [App::DocumentObjectGroupPython] Br_element007  label="Br_element : 004"  # scripted group (container) (typed FeaturePython)
  n = 1
  ref = Br_element
FEATURE [App::DocumentObjectGroupPython] G4_Br  # scripted group (container) (typed FeaturePython)
  Dunit = g/cm3
  Dvalue = 0.0070721
  Group = -> [Br_element007]
  conduct = 2
  density = 1
  expand = 3
  formula = Br
  name = G4_Br
  specific = 4
FEATURE [App::DocumentObjectGroupPython] Kr_element001  label="Kr_element : 1"  # scripted group (container) (typed FeaturePython)
  n = 1
  ref = Kr_element
FEATURE [App::DocumentObjectGroupPython] G4_Kr  # scripted group (container) (typed FeaturePython)
  Dunit = g/cm3
  Dvalue = 0.00347832
  Group = -> [Kr_element001]
  conduct = 2
  density = 1
  expand = 3
  formula = Kr
  name = G4_Kr
  specific = 4
FEATURE [App::DocumentObjectGroupPython] Rb_element001  label="Rb_element : 1"  # scripted group (container) (typed FeaturePython)
  n = 1
  ref = Rb_element
FEATURE [App::DocumentObjectGroupPython] G4_Rb  # scripted group (container) (typed FeaturePython)
  Dunit = g/cm3
  Dvalue = 1.532
  Group = -> [Rb_element001]
  conduct = 2
  density = 1
  expand = 3
  formula = Rb
  name = G4_Rb
  specific = 4
FEATURE [App::DocumentObjectGroupPython] Sr_element001  label="Sr_element : 1"  # scripted group (container) (typed FeaturePython)
  n = 1
  ref = Sr_element
FEATURE [App::DocumentObjectGroupPython] G4_Sr  # scripted group (container) (typed FeaturePython)
  Dunit = g/cm3
  Dvalue = 2.54
  Group = -> [Sr_element001]
  conduct = 2
  density = 1
  expand = 3
  formula = Sr
  name = G4_Sr
  specific = 4
FEATURE [App::DocumentObjectGroupPython] Y_element001  label="Y_element : 1"  # scripted group (container) (typed FeaturePython)
  n = 1
  ref = Y_element
FEATURE [App::DocumentObjectGroupPython] G4_Y  # scripted group (container) (typed FeaturePython)
  Dunit = g/cm3
  Dvalue = 4.469
  Group = -> [Y_element001]
  conduct = 2
  density = 1
  expand = 3
  formula = Y
  name = G4_Y
  specific = 4
FEATURE [App::DocumentObjectGroupPython] Zr_element001  label="Zr_element : 1"  # scripted group (container) (typed FeaturePython)
  n = 1
  ref = Zr_element
FEATURE [App::DocumentObjectGroupPython] G4_Zr  # scripted group (container) (typed FeaturePython)
  Dunit = g/cm3
  Dvalue = 6.506
  Group = -> [Zr_element001]
  conduct = 2
  density = 1
  expand = 3
  formula = Zr
  name = G4_Zr
  specific = 4
FEATURE [App::DocumentObjectGroupPython] Nb_element001  label="Nb_element : 1"  # scripted group (container) (typed FeaturePython)
  n = 1
  ref = Nb_element
FEATURE [App::DocumentObjectGroupPython] G4_Nb  # scripted group (container) (typed FeaturePython)
  Dunit = g/cm3
  Dvalue = 8.57
  Group = -> [Nb_element001]
  conduct = 2
  density = 1
  expand = 3
  formula = Nb
  name = G4_Nb
  specific = 4
FEATURE [App::DocumentObjectGroupPython] Mo_element001  label="Mo_element : 1"  # scripted group (container) (typed FeaturePython)
  n = 1
  ref = Mo_element
FEATURE [App::DocumentObjectGroupPython] G4_Mo  # scripted group (container) (typed FeaturePython)
  Dunit = g/cm3
  Dvalue = 10.22
  Group = -> [Mo_element001]
  conduct = 2
  density = 1
  expand = 3
  formula = Mo
  name = G4_Mo
  specific = 4
FEATURE [App::DocumentObjectGroupPython] Tc_element001  label="Tc_element : 1"  # scripted group (container) (typed FeaturePython)
  n = 1
  ref = Tc_element
FEATURE [App::DocumentObjectGroupPython] G4_Tc  # scripted group (container) (typed FeaturePython)
  Dunit = g/cm3
  Dvalue = 11.5
  Group = -> [Tc_element001]
  conduct = 2
  density = 1
  expand = 3
  formula = Tc
  name = G4_Tc
  specific = 4
FEATURE [App::DocumentObjectGroupPython] Ru_element001  label="Ru_element : 1"  # scripted group (container) (typed FeaturePython)
  n = 1
  ref = Ru_element
FEATURE [App::DocumentObjectGroupPython] G4_Ru  # scripted group (container) (typed FeaturePython)
  Dunit = g/cm3
  Dvalue = 12.41
  Group = -> [Ru_element001]
  conduct = 2
  density = 1
  expand = 3
  formula = Ru
  name = G4_Ru
  specific = 4
FEATURE [App::DocumentObjectGroupPython] Rh_element001  label="Rh_element : 1"  # scripted group (container) (typed FeaturePython)
  n = 1
  ref = Rh_element
FEATURE [App::DocumentObjectGroupPython] G4_Rh  # scripted group (container) (typed FeaturePython)
  Dunit = g/cm3
  Dvalue = 12.41
  Group = -> [Rh_element001]
  conduct = 2
  density = 1
  expand = 3
  formula = Rh
  name = G4_Rh
  specific = 4
FEATURE [App::DocumentObjectGroupPython] Pd_element001  label="Pd_element : 1"  # scripted group (container) (typed FeaturePython)
  n = 1
  ref = Pd_element
FEATURE [App::DocumentObjectGroupPython] G4_Pd  # scripted group (container) (typed FeaturePython)
  Dunit = g/cm3
  Dvalue = 12.02
  Group = -> [Pd_element001]
  conduct = 2
  density = 1
  expand = 3
  formula = Pd
  name = G4_Pd
  specific = 4
FEATURE [App::DocumentObjectGroupPython] Ag_element006  label="Ag_element : 004"  # scripted group (container) (typed FeaturePython)
  n = 1
  ref = Ag_element
FEATURE [App::DocumentObjectGroupPython] G4_Ag  # scripted group (container) (typed FeaturePython)
  Dunit = g/cm3
  Dvalue = 10.5
  Group = -> [Ag_element006]
  conduct = 2
  density = 1
  expand = 3
  formula = Ag
  name = G4_Ag
  specific = 4
FEATURE [App::DocumentObjectGroupPython] Cd_element003  label="Cd_element : 003"  # scripted group (container) (typed FeaturePython)
  n = 1
  ref = Cd_element
FEATURE [App::DocumentObjectGroupPython] G4_Cd  # scripted group (container) (typed FeaturePython)
  Dunit = g/cm3
  Dvalue = 8.65
  Group = -> [Cd_element003]
  conduct = 2
  density = 1
  expand = 3
  formula = Cd
  name = G4_Cd
  specific = 4
FEATURE [App::DocumentObjectGroupPython] In_element001  label="In_element : 1"  # scripted group (container) (typed FeaturePython)
  n = 1
  ref = In_element
FEATURE [App::DocumentObjectGroupPython] G4_In  # scripted group (container) (typed FeaturePython)
  Dunit = g/cm3
  Dvalue = 7.31
  Group = -> [In_element001]
  conduct = 2
  density = 1
  expand = 3
  formula = In
  name = G4_In
  specific = 4
FEATURE [App::DocumentObjectGroupPython] Sn_element001  label="Sn_element : 1"  # scripted group (container) (typed FeaturePython)
  n = 1
  ref = Sn_element
FEATURE [App::DocumentObjectGroupPython] G4_Sn  # scripted group (container) (typed FeaturePython)
  Dunit = g/cm3
  Dvalue = 7.31
  Group = -> [Sn_element001]
  conduct = 2
  density = 1
  expand = 3
  formula = Sn
  name = G4_Sn
  specific = 4
FEATURE [App::DocumentObjectGroupPython] Sb_element001  label="Sb_element : 1"  # scripted group (container) (typed FeaturePython)
  n = 1
  ref = Sb_element
FEATURE [App::DocumentObjectGroupPython] G4_Sb  # scripted group (container) (typed FeaturePython)
  Dunit = g/cm3
  Dvalue = 6.691
  Group = -> [Sb_element001]
  conduct = 2
  density = 1
  expand = 3
  formula = Sb
  name = G4_Sb
  specific = 4
FEATURE [App::DocumentObjectGroupPython] Te_element002  label="Te_element : 002"  # scripted group (container) (typed FeaturePython)
  n = 1
  ref = Te_element
FEATURE [App::DocumentObjectGroupPython] G4_Te  # scripted group (container) (typed FeaturePython)
  Dunit = g/cm3
  Dvalue = 6.24
  Group = -> [Te_element002]
  conduct = 2
  density = 1
  expand = 3
  formula = Te
  name = G4_Te
  specific = 4
FEATURE [App::DocumentObjectGroupPython] I_element010  label="I_element : 006"  # scripted group (container) (typed FeaturePython)
  n = 1
  ref = I_element
FEATURE [App::DocumentObjectGroupPython] G4_I  # scripted group (container) (typed FeaturePython)
  Dunit = g/cm3
  Dvalue = 4.93
  Group = -> [I_element010]
  conduct = 2
  density = 1
  expand = 3
  formula = I
  name = G4_I
  specific = 4
FEATURE [App::DocumentObjectGroupPython] Xe_element001  label="Xe_element : 1"  # scripted group (container) (typed FeaturePython)
  n = 1
  ref = Xe_element
FEATURE [App::DocumentObjectGroupPython] G4_Xe  # scripted group (container) (typed FeaturePython)
  Dunit = g/cm3
  Dvalue = 0.00548536
  Group = -> [Xe_element001]
  conduct = 2
  density = 1
  expand = 3
  formula = Xe
  name = G4_Xe
  specific = 4
FEATURE [App::DocumentObjectGroupPython] Cs_element003  label="Cs_element : 003"  # scripted group (container) (typed FeaturePython)
  n = 1
  ref = Cs_element
FEATURE [App::DocumentObjectGroupPython] G4_Cs  # scripted group (container) (typed FeaturePython)
  Dunit = g/cm3
  Dvalue = 1.873
  Group = -> [Cs_element003]
  conduct = 2
  density = 1
  expand = 3
  formula = Cs
  name = G4_Cs
  specific = 4
FEATURE [App::DocumentObjectGroupPython] Ba_element003  label="Ba_element : 003"  # scripted group (container) (typed FeaturePython)
  n = 1
  ref = Ba_element
FEATURE [App::DocumentObjectGroupPython] G4_Ba  # scripted group (container) (typed FeaturePython)
  Dunit = g/cm3
  Dvalue = 3.5
  Group = -> [Ba_element003]
  conduct = 2
  density = 1
  expand = 3
  formula = Ba
  name = G4_Ba
  specific = 4
FEATURE [App::DocumentObjectGroupPython] La_element003  label="La_element : 003"  # scripted group (container) (typed FeaturePython)
  n = 1
  ref = La_element
FEATURE [App::DocumentObjectGroupPython] G4_La  # scripted group (container) (typed FeaturePython)
  Dunit = g/cm3
  Dvalue = 6.154
  Group = -> [La_element003]
  conduct = 2
  density = 1
  expand = 3
  formula = La
  name = G4_La
  specific = 4
FEATURE [App::DocumentObjectGroupPython] Ce_element002  label="Ce_element : 1"  # scripted group (container) (typed FeaturePython)
  n = 1
  ref = Ce_element
FEATURE [App::DocumentObjectGroupPython] G4_Ce  # scripted group (container) (typed FeaturePython)
  Dunit = g/cm3
  Dvalue = 6.657
  Group = -> [Ce_element002]
  conduct = 2
  density = 1
  expand = 3
  formula = Ce
  name = G4_Ce
  specific = 4
FEATURE [App::DocumentObjectGroupPython] Pr_element001  label="Pr_element : 1"  # scripted group (container) (typed FeaturePython)
  n = 1
  ref = Pr_element
FEATURE [App::DocumentObjectGroupPython] G4_Pr  # scripted group (container) (typed FeaturePython)
  Dunit = g/cm3
  Dvalue = 6.71
  Group = -> [Pr_element001]
  conduct = 2
  density = 1
  expand = 3
  formula = Pr
  name = G4_Pr
  specific = 4
FEATURE [App::DocumentObjectGroupPython] Nd_element001  label="Nd_element : 1"  # scripted group (container) (typed FeaturePython)
  n = 1
  ref = Nd_element
FEATURE [App::DocumentObjectGroupPython] G4_Nd  # scripted group (container) (typed FeaturePython)
  Dunit = g/cm3
  Dvalue = 6.9
  Group = -> [Nd_element001]
  conduct = 2
  density = 1
  expand = 3
  formula = Nd
  name = G4_Nd
  specific = 4
FEATURE [App::DocumentObjectGroupPython] Pm_element001  label="Pm_element : 1"  # scripted group (container) (typed FeaturePython)
  n = 1
  ref = Pm_element
FEATURE [App::DocumentObjectGroupPython] G4_Pm  # scripted group (container) (typed FeaturePython)
  Dunit = g/cm3
  Dvalue = 7.22
  Group = -> [Pm_element001]
  conduct = 2
  density = 1
  expand = 3
  formula = Pm
  name = G4_Pm
  specific = 4
FEATURE [App::DocumentObjectGroupPython] Sm_element001  label="Sm_element : 1"  # scripted group (container) (typed FeaturePython)
  n = 1
  ref = Sm_element
FEATURE [App::DocumentObjectGroupPython] G4_Sm  # scripted group (container) (typed FeaturePython)
  Dunit = g/cm3
  Dvalue = 7.46
  Group = -> [Sm_element001]
  conduct = 2
  density = 1
  expand = 3
  formula = Sm
  name = G4_Sm
  specific = 4
FEATURE [App::DocumentObjectGroupPython] Eu_element001  label="Eu_element : 1"  # scripted group (container) (typed FeaturePython)
  n = 1
  ref = Eu_element
FEATURE [App::DocumentObjectGroupPython] G4_Eu  # scripted group (container) (typed FeaturePython)
  Dunit = g/cm3
  Dvalue = 5.243
  Group = -> [Eu_element001]
  conduct = 2
  density = 1
  expand = 3
  formula = Eu
  name = G4_Eu
  specific = 4
FEATURE [App::DocumentObjectGroupPython] Gd_element002  label="Gd_element : 1"  # scripted group (container) (typed FeaturePython)
  n = 1
  ref = Gd_element
FEATURE [App::DocumentObjectGroupPython] G4_Gd  # scripted group (container) (typed FeaturePython)
  Dunit = g/cm3
  Dvalue = 7.9004
  Group = -> [Gd_element002]
  conduct = 2
  density = 1
  expand = 3
  formula = Gd
  name = G4_Gd
  specific = 4
FEATURE [App::DocumentObjectGroupPython] Tb_element001  label="Tb_element : 1"  # scripted group (container) (typed FeaturePython)
  n = 1
  ref = Tb_element
FEATURE [App::DocumentObjectGroupPython] G4_Tb  # scripted group (container) (typed FeaturePython)
  Dunit = g/cm3
  Dvalue = 8.229
  Group = -> [Tb_element001]
  conduct = 2
  density = 1
  expand = 3
  formula = Tb
  name = G4_Tb
  specific = 4
FEATURE [App::DocumentObjectGroupPython] Dy_element001  label="Dy_element : 1"  # scripted group (container) (typed FeaturePython)
  n = 1
  ref = Dy_element
FEATURE [App::DocumentObjectGroupPython] G4_Dy  # scripted group (container) (typed FeaturePython)
  Dunit = g/cm3
  Dvalue = 8.55
  Group = -> [Dy_element001]
  conduct = 2
  density = 1
  expand = 3
  formula = Dy
  name = G4_Dy
  specific = 4
FEATURE [App::DocumentObjectGroupPython] Ho_element001  label="Ho_element : 1"  # scripted group (container) (typed FeaturePython)
  n = 1
  ref = Ho_element
FEATURE [App::DocumentObjectGroupPython] G4_Ho  # scripted group (container) (typed FeaturePython)
  Dunit = g/cm3
  Dvalue = 8.795
  Group = -> [Ho_element001]
  conduct = 2
  density = 1
  expand = 3
  formula = Ho
  name = G4_Ho
  specific = 4
FEATURE [App::DocumentObjectGroupPython] Er_element001  label="Er_element : 1"  # scripted group (container) (typed FeaturePython)
  n = 1
  ref = Er_element
FEATURE [App::DocumentObjectGroupPython] G4_Er  # scripted group (container) (typed FeaturePython)
  Dunit = g/cm3
  Dvalue = 9.066
  Group = -> [Er_element001]
  conduct = 2
  density = 1
  expand = 3
  formula = Er
  name = G4_Er
  specific = 4
FEATURE [App::DocumentObjectGroupPython] Tm_element001  label="Tm_element : 1"  # scripted group (container) (typed FeaturePython)
  n = 1
  ref = Tm_element
FEATURE [App::DocumentObjectGroupPython] G4_Tm  # scripted group (container) (typed FeaturePython)
  Dunit = g/cm3
  Dvalue = 9.321
  Group = -> [Tm_element001]
  conduct = 2
  density = 1
  expand = 3
  formula = Tm
  name = G4_Tm
  specific = 4
FEATURE [App::DocumentObjectGroupPython] Yb_element001  label="Yb_element : 1"  # scripted group (container) (typed FeaturePython)
  n = 1
  ref = Yb_element
FEATURE [App::DocumentObjectGroupPython] G4_Yb  # scripted group (container) (typed FeaturePython)
  Dunit = g/cm3
  Dvalue = 6.73
  Group = -> [Yb_element001]
  conduct = 2
  density = 1
  expand = 3
  formula = Yb
  name = G4_Yb
  specific = 4
FEATURE [App::DocumentObjectGroupPython] Lu_element001  label="Lu_element : 1"  # scripted group (container) (typed FeaturePython)
  n = 1
  ref = Lu_element
FEATURE [App::DocumentObjectGroupPython] G4_Lu  # scripted group (container) (typed FeaturePython)
  Dunit = g/cm3
  Dvalue = 9.84
  Group = -> [Lu_element001]
  conduct = 2
  density = 1
  expand = 3
  formula = Lu
  name = G4_Lu
  specific = 4
FEATURE [App::DocumentObjectGroupPython] Hf_element001  label="Hf_element : 1"  # scripted group (container) (typed FeaturePython)
  n = 1
  ref = Hf_element
FEATURE [App::DocumentObjectGroupPython] G4_Hf  # scripted group (container) (typed FeaturePython)
  Dunit = g/cm3
  Dvalue = 13.31
  Group = -> [Hf_element001]
  conduct = 2
  density = 1
  expand = 3
  formula = Hf
  name = G4_Hf
  specific = 4
FEATURE [App::DocumentObjectGroupPython] Ta_element001  label="Ta_element : 1"  # scripted group (container) (typed FeaturePython)
  n = 1
  ref = Ta_element
FEATURE [App::DocumentObjectGroupPython] G4_Ta  # scripted group (container) (typed FeaturePython)
  Dunit = g/cm3
  Dvalue = 16.654
  Group = -> [Ta_element001]
  conduct = 2
  density = 1
  expand = 3
  formula = Ta
  name = G4_Ta
  specific = 4
FEATURE [App::DocumentObjectGroupPython] W_element004  label="W_element : 004"  # scripted group (container) (typed FeaturePython)
  n = 1
  ref = W_element
FEATURE [App::DocumentObjectGroupPython] G4_W  # scripted group (container) (typed FeaturePython)
  Dunit = g/cm3
  Dvalue = 19.3
  Group = -> [W_element004]
  conduct = 2
  density = 1
  expand = 3
  formula = W
  name = G4_W
  specific = 4
FEATURE [App::DocumentObjectGroupPython] Re_element001  label="Re_element : 1"  # scripted group (container) (typed FeaturePython)
  n = 1
  ref = Re_element
FEATURE [App::DocumentObjectGroupPython] G4_Re  # scripted group (container) (typed FeaturePython)
  Dunit = g/cm3
  Dvalue = 21.02
  Group = -> [Re_element001]
  conduct = 2
  density = 1
  expand = 3
  formula = Re
  name = G4_Re
  specific = 4
FEATURE [App::DocumentObjectGroupPython] Os_element001  label="Os_element : 1"  # scripted group (container) (typed FeaturePython)
  n = 1
  ref = Os_element
FEATURE [App::DocumentObjectGroupPython] G4_Os  # scripted group (container) (typed FeaturePython)
  Dunit = g/cm3
  Dvalue = 22.57
  Group = -> [Os_element001]
  conduct = 2
  density = 1
  expand = 3
  formula = Os
  name = G4_Os
  specific = 4
FEATURE [App::DocumentObjectGroupPython] Ir_element001  label="Ir_element : 1"  # scripted group (container) (typed FeaturePython)
  n = 1
  ref = Ir_element
FEATURE [App::DocumentObjectGroupPython] G4_Ir  # scripted group (container) (typed FeaturePython)
  Dunit = g/cm3
  Dvalue = 22.42
  Group = -> [Ir_element001]
  conduct = 2
  density = 1
  expand = 3
  formula = Ir
  name = G4_Ir
  specific = 4
FEATURE [App::DocumentObjectGroupPython] Pt_element001  label="Pt_element : 1"  # scripted group (container) (typed FeaturePython)
  n = 1
  ref = Pt_element
FEATURE [App::DocumentObjectGroupPython] G4_Pt  # scripted group (container) (typed FeaturePython)
  Dunit = g/cm3
  Dvalue = 21.45
  Group = -> [Pt_element001]
  conduct = 2
  density = 1
  expand = 3
  formula = Pt
  name = G4_Pt
  specific = 4
FEATURE [App::DocumentObjectGroupPython] Au_element001  label="Au_element : 1"  # scripted group (container) (typed FeaturePython)
  n = 1
  ref = Au_element
FEATURE [App::DocumentObjectGroupPython] G4_Au  # scripted group (container) (typed FeaturePython)
  Dunit = g/cm3
  Dvalue = 19.32
  Group = -> [Au_element001]
  conduct = 2
  density = 1
  expand = 3
  formula = Au
  name = G4_Au
  specific = 4
FEATURE [App::DocumentObjectGroupPython] Hg_element002  label="Hg_element : 002"  # scripted group (container) (typed FeaturePython)
  n = 1
  ref = Hg_element
FEATURE [App::DocumentObjectGroupPython] G4_Hg  # scripted group (container) (typed FeaturePython)
  Dunit = g/cm3
  Dvalue = 13.546
  Group = -> [Hg_element002]
  conduct = 2
  density = 1
  expand = 3
  formula = Hg
  name = G4_Hg
  specific = 4
FEATURE [App::DocumentObjectGroupPython] Tl_element002  label="Tl_element : 002"  # scripted group (container) (typed FeaturePython)
  n = 1
  ref = Tl_element
FEATURE [App::DocumentObjectGroupPython] G4_Tl  # scripted group (container) (typed FeaturePython)
  Dunit = g/cm3
  Dvalue = 11.72
  Group = -> [Tl_element002]
  conduct = 2
  density = 1
  expand = 3
  formula = Tl
  name = G4_Tl
  specific = 4
FEATURE [App::DocumentObjectGroupPython] Pb_element003  label="Pb_element : 1"  # scripted group (container) (typed FeaturePython)
  n = 1
  ref = Pb_element
FEATURE [App::DocumentObjectGroupPython] G4_Pb  # scripted group (container) (typed FeaturePython)
  Dunit = g/cm3
  Dvalue = 11.35
  Group = -> [Pb_element003]
  conduct = 2
  density = 1
  expand = 3
  formula = Pb
  name = G4_Pb
  specific = 4
FEATURE [App::DocumentObjectGroupPython] Bi_element002  label="Bi_element : 1"  # scripted group (container) (typed FeaturePython)
  n = 1
  ref = Bi_element
FEATURE [App::DocumentObjectGroupPython] G4_Bi  # scripted group (container) (typed FeaturePython)
  Dunit = g/cm3
  Dvalue = 9.747
  Group = -> [Bi_element002]
  conduct = 2
  density = 1
  expand = 3
  formula = Bi
  name = G4_Bi
  specific = 4
FEATURE [App::DocumentObjectGroupPython] Po_element001  label="Po_element : 1"  # scripted group (container) (typed FeaturePython)
  n = 1
  ref = Po_element
FEATURE [App::DocumentObjectGroupPython] G4_Po  # scripted group (container) (typed FeaturePython)
  Dunit = g/cm3
  Dvalue = 9.32
  Group = -> [Po_element001]
  conduct = 2
  density = 1
  expand = 3
  formula = Po
  name = G4_Po
  specific = 4
FEATURE [App::DocumentObjectGroupPython] At_element001  label="At_element : 1"  # scripted group (container) (typed FeaturePython)
  n = 1
  ref = At_element
FEATURE [App::DocumentObjectGroupPython] G4_At  # scripted group (container) (typed FeaturePython)
  Dunit = g/cm3
  Dvalue = 9.32
  Group = -> [At_element001]
  conduct = 2
  density = 1
  expand = 3
  formula = At
  name = G4_At
  specific = 4
FEATURE [App::DocumentObjectGroupPython] Rn_element001  label="Rn_element : 1"  # scripted group (container) (typed FeaturePython)
  n = 1
  ref = Rn_element
FEATURE [App::DocumentObjectGroupPython] G4_Rn  # scripted group (container) (typed FeaturePython)
  Dunit = g/cm3
  Dvalue = 0.00900662
  Group = -> [Rn_element001]
  conduct = 2
  density = 1
  expand = 3
  formula = Rn
  name = G4_Rn
  specific = 4
FEATURE [App::DocumentObjectGroupPython] Fr_element001  label="Fr_element : 1"  # scripted group (container) (typed FeaturePython)
  n = 1
  ref = Fr_element
FEATURE [App::DocumentObjectGroupPython] G4_Fr  # scripted group (container) (typed FeaturePython)
  Dunit = g/cm3
  Dvalue = 1
  Group = -> [Fr_element001]
  conduct = 2
  density = 1
  expand = 3
  formula = Fr
  name = G4_Fr
  specific = 4
FEATURE [App::DocumentObjectGroupPython] Ra_element001  label="Ra_element : 1"  # scripted group (container) (typed FeaturePython)
  n = 1
  ref = Ra_element
FEATURE [App::DocumentObjectGroupPython] G4_Ra  # scripted group (container) (typed FeaturePython)
  Dunit = g/cm3
  Dvalue = 5
  Group = -> [Ra_element001]
  conduct = 2
  density = 1
  expand = 3
  formula = Ra
  name = G4_Ra
  specific = 4
FEATURE [App::DocumentObjectGroupPython] Ac_element001  label="Ac_element : 1"  # scripted group (container) (typed FeaturePython)
  n = 1
  ref = Ac_element
FEATURE [App::DocumentObjectGroupPython] G4_Ac  # scripted group (container) (typed FeaturePython)
  Dunit = g/cm3
  Dvalue = 10.07
  Group = -> [Ac_element001]
  conduct = 2
  density = 1
  expand = 3
  formula = Ac
  name = G4_Ac
  specific = 4
FEATURE [App::DocumentObjectGroupPython] Th_element001  label="Th_element : 1"  # scripted group (container) (typed FeaturePython)
  n = 1
  ref = Th_element
FEATURE [App::DocumentObjectGroupPython] G4_Th  # scripted group (container) (typed FeaturePython)
  Dunit = g/cm3
  Dvalue = 11.72
  Group = -> [Th_element001]
  conduct = 2
  density = 1
  expand = 3
  formula = Th
  name = G4_Th
  specific = 4
FEATURE [App::DocumentObjectGroupPython] Pa_element001  label="Pa_element : 1"  # scripted group (container) (typed FeaturePython)
  n = 1
  ref = Pa_element
FEATURE [App::DocumentObjectGroupPython] G4_Pa  # scripted group (container) (typed FeaturePython)
  Dunit = g/cm3
  Dvalue = 15.37
  Group = -> [Pa_element001]
  conduct = 2
  density = 1
  expand = 3
  formula = Pa
  name = G4_Pa
  specific = 4
FEATURE [App::DocumentObjectGroupPython] U_element004  label="U_element : 004"  # scripted group (container) (typed FeaturePython)
  n = 1
  ref = U_element
FEATURE [App::DocumentObjectGroupPython] G4_U  # scripted group (container) (typed FeaturePython)
  Dunit = g/cm3
  Dvalue = 18.95
  Group = -> [U_element004]
  conduct = 2
  density = 1
  expand = 3
  formula = U
  name = G4_U
  specific = 4
FEATURE [App::DocumentObjectGroupPython] Np_element001  label="Np_element : 1"  # scripted group (container) (typed FeaturePython)
  n = 1
  ref = Np_element
FEATURE [App::DocumentObjectGroupPython] G4_Np  # scripted group (container) (typed FeaturePython)
  Dunit = g/cm3
  Dvalue = 20.25
  Group = -> [Np_element001]
  conduct = 2
  density = 1
  expand = 3
  formula = Np
  name = G4_Np
  specific = 4
FEATURE [App::DocumentObjectGroupPython] Pu_element002  label="Pu_element : 002"  # scripted group (container) (typed FeaturePython)
  n = 1
  ref = Pu_element
FEATURE [App::DocumentObjectGroupPython] G4_Pu  # scripted group (container) (typed FeaturePython)
  Dunit = g/cm3
  Dvalue = 19.84
  Group = -> [Pu_element002]
  conduct = 2
  density = 1
  expand = 3
  formula = Pu
  name = G4_Pu
  specific = 4
FEATURE [App::DocumentObjectGroupPython] Am_element001  label="Am_element : 1"  # scripted group (container) (typed FeaturePython)
  n = 1
  ref = Am_element
FEATURE [App::DocumentObjectGroupPython] G4_Am  # scripted group (container) (typed FeaturePython)
  Dunit = g/cm3
  Dvalue = 13.67
  Group = -> [Am_element001]
  conduct = 2
  density = 1
  expand = 3
  formula = Am
  name = G4_Am
  specific = 4
FEATURE [App::DocumentObjectGroupPython] Cm_element001  label="Cm_element : 1"  # scripted group (container) (typed FeaturePython)
  n = 1
  ref = Cm_element
FEATURE [App::DocumentObjectGroupPython] G4_Cm  # scripted group (container) (typed FeaturePython)
  Dunit = g/cm3
  Dvalue = 13.51
  Group = -> [Cm_element001]
  conduct = 2
  density = 1
  expand = 3
  formula = Cm
  name = G4_Cm
  specific = 4
FEATURE [App::DocumentObjectGroupPython] Bk_element001  label="Bk_element : 1"  # scripted group (container) (typed FeaturePython)
  n = 1
  ref = Bk_element
FEATURE [App::DocumentObjectGroupPython] G4_Bk  # scripted group (container) (typed FeaturePython)
  Dunit = g/cm3
  Dvalue = 14
  Group = -> [Bk_element001]
  conduct = 2
  density = 1
  expand = 3
  formula = Bk
  name = G4_Bk
  specific = 4
FEATURE [App::DocumentObjectGroupPython] Cf_element001  label="Cf_element : 1"  # scripted group (container) (typed FeaturePython)
  n = 1
  ref = Cf_element
FEATURE [App::DocumentObjectGroupPython] G4_Cf  # scripted group (container) (typed FeaturePython)
  Dunit = g/cm3
  Dvalue = 10
  Group = -> [Cf_element001]
  conduct = 2
  density = 1
  expand = 3
  formula = Cf
  name = G4_Cf
  specific = 4
FEATURE [App::DocumentObjectGroupPython] Element  # scripted group (container) (typed FeaturePython)
  Group = -> [G4_H,G4_He,G4_Li,G4_Be,G4_B,G4_C,G4_N,G4_O,G4_F,G4_Ne,G4_Na,G4_Mg,G4_Al,G4_Si,G4_P,G4_S,G4_Cl,G4_Ar,G4_K,G4_Ca,G4_Sc,G4_Ti,G4_V,G4_Cr,G4_Mn,G4_Fe,G4_Co,G4_Ni,G4_Cu,G4_Zn,G4_Ga,G4_Ge,G4_As,G4_Se,G4_Br,G4_Kr,G4_Rb,G4_Sr,G4_Y,G4_Zr,G4_Nb,G4_Mo,G4_Tc,G4_Ru,G4_Rh,G4_Pd,G4_Ag,G4_Cd,G4_In,G4_Sn,G4_Sb,G4_Te,G4_I,G4_Xe,G4_Cs,G4_Ba,G4_La,G4_Ce,G4_Pr,G4_Nd,G4_Pm,G4_Sm,G4_Eu,G4_Gd,G4_Tb,G4_Dy,G4_Ho,G4_Er,+30 more]
FEATURE [App::DocumentObjectGroupPython] H_element114  label="H_element : 063"  # scripted group (container) (typed FeaturePython)
  n = 2
  ref = H_element
FEATURE [App::DocumentObjectGroupPython] G4_lH2  # scripted group (container) (typed FeaturePython)
  Dunit = g/cm3
  Dvalue = 0.0708
  Group = -> [H_element114]
  conduct = 2
  density = 1
  expand = 3
  formula = G4_lH2
  name = G4_lH2
  specific = 4
FEATURE [App::DocumentObjectGroupPython] N_element049  label="N_element : 022"  # scripted group (container) (typed FeaturePython)
  n = 2
  ref = N_element
FEATURE [App::DocumentObjectGroupPython] G4_lN2  # scripted group (container) (typed FeaturePython)
  Dunit = g/cm3
  Dvalue = 0.807
  Group = -> [N_element049]
  conduct = 2
  density = 1
  expand = 3
  formula = G4_lN2
  name = G4_lN2
  specific = 4
FEATURE [App::DocumentObjectGroupPython] O_element106  label="O_element : 060"  # scripted group (container) (typed FeaturePython)
  n = 2
  ref = O_element
FEATURE [App::DocumentObjectGroupPython] G4_lO2  # scripted group (container) (typed FeaturePython)
  Dunit = g/cm3
  Dvalue = 1.141
  Group = -> [O_element106]
  conduct = 2
  density = 1
  expand = 3
  formula = G4_lO2
  name = G4_lO2
  specific = 4
FEATURE [App::DocumentObjectGroupPython] Ar  label="Ar : 1"  # scripted group (container) (typed FeaturePython)
  n = 1
  ref = Ar
FEATURE [App::DocumentObjectGroupPython] G4_lAr  # scripted group (container) (typed FeaturePython)
  Dunit = g/cm3
  Dvalue = 1.396
  Group = -> [Ar]
  conduct = 2
  density = 1
  expand = 3
  formula = G4_lAr
  name = G4_lAr
  specific = 4
FEATURE [App::DocumentObjectGroupPython] Br  label="Br : 1"  # scripted group (container) (typed FeaturePython)
  n = 1
  ref = Br
FEATURE [App::DocumentObjectGroupPython] G4_lBr  # scripted group (container) (typed FeaturePython)
  Dunit = g/cm3
  Dvalue = 3.1028
  Group = -> [Br]
  conduct = 2
  density = 1
  expand = 3
  formula = G4_lBr
  name = G4_lBr
  specific = 4
FEATURE [App::DocumentObjectGroupPython] Kr  label="Kr : 1"  # scripted group (container) (typed FeaturePython)
  n = 1
  ref = Kr
FEATURE [App::DocumentObjectGroupPython] G4_lKr  # scripted group (container) (typed FeaturePython)
  Dunit = g/cm3
  Dvalue = 2.418
  Group = -> [Kr]
  conduct = 2
  density = 1
  expand = 3
  formula = G4_lKr
  name = G4_lKr
  specific = 4
FEATURE [App::DocumentObjectGroupPython] Xe  label="Xe : 1"  # scripted group (container) (typed FeaturePython)
  n = 1
  ref = Xe
FEATURE [App::DocumentObjectGroupPython] G4_lXe  # scripted group (container) (typed FeaturePython)
  Dunit = g/cm3
  Dvalue = 2.953
  Group = -> [Xe]
  conduct = 2
  density = 1
  expand = 3
  formula = G4_lXe
  name = G4_lXe
  specific = 4
FEATURE [App::DocumentObjectGroupPython] O_element107  label="O_element : 061"  # scripted group (container) (typed FeaturePython)
  n = 4
  ref = O_element
FEATURE [App::DocumentObjectGroupPython] Pb_element004  label="Pb_element : 002"  # scripted group (container) (typed FeaturePython)
  n = 1
  ref = Pb_element
FEATURE [App::DocumentObjectGroupPython] W_element005  label="W_element : 005"  # scripted group (container) (typed FeaturePython)
  n = 1
  ref = W_element
FEATURE [App::DocumentObjectGroupPython] G4_PbWO4  # scripted group (container) (typed FeaturePython)
  Dunit = g/cm3
  Dvalue = 8.28
  Group = -> [O_element107,Pb_element004,W_element005]
  conduct = 2
  density = 1
  expand = 3
  formula = G4_PbWO4
  name = G4_PbWO4
  specific = 4
FEATURE [App::DocumentObjectGroupPython] alactic  label="alactic : 1"  # scripted group (container) (typed FeaturePython)
  n = 1
  ref = alactic
FEATURE [App::DocumentObjectGroupPython] G4_Galactic  # scripted group (container) (typed FeaturePython)
  Dunit = g/cm3
  Dvalue = 0
  Group = -> [alactic]
  conduct = 2
  density = 1
  expand = 3
  formula = G4_Galactic
  name = G4_Galactic
  specific = 4
FEATURE [App::DocumentObjectGroupPython] RAPHITE_POROUS  label="RAPHITE_POROUS : 1"  # scripted group (container) (typed FeaturePython)
  n = 1
  ref = RAPHITE_POROUS
FEATURE [App::DocumentObjectGroupPython] G4_GRAPHITE_POROUS  # scripted group (container) (typed FeaturePython)
  Dunit = g/cm3
  Dvalue = 1.7
  Group = -> [RAPHITE_POROUS]
  conduct = 2
  density = 1
  expand = 3
  formula = G4_GRAPHITE_POROUS
  name = G4_GRAPHITE_POROUS
  specific = 4
FEATURE [App::DocumentObjectGroupPython] H_element115  label="H_element : 0.150"  # scripted group (container) (typed FeaturePython)
  n = 0.080538
FEATURE [App::DocumentObjectGroupPython] C_element125  label="C_element : 0.600"  # scripted group (container) (typed FeaturePython)
  n = 0.599848
FEATURE [App::DocumentObjectGroupPython] O_element108  label="O_element : 0.320"  # scripted group (container) (typed FeaturePython)
  n = 0.319614
FEATURE [App::DocumentObjectGroupPython] G4_LUCITE  # scripted group (container) (typed FeaturePython)
  Dunit = g/cm3
  Dvalue = 1.19
  Group = -> [H_element115,C_element125,O_element108]
  conduct = 2
  density = 1
  expand = 3
  formula = G4_LUCITE
  name = G4_LUCITE
  specific = 4
FEATURE [App::DocumentObjectGroupPython] Cu_element002  label="Cu_element : 62"  # scripted group (container) (typed FeaturePython)
  n = 62
  ref = Cu_element
FEATURE [App::DocumentObjectGroupPython] Zn_element002  label="Zn_element : 35"  # scripted group (container) (typed FeaturePython)
  n = 35
  ref = Zn_element
FEATURE [App::DocumentObjectGroupPython] Pb_element005  label="Pb_element : 3"  # scripted group (container) (typed FeaturePython)
  n = 3
  ref = Pb_element
FEATURE [App::DocumentObjectGroupPython] G4_BRASS  # scripted group (container) (typed FeaturePython)
  Dunit = g/cm3
  Dvalue = 8.52
  Group = -> [Cu_element002,Zn_element002,Pb_element005]
  conduct = 2
  density = 1
  expand = 3
  formula = G4_BRASS
  name = G4_BRASS
  specific = 4
FEATURE [App::DocumentObjectGroupPython] Cu_element003  label="Cu_element : 89"  # scripted group (container) (typed FeaturePython)
  n = 89
  ref = Cu_element
FEATURE [App::DocumentObjectGroupPython] Zn_element003  label="Zn_element : 9"  # scripted group (container) (typed FeaturePython)
  n = 9
  ref = Zn_element
FEATURE [App::DocumentObjectGroupPython] Pb_element006  label="Pb_element : 2"  # scripted group (container) (typed FeaturePython)
  n = 2
  ref = Pb_element
FEATURE [App::DocumentObjectGroupPython] G4_BRONZE  # scripted group (container) (typed FeaturePython)
  Dunit = g/cm3
  Dvalue = 8.82
  Group = -> [Cu_element003,Zn_element003,Pb_element006]
  conduct = 2
  density = 1
  expand = 3
  formula = G4_BRONZE
  name = G4_BRONZE
  specific = 4
FEATURE [App::DocumentObjectGroupPython] Fe_element008  label="Fe_element : 74"  # scripted group (container) (typed FeaturePython)
  n = 74
  ref = Fe_element
FEATURE [App::DocumentObjectGroupPython] Cr_element002  label="Cr_element : 18"  # scripted group (container) (typed FeaturePython)
  n = 18
  ref = Cr_element
FEATURE [App::DocumentObjectGroupPython] Ni_element002  label="Ni_element : 8"  # scripted group (container) (typed FeaturePython)
  n = 8
  ref = Ni_element
FEATURE [App::DocumentObjectGroupPython] G4_STAINLESS_STEEL  label="G4_STAINLESS-STEEL"  # scripted group (container) (typed FeaturePython)
  Dunit = g/cm3
  Dvalue = 8
  Group = -> [Fe_element008,Cr_element002,Ni_element002]
  conduct = 2
  density = 1
  expand = 3
  formula = G4_STAINLESS-STEEL
  name = G4_STAINLESS-STEEL
  specific = 4
FEATURE [App::DocumentObjectGroupPython] H_element116  label="H_element : 064"  # scripted group (container) (typed FeaturePython)
  n = 18
  ref = H_element
FEATURE [App::DocumentObjectGroupPython] C_element126  label="C_element : 071"  # scripted group (container) (typed FeaturePython)
  n = 12
  ref = C_element
FEATURE [App::DocumentObjectGroupPython] O_element109  label="O_element : 062"  # scripted group (container) (typed FeaturePython)
  n = 7
  ref = O_element
FEATURE [App::DocumentObjectGroupPython] G4_CR39  # scripted group (container) (typed FeaturePython)
  Dunit = g/cm3
  Dvalue = 1.32
  Group = -> [H_element116,C_element126,O_element109]
  conduct = 2
  density = 1
  expand = 3
  formula = G4_CR39
  name = G4_CR39
  specific = 4
FEATURE [App::DocumentObjectGroupPython] H_element117  label="H_element : 38"  # scripted group (container) (typed FeaturePython)
  n = 38
  ref = H_element
FEATURE [App::DocumentObjectGroupPython] C_element127  label="C_element : 072"  # scripted group (container) (typed FeaturePython)
  n = 18
  ref = C_element
FEATURE [App::DocumentObjectGroupPython] O_element110  label="O_element : 063"  # scripted group (container) (typed FeaturePython)
  n = 1
  ref = O_element
FEATURE [App::DocumentObjectGroupPython] G4_OCTADECANOL  # scripted group (container) (typed FeaturePython)
  Dunit = g/cm3
  Dvalue = 0.812
  Group = -> [H_element117,C_element127,O_element110]
  conduct = 2
  density = 1
  expand = 3
  formula = G4_OCTADECANOL
  name = G4_OCTADECANOL
  specific = 4
FEATURE [App::DocumentObjectGroupPython] HEP  # scripted group (container) (typed FeaturePython)
  Group = -> [G4_lH2,G4_lN2,G4_lO2,G4_lAr,G4_lBr,G4_lKr,G4_lXe,G4_PbWO4,G4_Galactic,G4_GRAPHITE_POROUS,G4_LUCITE,G4_BRASS,G4_BRONZE,G4_STAINLESS_STEEL,G4_CR39,G4_OCTADECANOL]
FEATURE [App::DocumentObjectGroupPython] C_element128  label="C_element : 073"  # scripted group (container) (typed FeaturePython)
  n = 14
  ref = C_element
FEATURE [App::DocumentObjectGroupPython] H_element118  label="H_element : 065"  # scripted group (container) (typed FeaturePython)
  n = 10
  ref = H_element
FEATURE [App::DocumentObjectGroupPython] O_element111  label="O_element : 064"  # scripted group (container) (typed FeaturePython)
  n = 2
  ref = O_element
FEATURE [App::DocumentObjectGroupPython] N_element050  label="N_element : 023"  # scripted group (container) (typed FeaturePython)
  n = 2
  ref = N_element
FEATURE [App::DocumentObjectGroupPython] G4_KEVLAR  # scripted group (container) (typed FeaturePython)
  Dunit = g/cm3
  Dvalue = 1.44
  Group = -> [C_element128,H_element118,O_element111,N_element050]
  conduct = 2
  density = 1
  expand = 3
  formula = G4_KEVLAR
  name = G4_KEVLAR
  specific = 4
FEATURE [App::DocumentObjectGroupPython] C_element129  label="C_element : 074"  # scripted group (container) (typed FeaturePython)
  n = 10
  ref = C_element
FEATURE [App::DocumentObjectGroupPython] H_element119  label="H_element : 066"  # scripted group (container) (typed FeaturePython)
  n = 8
  ref = H_element
FEATURE [App::DocumentObjectGroupPython] O_element112  label="O_element : 065"  # scripted group (container) (typed FeaturePython)
  n = 4
  ref = O_element
FEATURE [App::DocumentObjectGroupPython] G4_DACRON  # scripted group (container) (typed FeaturePython)
  Dunit = g/cm3
  Dvalue = 1.4
  Group = -> [C_element129,H_element119,O_element112]
  conduct = 2
  density = 1
  expand = 3
  formula = G4_DACRON
  name = G4_DACRON
  specific = 4
FEATURE [App::DocumentObjectGroupPython] C_element130  label="C_element : 075"  # scripted group (container) (typed FeaturePython)
  n = 4
  ref = C_element
FEATURE [App::DocumentObjectGroupPython] H_element120  label="H_element : 067"  # scripted group (container) (typed FeaturePython)
  n = 5
  ref = H_element
FEATURE [App::DocumentObjectGroupPython] Cl_element030  label="Cl_element : 016"  # scripted group (container) (typed FeaturePython)
  n = 1
  ref = Cl_element
FEATURE [App::DocumentObjectGroupPython] G4_NEOPRENE  # scripted group (container) (typed FeaturePython)
  Dunit = g/cm3
  Dvalue = 1.23
  Group = -> [C_element130,H_element120,Cl_element030]
  conduct = 2
  density = 1
  expand = 3
  formula = G4_NEOPRENE
  name = G4_NEOPRENE
  specific = 4
FEATURE [App::DocumentObjectGroupPython] Space  # scripted group (container) (typed FeaturePython)
  Group = -> [G4_KEVLAR,G4_DACRON,G4_NEOPRENE]
FEATURE [App::DocumentObjectGroupPython] H_element121  label="H_element : 068"  # scripted group (container) (typed FeaturePython)
  n = 5
  ref = H_element
FEATURE [App::DocumentObjectGroupPython] C_element131  label="C_element : 076"  # scripted group (container) (typed FeaturePython)
  n = 4
  ref = C_element
FEATURE [App::DocumentObjectGroupPython] N_element051  label="N_element : 3"  # scripted group (container) (typed FeaturePython)
  n = 3
  ref = N_element
FEATURE [App::DocumentObjectGroupPython] O_element113  label="O_element : 066"  # scripted group (container) (typed FeaturePython)
  n = 1
  ref = O_element
FEATURE [App::DocumentObjectGroupPython] G4_CYTOSINE  # scripted group (container) (typed FeaturePython)
  Dunit = g/cm3
  Dvalue = 1.55
  Group = -> [H_element121,C_element131,N_element051,O_element113]
  conduct = 2
  density = 1
  expand = 3
  formula = G4_CYTOSINE
  name = G4_CYTOSINE
  specific = 4
FEATURE [App::DocumentObjectGroupPython] H_element122  label="H_element : 069"  # scripted group (container) (typed FeaturePython)
  n = 6
  ref = H_element
FEATURE [App::DocumentObjectGroupPython] C_element132  label="C_element : 077"  # scripted group (container) (typed FeaturePython)
  n = 5
  ref = C_element
FEATURE [App::DocumentObjectGroupPython] N_element052  label="N_element : 024"  # scripted group (container) (typed FeaturePython)
  n = 2
  ref = N_element
FEATURE [App::DocumentObjectGroupPython] O_element114  label="O_element : 067"  # scripted group (container) (typed FeaturePython)
  n = 2
  ref = O_element
FEATURE [App::DocumentObjectGroupPython] G4_THYMINE  # scripted group (container) (typed FeaturePython)
  Dunit = g/cm3
  Dvalue = 1.23
  Group = -> [H_element122,C_element132,N_element052,O_element114]
  conduct = 2
  density = 1
  expand = 3
  formula = G4_THYMINE
  name = G4_THYMINE
  specific = 4
FEATURE [App::DocumentObjectGroupPython] H_element123  label="H_element : 070"  # scripted group (container) (typed FeaturePython)
  n = 4
  ref = H_element
FEATURE [App::DocumentObjectGroupPython] C_element133  label="C_element : 078"  # scripted group (container) (typed FeaturePython)
  n = 4
  ref = C_element
FEATURE [App::DocumentObjectGroupPython] N_element053  label="N_element : 025"  # scripted group (container) (typed FeaturePython)
  n = 2
  ref = N_element
FEATURE [App::DocumentObjectGroupPython] O_element115  label="O_element : 068"  # scripted group (container) (typed FeaturePython)
  n = 2
  ref = O_element
FEATURE [App::DocumentObjectGroupPython] G4_URACIL  # scripted group (container) (typed FeaturePython)
  Dunit = g/cm3
  Dvalue = 1.32
  Group = -> [H_element123,C_element133,N_element053,O_element115]
  conduct = 2
  density = 1
  expand = 3
  formula = G4_URACIL
  name = G4_URACIL
  specific = 4
FEATURE [App::DocumentObjectGroupPython] H_element124  label="H_element : 071"  # scripted group (container) (typed FeaturePython)
  n = 4
  ref = H_element
FEATURE [App::DocumentObjectGroupPython] C_element134  label="C_element : 079"  # scripted group (container) (typed FeaturePython)
  n = 5
  ref = C_element
FEATURE [App::DocumentObjectGroupPython] N_element054  label="N_element : 026"  # scripted group (container) (typed FeaturePython)
  n = 5
  ref = N_element
FEATURE [App::DocumentObjectGroupPython] G4_DNA_ADENINE  # scripted group (container) (typed FeaturePython)
  Dunit = g/cm3
  Dvalue = 1
  Group = -> [H_element124,C_element134,N_element054]
  conduct = 2
  density = 1
  expand = 3
  formula = G4_DNA_ADENINE
  name = G4_DNA_ADENINE
  specific = 4
FEATURE [App::DocumentObjectGroupPython] H_element125  label="H_element : 072"  # scripted group (container) (typed FeaturePython)
  n = 4
  ref = H_element
FEATURE [App::DocumentObjectGroupPython] C_element135  label="C_element : 080"  # scripted group (container) (typed FeaturePython)
  n = 5
  ref = C_element
FEATURE [App::DocumentObjectGroupPython] N_element055  label="N_element : 027"  # scripted group (container) (typed FeaturePython)
  n = 5
  ref = N_element
FEATURE [App::DocumentObjectGroupPython] O_element116  label="O_element : 069"  # scripted group (container) (typed FeaturePython)
  n = 1
  ref = O_element
FEATURE [App::DocumentObjectGroupPython] G4_DNA_GUANINE  # scripted group (container) (typed FeaturePython)
  Dunit = g/cm3
  Dvalue = 1
  Group = -> [H_element125,C_element135,N_element055,O_element116]
  conduct = 2
  density = 1
  expand = 3
  formula = G4_DNA_GUANINE
  name = G4_DNA_GUANINE
  specific = 4
FEATURE [App::DocumentObjectGroupPython] H_element126  label="H_element : 073"  # scripted group (container) (typed FeaturePython)
  n = 4
  ref = H_element
FEATURE [App::DocumentObjectGroupPython] C_element136  label="C_element : 081"  # scripted group (container) (typed FeaturePython)
  n = 4
  ref = C_element
FEATURE [App::DocumentObjectGroupPython] N_element056  label="N_element : 028"  # scripted group (container) (typed FeaturePython)
  n = 3
  ref = N_element
FEATURE [App::DocumentObjectGroupPython] O_element117  label="O_element : 070"  # scripted group (container) (typed FeaturePython)
  n = 1
  ref = O_element
FEATURE [App::DocumentObjectGroupPython] G4_DNA_CYTOSINE  # scripted group (container) (typed FeaturePython)
  Dunit = g/cm3
  Dvalue = 1
  Group = -> [H_element126,C_element136,N_element056,O_element117]
  conduct = 2
  density = 1
  expand = 3
  formula = G4_DNA_CYTOSINE
  name = G4_DNA_CYTOSINE
  specific = 4
FEATURE [App::DocumentObjectGroupPython] H_element127  label="H_element : 074"  # scripted group (container) (typed FeaturePython)
  n = 5
  ref = H_element
FEATURE [App::DocumentObjectGroupPython] C_element137  label="C_element : 082"  # scripted group (container) (typed FeaturePython)
  n = 5
  ref = C_element
FEATURE [App::DocumentObjectGroupPython] N_element057  label="N_element : 029"  # scripted group (container) (typed FeaturePython)
  n = 2
  ref = N_element
FEATURE [App::DocumentObjectGroupPython] O_element118  label="O_element : 071"  # scripted group (container) (typed FeaturePython)
  n = 2
  ref = O_element
FEATURE [App::DocumentObjectGroupPython] G4_DNA_THYMINE  # scripted group (container) (typed FeaturePython)
  Dunit = g/cm3
  Dvalue = 1
  Group = -> [H_element127,C_element137,N_element057,O_element118]
  conduct = 2
  density = 1
  expand = 3
  formula = G4_DNA_THYMINE
  name = G4_DNA_THYMINE
  specific = 4
FEATURE [App::DocumentObjectGroupPython] H_element128  label="H_element : 075"  # scripted group (container) (typed FeaturePython)
  n = 3
  ref = H_element
FEATURE [App::DocumentObjectGroupPython] C_element138  label="C_element : 083"  # scripted group (container) (typed FeaturePython)
  n = 4
  ref = C_element
FEATURE [App::DocumentObjectGroupPython] N_element058  label="N_element : 030"  # scripted group (container) (typed FeaturePython)
  n = 2
  ref = N_element
FEATURE [App::DocumentObjectGroupPython] O_element119  label="O_element : 072"  # scripted group (container) (typed FeaturePython)
  n = 2
  ref = O_element
FEATURE [App::DocumentObjectGroupPython] G4_DNA_URACIL  # scripted group (container) (typed FeaturePython)
  Dunit = g/cm3
  Dvalue = 1
  Group = -> [H_element128,C_element138,N_element058,O_element119]
  conduct = 2
  density = 1
  expand = 3
  formula = G4_DNA_URACIL
  name = G4_DNA_URACIL
  specific = 4
FEATURE [App::DocumentObjectGroupPython] H_element129  label="H_element : 076"  # scripted group (container) (typed FeaturePython)
  n = 10
  ref = H_element
FEATURE [App::DocumentObjectGroupPython] C_element139  label="C_element : 084"  # scripted group (container) (typed FeaturePython)
  n = 10
  ref = C_element
FEATURE [App::DocumentObjectGroupPython] N_element059  label="N_element : 031"  # scripted group (container) (typed FeaturePython)
  n = 5
  ref = N_element
FEATURE [App::DocumentObjectGroupPython] O_element120  label="O_element : 073"  # scripted group (container) (typed FeaturePython)
  n = 4
  ref = O_element
FEATURE [App::DocumentObjectGroupPython] G4_DNA_ADENOSINE  # scripted group (container) (typed FeaturePython)
  Dunit = g/cm3
  Dvalue = 1
  Group = -> [H_element129,C_element139,N_element059,O_element120]
  conduct = 2
  density = 1
  expand = 3
  formula = G4_DNA_ADENOSINE
  name = G4_DNA_ADENOSINE
  specific = 4
FEATURE [App::DocumentObjectGroupPython] H_element130  label="H_element : 077"  # scripted group (container) (typed FeaturePython)
  n = 10
  ref = H_element
FEATURE [App::DocumentObjectGroupPython] C_element140  label="C_element : 085"  # scripted group (container) (typed FeaturePython)
  n = 10
  ref = C_element
FEATURE [App::DocumentObjectGroupPython] N_element060  label="N_element : 032"  # scripted group (container) (typed FeaturePython)
  n = 5
  ref = N_element
FEATURE [App::DocumentObjectGroupPython] O_element121  label="O_element : 074"  # scripted group (container) (typed FeaturePython)
  n = 5
  ref = O_element
FEATURE [App::DocumentObjectGroupPython] G4_DNA_GUANOSINE  # scripted group (container) (typed FeaturePython)
  Dunit = g/cm3
  Dvalue = 1
  Group = -> [H_element130,C_element140,N_element060,O_element121]
  conduct = 2
  density = 1
  expand = 3
  formula = G4_DNA_GUANOSINE
  name = G4_DNA_GUANOSINE
  specific = 4
FEATURE [App::DocumentObjectGroupPython] H_element131  label="H_element : 078"  # scripted group (container) (typed FeaturePython)
  n = 10
  ref = H_element
FEATURE [App::DocumentObjectGroupPython] C_element141  label="C_element : 086"  # scripted group (container) (typed FeaturePython)
  n = 9
  ref = C_element
FEATURE [App::DocumentObjectGroupPython] N_element061  label="N_element : 033"  # scripted group (container) (typed FeaturePython)
  n = 3
  ref = N_element
FEATURE [App::DocumentObjectGroupPython] O_element122  label="O_element : 075"  # scripted group (container) (typed FeaturePython)
  n = 5
  ref = O_element
FEATURE [App::DocumentObjectGroupPython] G4_DNA_CYTIDINE  # scripted group (container) (typed FeaturePython)
  Dunit = g/cm3
  Dvalue = 1
  Group = -> [H_element131,C_element141,N_element061,O_element122]
  conduct = 2
  density = 1
  expand = 3
  formula = G4_DNA_CYTIDINE
  name = G4_DNA_CYTIDINE
  specific = 4
FEATURE [App::DocumentObjectGroupPython] H_element132  label="H_element : 079"  # scripted group (container) (typed FeaturePython)
  n = 9
  ref = H_element
FEATURE [App::DocumentObjectGroupPython] C_element142  label="C_element : 087"  # scripted group (container) (typed FeaturePython)
  n = 9
  ref = C_element
FEATURE [App::DocumentObjectGroupPython] N_element062  label="N_element : 034"  # scripted group (container) (typed FeaturePython)
  n = 2
  ref = N_element
FEATURE [App::DocumentObjectGroupPython] O_element123  label="O_element : 076"  # scripted group (container) (typed FeaturePython)
  n = 6
  ref = O_element
FEATURE [App::DocumentObjectGroupPython] G4_DNA_URIDINE  # scripted group (container) (typed FeaturePython)
  Dunit = g/cm3
  Dvalue = 1
  Group = -> [H_element132,C_element142,N_element062,O_element123]
  conduct = 2
  density = 1
  expand = 3
  formula = G4_DNA_URIDINE
  name = G4_DNA_URIDINE
  specific = 4
FEATURE [App::DocumentObjectGroupPython] H_element133  label="H_element : 080"  # scripted group (container) (typed FeaturePython)
  n = 11
  ref = H_element
FEATURE [App::DocumentObjectGroupPython] C_element143  label="C_element : 088"  # scripted group (container) (typed FeaturePython)
  n = 10
  ref = C_element
FEATURE [App::DocumentObjectGroupPython] N_element063  label="N_element : 035"  # scripted group (container) (typed FeaturePython)
  n = 2
  ref = N_element
FEATURE [App::DocumentObjectGroupPython] O_element124  label="O_element : 077"  # scripted group (container) (typed FeaturePython)
  n = 6
  ref = O_element
FEATURE [App::DocumentObjectGroupPython] G4_DNA_METHYLURIDINE  # scripted group (container) (typed FeaturePython)
  Dunit = g/cm3
  Dvalue = 1
  Group = -> [H_element133,C_element143,N_element063,O_element124]
  conduct = 2
  density = 1
  expand = 3
  formula = G4_DNA_METHYLURIDINE
  name = G4_DNA_METHYLURIDINE
  specific = 4
FEATURE [App::DocumentObjectGroupPython] P_element014  label="P_element : 003"  # scripted group (container) (typed FeaturePython)
  n = 1
  ref = P_element
FEATURE [App::DocumentObjectGroupPython] O_element125  label="O_element : 078"  # scripted group (container) (typed FeaturePython)
  n = 3
  ref = O_element
FEATURE [App::DocumentObjectGroupPython] G4_DNA_MONOPHOSPHATE  # scripted group (container) (typed FeaturePython)
  Dunit = g/cm3
  Dvalue = 1
  Group = -> [P_element014,O_element125]
  conduct = 2
  density = 1
  expand = 3
  formula = G4_DNA_MONOPHOSPHATE
  name = G4_DNA_MONOPHOSPHATE
  specific = 4
FEATURE [App::DocumentObjectGroupPython] H_element134  label="H_element : 081"  # scripted group (container) (typed FeaturePython)
  n = 10
  ref = H_element
FEATURE [App::DocumentObjectGroupPython] C_element144  label="C_element : 089"  # scripted group (container) (typed FeaturePython)
  n = 10
  ref = C_element
FEATURE [App::DocumentObjectGroupPython] N_element064  label="N_element : 036"  # scripted group (container) (typed FeaturePython)
  n = 5
  ref = N_element
FEATURE [App::DocumentObjectGroupPython] O_element126  label="O_element : 079"  # scripted group (container) (typed FeaturePython)
  n = 7
  ref = O_element
FEATURE [App::DocumentObjectGroupPython] P_element015  label="P_element : 004"  # scripted group (container) (typed FeaturePython)
  n = 1
  ref = P_element
FEATURE [App::DocumentObjectGroupPython] G4_DNA_A  # scripted group (container) (typed FeaturePython)
  Dunit = g/cm3
  Dvalue = 1
  Group = -> [H_element134,C_element144,N_element064,O_element126,P_element015]
  conduct = 2
  density = 1
  expand = 3
  formula = G4_DNA_A
  name = G4_DNA_A
  specific = 4
FEATURE [App::DocumentObjectGroupPython] H_element135  label="H_element : 082"  # scripted group (container) (typed FeaturePython)
  n = 10
  ref = H_element
FEATURE [App::DocumentObjectGroupPython] C_element145  label="C_element : 090"  # scripted group (container) (typed FeaturePython)
  n = 10
  ref = C_element
FEATURE [App::DocumentObjectGroupPython] N_element065  label="N_element : 037"  # scripted group (container) (typed FeaturePython)
  n = 5
  ref = N_element
FEATURE [App::DocumentObjectGroupPython] O_element127  label="O_element : 8"  # scripted group (container) (typed FeaturePython)
  n = 8
  ref = O_element
FEATURE [App::DocumentObjectGroupPython] P_element016  label="P_element : 005"  # scripted group (container) (typed FeaturePython)
  n = 1
  ref = P_element
FEATURE [App::DocumentObjectGroupPython] G4_DNA_G  # scripted group (container) (typed FeaturePython)
  Dunit = g/cm3
  Dvalue = 1
  Group = -> [H_element135,C_element145,N_element065,O_element127,P_element016]
  conduct = 2
  density = 1
  expand = 3
  formula = G4_DNA_G
  name = G4_DNA_G
  specific = 4
FEATURE [App::DocumentObjectGroupPython] H_element136  label="H_element : 083"  # scripted group (container) (typed FeaturePython)
  n = 10
  ref = H_element
FEATURE [App::DocumentObjectGroupPython] C_element146  label="C_element : 091"  # scripted group (container) (typed FeaturePython)
  n = 9
  ref = C_element
FEATURE [App::DocumentObjectGroupPython] N_element066  label="N_element : 038"  # scripted group (container) (typed FeaturePython)
  n = 3
  ref = N_element
FEATURE [App::DocumentObjectGroupPython] O_element128  label="O_element : 080"  # scripted group (container) (typed FeaturePython)
  n = 8
  ref = O_element
FEATURE [App::DocumentObjectGroupPython] P_element017  label="P_element : 006"  # scripted group (container) (typed FeaturePython)
  n = 1
  ref = P_element
FEATURE [App::DocumentObjectGroupPython] G4_DNA_C  # scripted group (container) (typed FeaturePython)
  Dunit = g/cm3
  Dvalue = 1
  Group = -> [H_element136,C_element146,N_element066,O_element128,P_element017]
  conduct = 2
  density = 1
  expand = 3
  formula = G4_DNA_C
  name = G4_DNA_C
  specific = 4
FEATURE [App::DocumentObjectGroupPython] H_element137  label="H_element : 084"  # scripted group (container) (typed FeaturePython)
  n = 9
  ref = H_element
FEATURE [App::DocumentObjectGroupPython] C_element147  label="C_element : 092"  # scripted group (container) (typed FeaturePython)
  n = 9
  ref = C_element
FEATURE [App::DocumentObjectGroupPython] N_element067  label="N_element : 039"  # scripted group (container) (typed FeaturePython)
  n = 2
  ref = N_element
FEATURE [App::DocumentObjectGroupPython] O_element129  label="O_element : 9"  # scripted group (container) (typed FeaturePython)
  n = 9
  ref = O_element
FEATURE [App::DocumentObjectGroupPython] P_element018  label="P_element : 007"  # scripted group (container) (typed FeaturePython)
  n = 1
  ref = P_element
FEATURE [App::DocumentObjectGroupPython] G4_DNA_U  # scripted group (container) (typed FeaturePython)
  Dunit = g/cm3
  Dvalue = 1
  Group = -> [H_element137,C_element147,N_element067,O_element129,P_element018]
  conduct = 2
  density = 1
  expand = 3
  formula = G4_DNA_U
  name = G4_DNA_U
  specific = 4
FEATURE [App::DocumentObjectGroupPython] H_element138  label="H_element : 085"  # scripted group (container) (typed FeaturePython)
  n = 11
  ref = H_element
FEATURE [App::DocumentObjectGroupPython] C_element148  label="C_element : 093"  # scripted group (container) (typed FeaturePython)
  n = 10
  ref = C_element
FEATURE [App::DocumentObjectGroupPython] N_element068  label="N_element : 040"  # scripted group (container) (typed FeaturePython)
  n = 2
  ref = N_element
FEATURE [App::DocumentObjectGroupPython] O_element130  label="O_element : 081"  # scripted group (container) (typed FeaturePython)
  n = 9
  ref = O_element
FEATURE [App::DocumentObjectGroupPython] P_element019  label="P_element : 008"  # scripted group (container) (typed FeaturePython)
  n = 1
  ref = P_element
FEATURE [App::DocumentObjectGroupPython] G4_DNA_MU  # scripted group (container) (typed FeaturePython)
  Dunit = g/cm3
  Dvalue = 1
  Group = -> [H_element138,C_element148,N_element068,O_element130,P_element019]
  conduct = 2
  density = 1
  expand = 3
  formula = G4_DNA_MU
  name = G4_DNA_MU
  specific = 4
FEATURE [App::DocumentObjectGroupPython] BioChemical  # scripted group (container) (typed FeaturePython)
  Group = -> [G4_CYTOSINE,G4_THYMINE,G4_URACIL,G4_DNA_ADENINE,G4_DNA_GUANINE,G4_DNA_CYTOSINE,G4_DNA_THYMINE,G4_DNA_URACIL,G4_DNA_ADENOSINE,G4_DNA_GUANOSINE,G4_DNA_CYTIDINE,G4_DNA_URIDINE,G4_DNA_METHYLURIDINE,G4_DNA_MONOPHOSPHATE,G4_DNA_A,G4_DNA_G,G4_DNA_C,G4_DNA_U,G4_DNA_MU]
FEATURE [App::DocumentObjectGroupPython] G4Materials  # scripted group (container) (typed FeaturePython)
  Group = -> [NIST,Element,HEP,Space,BioChemical]
  version = 1
FEATURE [App::DocumentObjectGroupPython] Geant4  # scripted group (container) (typed FeaturePython)
  Group = -> [G4Isotopes,G4Elements,G4Materials]
FEATURE [Part::FeaturePython] GDMLBox_WorldBox  # WARN: FeaturePython — macro-defined, semantics opaque (R4)
  lunit = 2
  material = 8
  x = 114.01
  y = 147.706
  z = 147.706
FEATURE [Part::FeaturePython] GDMLBox_Box  # WARN: FeaturePython — macro-defined, semantics opaque (R4)
  Placement = pos=(0,0,37.85) rot=(0,0,1;0rad)
  lunit = 2
  material = 1
  x = 27.8
  y = 27.8
  z = 8
FEATURE [Part::FeaturePython] GDMLBox_Box003  # WARN: FeaturePython — macro-defined, semantics opaque (R4)
  Placement = pos=(-11.99,-11.99,5) rot=(0,0,1;0rad)
  lunit = 2
  material = 0
  x = 3.22
  y = 3.22
  z = 2
FEATURE [Part::FeaturePython] Array  label="Child_Array"  # Draft array (typed FeaturePython)
  AlwaysSyncPlacement = false
  Angle = 360
  ArrayType = 0
  Axis = (0,0,1)
  Base = -> GDMLBox_Box003
  Center = (0,0,0)
  Count = 64
  ExpandArray = false
  Fuse = false
  IntervalAxis = (0,0,0)
  IntervalX = (3.4,0,0)
  IntervalY = (0,3.4,0)
  IntervalZ = (0,0,100)
  NumberCircles = 3
  NumberPolar = 5
  NumberX = 8
  NumberY = 8
  NumberZ = 1
  Placement = pos=(0,0,37.85) rot=(0,0,1;0rad)
  PlacementList = 64 placements: [(-11.99,-11.99,5),(-11.99,-8.59,5),(-11.99,-5.19,5),(-11.99,-1.79,5),(-11.99,1.61,5),(-11.99,5.01,5),(-11.99,8.41,5),(-11.99,11.81,5),(-8.59,-11.99,5),(-8.59,-8.59,5),(-8.59,-5.19,5),(-8.59,-1.79,5),(-8.59,1.61,5),(-8.59,5.01,5),(-8.59,8.41,5),(-8.59,11.81,5),(-5.19,-11.99,5),(-5.19,-8.59,5),(-5.19,-5.19,5),(-5.19,-1.79,5),(-5.19,1.61,5),(-5.19,5.01,5),(-5.19,8.41,5),(-5.19,11.81,5),+40 more]
  RadialDistance = 50
  ScaleList = (64) [(1,1,1),(1,1,1),(1,1,1),(1,1,1),(1,1,1),(1,1,1),(1,1,1),(1,1,1),(1,1,1),(1,1,1),(1,1,1),(1,1,1),(1,1,1),(1,1,1),(1,1,1),(1,1,1),(1,1,1),(1,1,1),+46 more]
  Symmetry = 1
  TangentialDistance = 25
FEATURE [App::DocumentObjectGroupPython] G4_Pyrex_Glass001  label="G4_Pyrex_Glass : 1.000"  # scripted group (container) (typed FeaturePython)
  n = 1
FEATURE [App::DocumentObjectGroupPython] Glass  # scripted group (container) (typed FeaturePython)
  Dunit = g/cm3
  Dvalue = 1.032
  Group = -> [G4_Pyrex_Glass001]
  RINDEX = RINDEXLAR
  conduct = 2
  density = 1
  expand = 3
  name = Glass
  specific = 4
FEATURE [App::DocumentObjectGroupPython] G4_CESIUM_IODIDE  label="G4_CESIUM_IODIDE : 1.000"  # scripted group (container) (typed FeaturePython)
  n = 1
FEATURE [App::DocumentObjectGroupPython] LYSO  # scripted group (container) (typed FeaturePython)
  ABSLENGTH = ABSLENGTHLAR
  Dunit = g/cm3
  Dvalue = 7.1
  FASTCOMPONENT = SCINTLAR
  FASTTIMECONSTANT = FTC
  Group = -> [G4_CESIUM_IODIDE]
  RAYLEIGH = RAYLEIGHLAR
  REEMISSIONPROB = SCINTLAR
  RESOLUTIONSCALE = RS
  RINDEX = RINDEXLAR
  SCINTILLATIONYIELD = SY
  SLOWCOMPONENT = SCINTLAR
  SLOWTIMECONSTANT = STC
  YIELDRATIO = YR
  conduct = 2
  density = 1
  expand = 3
  name = LYSO
  specific = 4
FEATURE [App::DocumentObjectGroupPython] Materials  # scripted group (container) (typed FeaturePython)
  Group = -> [Air,Geant4,Glass,LYSO]
FEATURE [Part::FeaturePython] Array001  label="Parent_Array"  # Draft array (typed FeaturePython)
  AlwaysSyncPlacement = false
  Angle = 360
  ArrayType = 1
  Axis = (0,1,0)
  Base = -> Array
  Center = (0,0,0)
  Count = 8
  ExpandArray = false
  Fuse = false
  IntervalAxis = (0,0,0)
  IntervalX = (50,0,0)
  IntervalY = (0,50,0)
  IntervalZ = (0,0,50)
  NumberCircles = 3
  NumberPolar = 8
  NumberX = 2
  NumberY = 2
  NumberZ = 1
  PlacementList = 8 placements: [(0,0,37.85),(26.764,0,26.764),(37.85,0,8.40439e-15),(26.764,0,-26.764),(4.63529e-15,0,-37.85),(-26.764,0,-26.764),(-37.85,0,-8.40439e-15),(-26.764,0,26.764)]
  RadialDistance = 50
  ScaleList = (8) [(1,1,1),(1,1,1),(1,1,1),(1,1,1),(1,1,1),(1,1,1),(1,1,1),(1,1,1)]
  Symmetry = 1
  TangentialDistance = 25
FEATURE [App::Part] Part
  Group = -> [GDMLBox_Box003,Array,Array001]
  Origin = -> Origin003
FEATURE [Part::FeaturePython] Array002  # Draft array (typed FeaturePython)
  AlwaysSyncPlacement = false
  Angle = 360
  ArrayType = 1
  Axis = (0,1,0)
  Base = -> GDMLBox_Box
  Center = (0,0,0)
  Count = 8
  ExpandArray = false
  Fuse = false
  IntervalAxis = (0,0,0)
  IntervalX = (50,0,0)
  IntervalY = (0,50,0)
  IntervalZ = (0,0,50)
  NumberCircles = 3
  NumberPolar = 8
  NumberX = 2
  NumberY = 2
  NumberZ = 1
  PlacementList = 8 placements: [(0,0,37.85),(26.764,0,26.764),(37.85,0,8.40439e-15),(26.764,0,-26.764),(4.63529e-15,0,-37.85),(-26.764,0,-26.764),(-37.85,0,-8.40439e-15),(-26.764,0,26.764)]
  RadialDistance = 50
  ScaleList = (8) [(1,1,1),(1,1,1),(1,1,1),(1,1,1),(1,1,1),(1,1,1),(1,1,1),(1,1,1)]
  Symmetry = 1
  TangentialDistance = 25
FEATURE [App::Part] Part001
  Group = -> [GDMLBox_Box,Array002]
  Origin = -> Origin002
  SkinSurface = 0
FEATURE [Part::FeaturePython] GDMLSphere_Sphere  # WARN: FeaturePython — macro-defined, semantics opaque (R4)
  aunit = 1
  deltaphi = 360
  deltatheta = 180
  lunit = 2
  material = 164
  rmax = 5
  rmin = 0
  startphi = 0
  starttheta = 0
FEATURE [App::Part] LV_Sphere
  Group = -> [GDMLSphere_Sphere]
  Origin = -> Origin004
FEATURE [App::Part] worldVOL
  Group = -> [GDMLBox_WorldBox,Part001,Part,LV_Sphere]
  Origin = -> Origin
FEATURE [App::FeaturePython] ScintWrap1  # WARN: FeaturePython — macro-defined, semantics opaque (R4)
  PV1 = Part001
  PV2 = LV_Sphere
  Surface = ScintWrap
